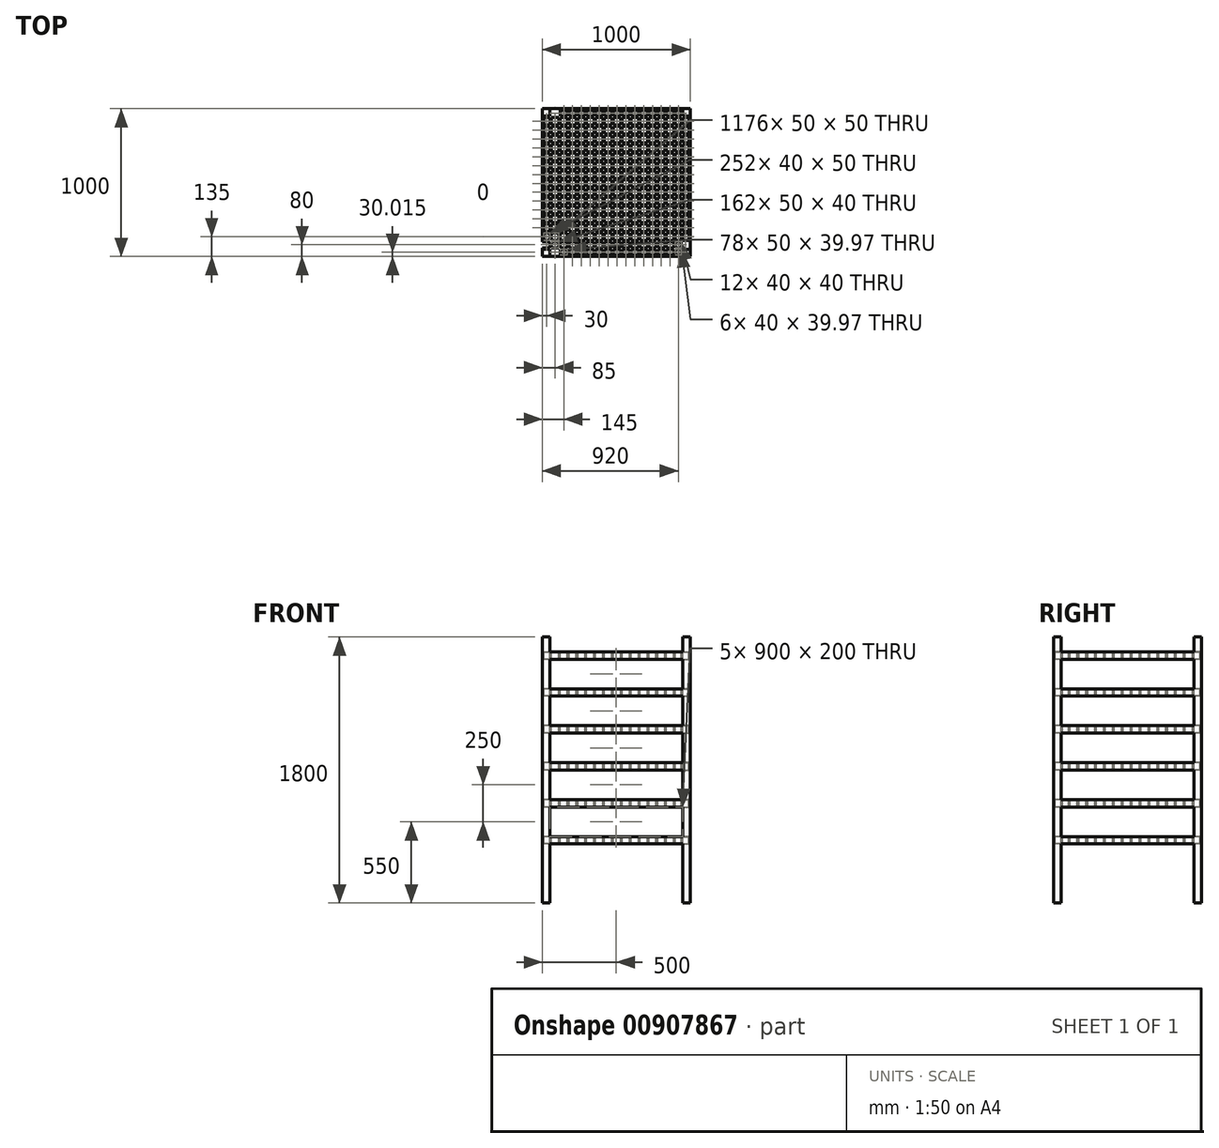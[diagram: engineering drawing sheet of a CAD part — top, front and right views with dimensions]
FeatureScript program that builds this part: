
annotation { "Feature Type Name" : "Feature", "Feature Type Description" : "" }
export const myFeature = defineFeature(function(context is Context, id is Id, definition is map)
    precondition{}
    {
        {
            var Q0;
            Q0=qCreatedBy(makeId("Top.planeOp"),FACE);
            var sketch = newSketch(context, id + "F0", { "sketchPlane" : qUnion([Q0])});
            skLineSegment(sketch, "E0", {"start": v(0, 0) * mm, "end": v(0, 1000) * mm});
            skLineSegment(sketch, "E1", {"start": v(0, 1000) * mm, "end": v(-1000, 1000) * mm});
            skLineSegment(sketch, "E2", {"start": v(-1000, 1000) * mm, "end": v(-1000, 0) * mm});
            skLineSegment(sketch, "E3", {"start": v(-1000, 0) * mm, "end": v(0, 0) * mm});
            skSolve(sketch);
        }
        {
            var Q0;
            Q0=makeQuery(id+"F0.imprint","IMPRINT",FACE,{"disambiguationData":[TD([[makeQuery(id+"F0.imprint","IMPRINT",EDGE,{"derivedFrom":sQuery(id+"F0.wireOp",EDGE,"E0")}),1.0]])]});
            extrude(context, id + "F1", {"entities" : qUnion([Q0]), "depth" : 1800 * mm, "offsetDistance" : 25 * mm});
        }
        {
            var Q0;
            Q0=makeQuery(id+"F1.opExtrude","SWEPT_FACE",FACE,{"disambiguationData":[OSD([sQuery(id+"F0.wireOp",EDGE,"E3")])]});
            var sketch = newSketch(context, id + "F2", { "sketchPlane" : qUnion([Q0])});
            skLineSegment(sketch, "E4", {"start": v(-1000, 0) * mm, "end": v(-950, 0) * mm});
            skLineSegment(sketch, "E5", {"start": v(0, 0) * mm, "end": v(-50, 0) * mm});
            skLineSegment(sketch, "E6", {"start": v(0, 1800) * mm, "end": v(-50, 1800) * mm});
            skLineSegment(sketch, "E7", {"start": v(-50, 1800) * mm, "end": v(-50, 0) * mm});
            skLineSegment(sketch, "E8", {"start": v(-950, 0) * mm, "end": v(-950, 400) * mm});
            skLineSegment(sketch, "E9", {"start": v(-950, 400) * mm, "end": v(-950, 450) * mm});
            skLineSegment(sketch, "E10", {"start": v(-950, 450) * mm, "end": v(-950, 650) * mm});
            skLineSegment(sketch, "E11", {"start": v(-950, 650) * mm, "end": v(-950, 700) * mm});
            skLineSegment(sketch, "E12", {"start": v(-950, 700) * mm, "end": v(-950, 900) * mm});
            skLineSegment(sketch, "E13", {"start": v(-950, 900) * mm, "end": v(-950, 950) * mm});
            skLineSegment(sketch, "E14", {"start": v(-950, 950) * mm, "end": v(-950, 1150) * mm});
            skLineSegment(sketch, "E15", {"start": v(-950, 1150) * mm, "end": v(-950, 1200) * mm});
            skLineSegment(sketch, "E16", {"start": v(-950, 1200) * mm, "end": v(-950, 1400) * mm});
            skLineSegment(sketch, "E17", {"start": v(-950, 1400) * mm, "end": v(-950, 1450) * mm});
            skLineSegment(sketch, "E18", {"start": v(-950, 1450) * mm, "end": v(-950, 1650) * mm});
            skLineSegment(sketch, "E19", {"start": v(-950, 1650) * mm, "end": v(-950, 1700) * mm});
            skLineSegment(sketch, "E20", {"start": v(-950, 1700) * mm, "end": v(-950, 1800) * mm});
            skLineSegment(sketch, "E21", {"start": v(-950, 1700) * mm, "end": v(-50, 1700) * mm});
            skLineSegment(sketch, "E22", {"start": v(-950, 1650) * mm, "end": v(-50, 1650) * mm});
            skLineSegment(sketch, "E23", {"start": v(-950, 1450) * mm, "end": v(-50, 1450) * mm});
            skLineSegment(sketch, "E24", {"start": v(-950, 1400) * mm, "end": v(-50, 1400) * mm});
            skLineSegment(sketch, "E25", {"start": v(-950, 1200) * mm, "end": v(-50, 1200) * mm});
            skLineSegment(sketch, "E26", {"start": v(-950, 1150) * mm, "end": v(-50, 1150) * mm});
            skLineSegment(sketch, "E27", {"start": v(-950, 950) * mm, "end": v(-50, 950) * mm});
            skLineSegment(sketch, "E28", {"start": v(-950, 900) * mm, "end": v(-50, 900) * mm});
            skLineSegment(sketch, "E29", {"start": v(-950, 700) * mm, "end": v(-50, 700) * mm});
            skLineSegment(sketch, "E30", {"start": v(-950, 650) * mm, "end": v(-50, 650) * mm});
            skLineSegment(sketch, "E31", {"start": v(-950, 450) * mm, "end": v(-50, 450) * mm});
            skLineSegment(sketch, "E32", {"start": v(-950, 400) * mm, "end": v(-50, 400) * mm});
            skSolve(sketch);
        }
        {
            var Q0;
            Q0=makeQuery(id+"F1.opExtrude","SWEPT_FACE",FACE,{"disambiguationData":[OSD([sQuery(id+"F0.wireOp",EDGE,"E0")])]});
            var sketch = newSketch(context, id + "F3", { "sketchPlane" : qUnion([Q0])});
            skLineSegment(sketch, "E33", {"start": v(0, 0) * mm, "end": v(50, 0) * mm});
            skLineSegment(sketch, "E34", {"start": v(1000, 1800) * mm, "end": v(950, 1800) * mm});
            skLineSegment(sketch, "E35", {"start": v(950, 1800) * mm, "end": v(950, 0) * mm});
            skLineSegment(sketch, "E36", {"start": v(50, 0) * mm, "end": v(50, 400) * mm});
            skLineSegment(sketch, "E37", {"start": v(50, 400) * mm, "end": v(50, 450) * mm});
            skLineSegment(sketch, "E38", {"start": v(50, 450) * mm, "end": v(50, 650) * mm});
            skLineSegment(sketch, "E39", {"start": v(50, 650) * mm, "end": v(50, 700) * mm});
            skLineSegment(sketch, "E40", {"start": v(50, 700) * mm, "end": v(50, 900) * mm});
            skLineSegment(sketch, "E41", {"start": v(50, 900) * mm, "end": v(50, 950) * mm});
            skLineSegment(sketch, "E42", {"start": v(50, 950) * mm, "end": v(50, 1150) * mm});
            skLineSegment(sketch, "E43", {"start": v(50, 1150) * mm, "end": v(50, 1200) * mm});
            skLineSegment(sketch, "E44", {"start": v(50, 1200) * mm, "end": v(50, 1400) * mm});
            skLineSegment(sketch, "E45", {"start": v(50, 1400) * mm, "end": v(50, 1450) * mm});
            skLineSegment(sketch, "E46", {"start": v(50, 1450) * mm, "end": v(50, 1650) * mm});
            skLineSegment(sketch, "E47", {"start": v(50, 1650) * mm, "end": v(50, 1700) * mm});
            skLineSegment(sketch, "E48", {"start": v(50, 1700) * mm, "end": v(50, 1800) * mm});
            skLineSegment(sketch, "E49", {"start": v(50, 1700) * mm, "end": v(950, 1700) * mm});
            skLineSegment(sketch, "E50", {"start": v(50, 1650) * mm, "end": v(950, 1650) * mm});
            skLineSegment(sketch, "E51", {"start": v(50, 1450) * mm, "end": v(950, 1450) * mm});
            skLineSegment(sketch, "E52", {"start": v(50, 1400) * mm, "end": v(950, 1400) * mm});
            skLineSegment(sketch, "E53", {"start": v(50, 1200) * mm, "end": v(950, 1200) * mm});
            skLineSegment(sketch, "E54", {"start": v(50, 1150) * mm, "end": v(950, 1150) * mm});
            skLineSegment(sketch, "E55", {"start": v(50, 950) * mm, "end": v(950, 950) * mm});
            skLineSegment(sketch, "E56", {"start": v(50, 900) * mm, "end": v(950, 900) * mm});
            skLineSegment(sketch, "E57", {"start": v(50, 700) * mm, "end": v(950, 700) * mm});
            skLineSegment(sketch, "E58", {"start": v(50, 650) * mm, "end": v(950, 650) * mm});
            skLineSegment(sketch, "E59", {"start": v(50, 450) * mm, "end": v(950, 450) * mm});
            skLineSegment(sketch, "E60", {"start": v(50, 400) * mm, "end": v(950, 400) * mm});
            skSolve(sketch);
        }
        {
            var Q0;
            {var subQ4=sQuery(id+"F2.wireOp",EDGE,"E8");Q0=makeQuery(id+"F2.imprint","IMPRINT",FACE,{"disambiguationData":[TD([[makeQuery(id+"F2.imprint","IMPRINT",EDGE,{"derivedFrom":subQ4}),-1.0]])]});}
            var Q1;
            Q1=makeQuery(id+"F2.imprint","IMPRINT",FACE,{"disambiguationData":[TD([[makeQuery(id+"F2.imprint","IMPRINT",EDGE,{"derivedFrom":sQuery(id+"F2.wireOp",EDGE,"E10")}),-1.0]])]});
            var Q2;
            Q2=makeQuery(id+"F2.imprint","IMPRINT",FACE,{"disambiguationData":[TD([[makeQuery(id+"F2.imprint","IMPRINT",EDGE,{"derivedFrom":sQuery(id+"F2.wireOp",EDGE,"E12")}),-1.0]])]});
            var Q3;
            Q3=makeQuery(id+"F2.imprint","IMPRINT",FACE,{"disambiguationData":[TD([[makeQuery(id+"F2.imprint","IMPRINT",EDGE,{"derivedFrom":sQuery(id+"F2.wireOp",EDGE,"E14")}),-1.0]])]});
            var Q4;
            Q4=makeQuery(id+"F2.imprint","IMPRINT",FACE,{"disambiguationData":[TD([[makeQuery(id+"F2.imprint","IMPRINT",EDGE,{"derivedFrom":sQuery(id+"F2.wireOp",EDGE,"E16")}),-1.0]])]});
            var Q5;
            Q5=makeQuery(id+"F2.imprint","IMPRINT",FACE,{"disambiguationData":[TD([[makeQuery(id+"F2.imprint","IMPRINT",EDGE,{"derivedFrom":sQuery(id+"F2.wireOp",EDGE,"E18")}),-1.0]])]});
            var Q6;
            {var subQ4=sQuery(id+"F2.wireOp",EDGE,"E20");Q6=makeQuery(id+"F2.imprint","IMPRINT",FACE,{"disambiguationData":[TD([[makeQuery(id+"F2.imprint","IMPRINT",EDGE,{"derivedFrom":subQ4}),-1.0]])]});}
            extrude(context, id + "F4", {"entities" : qUnion([Q0, Q1, Q2, Q3, Q4, Q5, Q6]), "operationType" : NewBodyOperationType.REMOVE, "oppositeDirection" : true, "depth" : 1000 * mm, "offsetDistance" : 25 * mm});
        }
        {
            var Q0;
            {var subQ4=sQuery(id+"F3.wireOp",EDGE,"E36");Q0=makeQuery(id+"F3.imprint","IMPRINT",FACE,{"disambiguationData":[TD([[makeQuery(id+"F3.imprint","IMPRINT",EDGE,{"derivedFrom":subQ4}),-1.0]])]});}
            var Q1;
            Q1=makeQuery(id+"F3.imprint","IMPRINT",FACE,{"disambiguationData":[TD([[makeQuery(id+"F3.imprint","IMPRINT",EDGE,{"derivedFrom":sQuery(id+"F3.wireOp",EDGE,"E38")}),-1.0]])]});
            var Q2;
            Q2=makeQuery(id+"F3.imprint","IMPRINT",FACE,{"disambiguationData":[TD([[makeQuery(id+"F3.imprint","IMPRINT",EDGE,{"derivedFrom":sQuery(id+"F3.wireOp",EDGE,"E40")}),-1.0]])]});
            var Q3;
            Q3=makeQuery(id+"F3.imprint","IMPRINT",FACE,{"disambiguationData":[TD([[makeQuery(id+"F3.imprint","IMPRINT",EDGE,{"derivedFrom":sQuery(id+"F3.wireOp",EDGE,"E42")}),-1.0]])]});
            var Q4;
            Q4=makeQuery(id+"F3.imprint","IMPRINT",FACE,{"disambiguationData":[TD([[makeQuery(id+"F3.imprint","IMPRINT",EDGE,{"derivedFrom":sQuery(id+"F3.wireOp",EDGE,"E44")}),-1.0]])]});
            var Q5;
            Q5=makeQuery(id+"F3.imprint","IMPRINT",FACE,{"disambiguationData":[TD([[makeQuery(id+"F3.imprint","IMPRINT",EDGE,{"derivedFrom":sQuery(id+"F3.wireOp",EDGE,"E46")}),-1.0]])]});
            var Q6;
            {var subQ4=sQuery(id+"F3.wireOp",EDGE,"E48");Q6=makeQuery(id+"F3.imprint","IMPRINT",FACE,{"disambiguationData":[TD([[makeQuery(id+"F3.imprint","IMPRINT",EDGE,{"derivedFrom":subQ4}),-1.0]])]});}
            extrude(context, id + "F5", {"entities" : qUnion([Q0, Q1, Q2, Q3, Q4, Q5, Q6]), "operationType" : NewBodyOperationType.REMOVE, "oppositeDirection" : true, "depth" : 1000 * mm, "offsetDistance" : 25 * mm});
        }
        {
            var Q0;
            Q0=makeQuery(id+"F5.boolean.opBoolean","MERGE",FACE,{"derivedFrom":[makeQuery(id+"F4.boolean.opBoolean","COPY",FACE,{"derivedFrom":makeQuery(id+"F4.opExtrude","SWEPT_FACE",FACE,{"disambiguationData":[OSD([sQuery(id+"F2.wireOp",EDGE,"E21")])]})})],"fromTools":[makeQuery(id+"F5.opExtrude","SWEPT_FACE",FACE,{"disambiguationData":[OSD([sQuery(id+"F3.wireOp",EDGE,"E49")])]})]});
            var sketch = newSketch(context, id + "F6", { "sketchPlane" : qUnion([Q0])});
            skLineSegment(sketch, "E61", {"start": v(-1000, 50) * mm, "end": v(-1000, 60) * mm});
            skLineSegment(sketch, "E62", {"start": v(-1000, 60) * mm, "end": v(-950, 60) * mm});
            skLineSegment(sketch, "E63", {"start": v(-950, 60) * mm, "end": v(-940, 60) * mm});
            skLineSegment(sketch, "E64", {"start": v(-940, 60) * mm, "end": v(-940, 0) * mm});
            skLineSegment(sketch, "E65", {"start": v(-50, 0) * mm, "end": v(-60, 0) * mm});
            skLineSegment(sketch, "E66", {"start": v(-60, 0) * mm, "end": v(-60, 60) * mm});
            skLineSegment(sketch, "E67", {"start": v(-60, 60) * mm, "end": v(0, 60) * mm});
            skLineSegment(sketch, "E68", {"start": v(0, 950) * mm, "end": v(0, 940) * mm});
            skLineSegment(sketch, "E69", {"start": v(0, 940) * mm, "end": v(-60, 940) * mm});
            skLineSegment(sketch, "E70", {"start": v(-60, 940) * mm, "end": v(-60, 1000) * mm});
            skLineSegment(sketch, "E71", {"start": v(-950, 1000) * mm, "end": v(-940, 1000) * mm});
            skLineSegment(sketch, "E72", {"start": v(-940, 1000) * mm, "end": v(-940, 940) * mm});
            skLineSegment(sketch, "E73", {"start": v(-940, 940) * mm, "end": v(-1000, 940) * mm});
            skLineSegment(sketch, "E74", {"start": v(-1000, 940) * mm, "end": v(-1000, 890) * mm});
            skLineSegment(sketch, "E75", {"start": v(-1000, 890) * mm, "end": v(-1000, 880) * mm});
            skLineSegment(sketch, "E76", {"start": v(-1000, 880) * mm, "end": v(-1000, 830) * mm});
            skLineSegment(sketch, "E77", {"start": v(-1000, 830) * mm, "end": v(-1000, 820) * mm});
            skLineSegment(sketch, "E78", {"start": v(-1000, 820) * mm, "end": v(-1000, 770) * mm});
            skLineSegment(sketch, "E79", {"start": v(-1000, 770) * mm, "end": v(-1000, 760) * mm});
            skLineSegment(sketch, "E80", {"start": v(-1000, 760) * mm, "end": v(-1000, 710) * mm});
            skLineSegment(sketch, "E81", {"start": v(-1000, 710) * mm, "end": v(-1000, 700) * mm});
            skLineSegment(sketch, "E82", {"start": v(-1000, 700) * mm, "end": v(-1000, 650) * mm});
            skLineSegment(sketch, "E83", {"start": v(-1000, 650) * mm, "end": v(-1000, 640) * mm});
            skLineSegment(sketch, "E84", {"start": v(-1000, 640) * mm, "end": v(-1000, 590) * mm});
            skLineSegment(sketch, "E85", {"start": v(-1000, 590) * mm, "end": v(-1000, 580) * mm});
            skLineSegment(sketch, "E86", {"start": v(-1000, 580) * mm, "end": v(-1000, 530) * mm});
            skLineSegment(sketch, "E87", {"start": v(-1000, 530) * mm, "end": v(-1000, 520) * mm});
            skLineSegment(sketch, "E88", {"start": v(-1000, 520) * mm, "end": v(-1000, 470) * mm});
            skLineSegment(sketch, "E89", {"start": v(-1000, 470) * mm, "end": v(-1000, 460) * mm});
            skLineSegment(sketch, "E90", {"start": v(-1000, 460) * mm, "end": v(-1000, 410) * mm});
            skLineSegment(sketch, "E91", {"start": v(-1000, 410) * mm, "end": v(-1000, 400) * mm});
            skLineSegment(sketch, "E92", {"start": v(-1000, 400) * mm, "end": v(-1000, 350) * mm});
            skLineSegment(sketch, "E93", {"start": v(-1000, 350) * mm, "end": v(-1000, 340) * mm});
            skLineSegment(sketch, "E94", {"start": v(-1000, 340) * mm, "end": v(-1000, 290) * mm});
            skLineSegment(sketch, "E95", {"start": v(-1000, 290) * mm, "end": v(-1000, 280) * mm});
            skLineSegment(sketch, "E96", {"start": v(-1000, 280) * mm, "end": v(-1000, 230) * mm});
            skLineSegment(sketch, "E97", {"start": v(-1000, 230) * mm, "end": v(-1000, 220) * mm});
            skLineSegment(sketch, "E98", {"start": v(-1000, 220) * mm, "end": v(-1000, 170) * mm});
            skLineSegment(sketch, "E99", {"start": v(-1000, 170) * mm, "end": v(-1000, 160) * mm});
            skLineSegment(sketch, "E100", {"start": v(-1000, 160) * mm, "end": v(-1000, 110) * mm});
            skLineSegment(sketch, "E101", {"start": v(-1000, 110) * mm, "end": v(-1000, 100) * mm});
            skLineSegment(sketch, "E102", {"start": v(-1000, 100) * mm, "end": v(-1000, 60) * mm});
            skLineSegment(sketch, "E103", {"start": v(-940, 0) * mm, "end": v(-890, 0) * mm});
            skLineSegment(sketch, "E104", {"start": v(-890, 0) * mm, "end": v(-880, 0) * mm});
            skLineSegment(sketch, "E105", {"start": v(-880, 0) * mm, "end": v(-830, 0) * mm});
            skLineSegment(sketch, "E106", {"start": v(-830, 0) * mm, "end": v(-820, 0) * mm});
            skLineSegment(sketch, "E107", {"start": v(-820, 0) * mm, "end": v(-770, 0) * mm});
            skLineSegment(sketch, "E108", {"start": v(-770, 0) * mm, "end": v(-760, 0) * mm});
            skLineSegment(sketch, "E109", {"start": v(-760, 0) * mm, "end": v(-710, 0) * mm});
            skLineSegment(sketch, "E110", {"start": v(-710, 0) * mm, "end": v(-700, 0) * mm});
            skLineSegment(sketch, "E111", {"start": v(-700, 0) * mm, "end": v(-650, 0) * mm});
            skLineSegment(sketch, "E112", {"start": v(-650, 0) * mm, "end": v(-640, 0) * mm});
            skLineSegment(sketch, "E113", {"start": v(-640, 0) * mm, "end": v(-590, 0) * mm});
            skLineSegment(sketch, "E114", {"start": v(-590, 0) * mm, "end": v(-580, 0) * mm});
            skLineSegment(sketch, "E115", {"start": v(-580, 0) * mm, "end": v(-530, 0) * mm});
            skLineSegment(sketch, "E116", {"start": v(-530, 0) * mm, "end": v(-520, 0) * mm});
            skLineSegment(sketch, "E117", {"start": v(-520, 0) * mm, "end": v(-470, 0) * mm});
            skLineSegment(sketch, "E118", {"start": v(-470, 0) * mm, "end": v(-460, 0) * mm});
            skLineSegment(sketch, "E119", {"start": v(-460, 0) * mm, "end": v(-410, 0) * mm});
            skLineSegment(sketch, "E120", {"start": v(-410, 0) * mm, "end": v(-400, 0) * mm});
            skLineSegment(sketch, "E121", {"start": v(-400, 0) * mm, "end": v(-350, 0) * mm});
            skLineSegment(sketch, "E122", {"start": v(-350, 0) * mm, "end": v(-340, 0) * mm});
            skLineSegment(sketch, "E123", {"start": v(-340, 0) * mm, "end": v(-290, 0) * mm});
            skLineSegment(sketch, "E124", {"start": v(-290, 0) * mm, "end": v(-280, 0) * mm});
            skLineSegment(sketch, "E125", {"start": v(-280, 0) * mm, "end": v(-230, 0) * mm});
            skLineSegment(sketch, "E126", {"start": v(-230, 0) * mm, "end": v(-220, 0) * mm});
            skLineSegment(sketch, "E127", {"start": v(-220, 0) * mm, "end": v(-170, 0) * mm});
            skLineSegment(sketch, "E128", {"start": v(-170, 0) * mm, "end": v(-160, 0) * mm});
            skLineSegment(sketch, "E129", {"start": v(-160, 0) * mm, "end": v(-110, 0) * mm});
            skLineSegment(sketch, "E130", {"start": v(-110, 0) * mm, "end": v(-100, 0) * mm});
            skLineSegment(sketch, "E131", {"start": v(-100, 0) * mm, "end": v(-60, 0) * mm});
            skLineSegment(sketch, "E132", {"start": v(-940, 60) * mm, "end": v(-940, 50) * mm});
            skLineSegment(sketch, "E133", {"start": v(-940, 50) * mm, "end": v(-940, 10.03) * mm});
            skLineSegment(sketch, "E134", {"start": v(-940, 10.03) * mm, "end": v(-940, 0) * mm});
            skLineSegment(sketch, "E135", {"start": v(-940, 10.03) * mm, "end": v(-60, 10.03) * mm});
            skLineSegment(sketch, "E136", {"start": v(-940, 50) * mm, "end": v(-60, 50) * mm});
            skLineSegment(sketch, "E137", {"start": v(-940, 60) * mm, "end": v(-60, 60) * mm});
            skLineSegment(sketch, "E138", {"start": v(-1000, 100) * mm, "end": v(0, 100) * mm});
            skLineSegment(sketch, "E139", {"start": v(-1000, 110) * mm, "end": v(0, 110) * mm});
            skLineSegment(sketch, "E140", {"start": v(-1000, 160) * mm, "end": v(0, 160) * mm});
            skLineSegment(sketch, "E141", {"start": v(-1000, 170) * mm, "end": v(0, 170) * mm});
            skLineSegment(sketch, "E142", {"start": v(-1000, 220) * mm, "end": v(0, 220) * mm});
            skLineSegment(sketch, "E143", {"start": v(-1000, 230) * mm, "end": v(0, 230) * mm});
            skLineSegment(sketch, "E144", {"start": v(-1000, 280) * mm, "end": v(0, 280) * mm});
            skLineSegment(sketch, "E145", {"start": v(-1000, 290) * mm, "end": v(0, 290) * mm});
            skLineSegment(sketch, "E146", {"start": v(-1000, 340) * mm, "end": v(0, 340) * mm});
            skLineSegment(sketch, "E147", {"start": v(-1000, 350) * mm, "end": v(0, 350) * mm});
            skLineSegment(sketch, "E148", {"start": v(-1000, 400) * mm, "end": v(0, 400) * mm});
            skLineSegment(sketch, "E149", {"start": v(-1000, 410) * mm, "end": v(0, 410) * mm});
            skLineSegment(sketch, "E150", {"start": v(-1000, 460) * mm, "end": v(0, 460) * mm});
            skLineSegment(sketch, "E151", {"start": v(-1000, 470) * mm, "end": v(0, 470) * mm});
            skLineSegment(sketch, "E152", {"start": v(-1000, 520) * mm, "end": v(0, 520) * mm});
            skLineSegment(sketch, "E153", {"start": v(-1000, 530) * mm, "end": v(0, 530) * mm});
            skLineSegment(sketch, "E154", {"start": v(-1000, 580) * mm, "end": v(0, 580) * mm});
            skLineSegment(sketch, "E155", {"start": v(-1000, 590) * mm, "end": v(0, 590) * mm});
            skLineSegment(sketch, "E156", {"start": v(-1000, 640) * mm, "end": v(0, 640) * mm});
            skLineSegment(sketch, "E157", {"start": v(-1000, 650) * mm, "end": v(0, 650) * mm});
            skLineSegment(sketch, "E158", {"start": v(-1000, 700) * mm, "end": v(0, 700) * mm});
            skLineSegment(sketch, "E159", {"start": v(-1000, 710) * mm, "end": v(0, 710) * mm});
            skLineSegment(sketch, "E160", {"start": v(-1000, 760) * mm, "end": v(0, 760) * mm});
            skLineSegment(sketch, "E161", {"start": v(-1000, 770) * mm, "end": v(0, 770) * mm});
            skLineSegment(sketch, "E162", {"start": v(-1000, 820) * mm, "end": v(0, 820) * mm});
            skLineSegment(sketch, "E163", {"start": v(-1000, 830) * mm, "end": v(0, 830) * mm});
            skLineSegment(sketch, "E164", {"start": v(-1000, 880) * mm, "end": v(0, 880) * mm});
            skLineSegment(sketch, "E165", {"start": v(-1000, 890) * mm, "end": v(0, 890) * mm});
            skLineSegment(sketch, "E166", {"start": v(-1000, 940) * mm, "end": v(-60, 940) * mm});
            skLineSegment(sketch, "E167", {"start": v(-940, 1000) * mm, "end": v(-940, 990) * mm});
            skLineSegment(sketch, "E168", {"start": v(-940, 990) * mm, "end": v(-940, 950) * mm});
            skLineSegment(sketch, "E169", {"start": v(-940, 950) * mm, "end": v(-60, 950) * mm});
            skLineSegment(sketch, "E170", {"start": v(-940, 990) * mm, "end": v(-60, 990) * mm});
            skLineSegment(sketch, "E171", {"start": v(0, 60) * mm, "end": v(-10, 60) * mm});
            skLineSegment(sketch, "E172", {"start": v(-10, 60) * mm, "end": v(-50, 60) * mm});
            skLineSegment(sketch, "E173", {"start": v(-10, 60) * mm, "end": v(-10, 940) * mm});
            skLineSegment(sketch, "E174", {"start": v(-50, 60) * mm, "end": v(-50, 940) * mm});
            skLineSegment(sketch, "E175", {"start": v(-60, 60) * mm, "end": v(-60, 940) * mm});
            skLineSegment(sketch, "E176", {"start": v(-100, 0) * mm, "end": v(-100, 990) * mm});
            skLineSegment(sketch, "E177", {"start": v(-110, 0) * mm, "end": v(-110, 990) * mm});
            skLineSegment(sketch, "E178", {"start": v(-160, 0) * mm, "end": v(-160, 990) * mm});
            skLineSegment(sketch, "E179", {"start": v(-170, 0) * mm, "end": v(-170, 990) * mm});
            skLineSegment(sketch, "E180", {"start": v(-220, 0) * mm, "end": v(-220, 990) * mm});
            skLineSegment(sketch, "E181", {"start": v(-230, 0) * mm, "end": v(-230, 990) * mm});
            skLineSegment(sketch, "E182", {"start": v(-280, 0) * mm, "end": v(-280, 990) * mm});
            skLineSegment(sketch, "E183", {"start": v(-290, 0) * mm, "end": v(-290, 990) * mm});
            skLineSegment(sketch, "E184", {"start": v(-340, 0) * mm, "end": v(-340, 990) * mm});
            skLineSegment(sketch, "E185", {"start": v(-350, 0) * mm, "end": v(-350, 990) * mm});
            skLineSegment(sketch, "E186", {"start": v(-400, 0) * mm, "end": v(-400, 990) * mm});
            skLineSegment(sketch, "E187", {"start": v(-410, 0) * mm, "end": v(-410, 990) * mm});
            skLineSegment(sketch, "E188", {"start": v(-460, 0) * mm, "end": v(-460, 990) * mm});
            skLineSegment(sketch, "E189", {"start": v(-470, 0) * mm, "end": v(-470, 990) * mm});
            skLineSegment(sketch, "E190", {"start": v(-520, 0) * mm, "end": v(-520, 990) * mm});
            skLineSegment(sketch, "E191", {"start": v(-530, 0) * mm, "end": v(-530, 990) * mm});
            skLineSegment(sketch, "E192", {"start": v(-580, 0) * mm, "end": v(-580, 990) * mm});
            skLineSegment(sketch, "E193", {"start": v(-590, 0) * mm, "end": v(-590, 990) * mm});
            skLineSegment(sketch, "E194", {"start": v(-640, 0) * mm, "end": v(-640, 990) * mm});
            skLineSegment(sketch, "E195", {"start": v(-650, 0) * mm, "end": v(-650, 990) * mm});
            skLineSegment(sketch, "E196", {"start": v(-700, 0) * mm, "end": v(-700, 990) * mm});
            skLineSegment(sketch, "E197", {"start": v(-710, 0) * mm, "end": v(-710, 990) * mm});
            skLineSegment(sketch, "E198", {"start": v(-760, 0) * mm, "end": v(-760, 990) * mm});
            skLineSegment(sketch, "E199", {"start": v(-770, 0) * mm, "end": v(-770, 990) * mm});
            skLineSegment(sketch, "E200", {"start": v(-820, 0) * mm, "end": v(-820, 990) * mm});
            skLineSegment(sketch, "E201", {"start": v(-830, 0) * mm, "end": v(-830, 990) * mm});
            skLineSegment(sketch, "E202", {"start": v(-880, 0) * mm, "end": v(-880, 990) * mm});
            skLineSegment(sketch, "E203", {"start": v(-890, 0) * mm, "end": v(-890, 990) * mm});
            skLineSegment(sketch, "E204", {"start": v(-940, 60) * mm, "end": v(-940, 940) * mm});
            skLineSegment(sketch, "E205", {"start": v(-950, 60) * mm, "end": v(-950, 940) * mm});
            skLineSegment(sketch, "E206", {"start": v(-1000, 60) * mm, "end": v(-990, 60) * mm});
            skLineSegment(sketch, "E207", {"start": v(-990, 60) * mm, "end": v(-990, 940) * mm});
            skSolve(sketch);
        }
        {
            var Q0;
            {var subQ5=sQuery(id+"F6.wireOp",EDGE,"E172");Q0=makeQuery(id+"F6.imprint","IMPRINT",FACE,{"disambiguationData":[TD([[makeQuery(id+"F6.imprint","IMPRINT",EDGE,{"derivedFrom":subQ5}),-1.0]])]});}
            var Q1;
            {var subQ0=sQuery(id+"F6.wireOp",EDGE,"E173");var subQ1=sQuery(id+"F6.wireOp",EDGE,"E69");var subQ2=makeQuery(id+"F6.imprint","INTERSECT",VERTEX,{"derivedFrom":[subQ1,subQ0]});Q1=makeQuery(id+"F6.imprint","IMPRINT",FACE,{"disambiguationData":[TD([[makeQuery(id+"F6.imprint","IMPRINT",EDGE,{"disambiguationData":[TD([[subQ2,-1.0]])],"derivedFrom":subQ1}),1.0]])]});}
            var Q2;
            {var subQ0=sQuery(id+"F6.wireOp",EDGE,"E174");var subQ1=sQuery(id+"F6.wireOp",EDGE,"E163");var subQ2=makeQuery(id+"F6.imprint","INTERSECT",VERTEX,{"derivedFrom":[subQ1,subQ0]});Q2=makeQuery(id+"F6.imprint","IMPRINT",FACE,{"disambiguationData":[TD([[makeQuery(id+"F6.imprint","IMPRINT",EDGE,{"disambiguationData":[TD([[subQ2,-1.0]])],"derivedFrom":subQ1}),1.0]])]});}
            var Q3;
            {var subQ0=sQuery(id+"F6.wireOp",EDGE,"E174");var subQ1=sQuery(id+"F6.wireOp",EDGE,"E161");var subQ2=makeQuery(id+"F6.imprint","INTERSECT",VERTEX,{"derivedFrom":[subQ1,subQ0]});Q3=makeQuery(id+"F6.imprint","IMPRINT",FACE,{"disambiguationData":[TD([[makeQuery(id+"F6.imprint","IMPRINT",EDGE,{"disambiguationData":[TD([[subQ2,-1.0]])],"derivedFrom":subQ1}),1.0]])]});}
            var Q4;
            {var subQ0=sQuery(id+"F6.wireOp",EDGE,"E174");var subQ1=sQuery(id+"F6.wireOp",EDGE,"E159");var subQ2=makeQuery(id+"F6.imprint","INTERSECT",VERTEX,{"derivedFrom":[subQ1,subQ0]});Q4=makeQuery(id+"F6.imprint","IMPRINT",FACE,{"disambiguationData":[TD([[makeQuery(id+"F6.imprint","IMPRINT",EDGE,{"disambiguationData":[TD([[subQ2,-1.0]])],"derivedFrom":subQ1}),1.0]])]});}
            var Q5;
            {var subQ0=sQuery(id+"F6.wireOp",EDGE,"E174");var subQ1=sQuery(id+"F6.wireOp",EDGE,"E157");var subQ2=makeQuery(id+"F6.imprint","INTERSECT",VERTEX,{"derivedFrom":[subQ1,subQ0]});Q5=makeQuery(id+"F6.imprint","IMPRINT",FACE,{"disambiguationData":[TD([[makeQuery(id+"F6.imprint","IMPRINT",EDGE,{"disambiguationData":[TD([[subQ2,-1.0]])],"derivedFrom":subQ1}),1.0]])]});}
            var Q6;
            {var subQ0=sQuery(id+"F6.wireOp",EDGE,"E174");var subQ1=sQuery(id+"F6.wireOp",EDGE,"E155");var subQ2=makeQuery(id+"F6.imprint","INTERSECT",VERTEX,{"derivedFrom":[subQ1,subQ0]});Q6=makeQuery(id+"F6.imprint","IMPRINT",FACE,{"disambiguationData":[TD([[makeQuery(id+"F6.imprint","IMPRINT",EDGE,{"disambiguationData":[TD([[subQ2,-1.0]])],"derivedFrom":subQ1}),1.0]])]});}
            var Q7;
            {var subQ0=sQuery(id+"F6.wireOp",EDGE,"E174");var subQ1=sQuery(id+"F6.wireOp",EDGE,"E153");var subQ2=makeQuery(id+"F6.imprint","INTERSECT",VERTEX,{"derivedFrom":[subQ1,subQ0]});Q7=makeQuery(id+"F6.imprint","IMPRINT",FACE,{"disambiguationData":[TD([[makeQuery(id+"F6.imprint","IMPRINT",EDGE,{"disambiguationData":[TD([[subQ2,-1.0]])],"derivedFrom":subQ1}),1.0]])]});}
            var Q8;
            {var subQ0=sQuery(id+"F6.wireOp",EDGE,"E174");var subQ1=sQuery(id+"F6.wireOp",EDGE,"E151");var subQ2=makeQuery(id+"F6.imprint","INTERSECT",VERTEX,{"derivedFrom":[subQ1,subQ0]});Q8=makeQuery(id+"F6.imprint","IMPRINT",FACE,{"disambiguationData":[TD([[makeQuery(id+"F6.imprint","IMPRINT",EDGE,{"disambiguationData":[TD([[subQ2,-1.0]])],"derivedFrom":subQ1}),1.0]])]});}
            var Q9;
            {var subQ0=sQuery(id+"F6.wireOp",EDGE,"E174");var subQ1=sQuery(id+"F6.wireOp",EDGE,"E149");var subQ2=makeQuery(id+"F6.imprint","INTERSECT",VERTEX,{"derivedFrom":[subQ1,subQ0]});Q9=makeQuery(id+"F6.imprint","IMPRINT",FACE,{"disambiguationData":[TD([[makeQuery(id+"F6.imprint","IMPRINT",EDGE,{"disambiguationData":[TD([[subQ2,-1.0]])],"derivedFrom":subQ1}),1.0]])]});}
            var Q10;
            {var subQ0=sQuery(id+"F6.wireOp",EDGE,"E174");var subQ1=sQuery(id+"F6.wireOp",EDGE,"E147");var subQ2=makeQuery(id+"F6.imprint","INTERSECT",VERTEX,{"derivedFrom":[subQ1,subQ0]});Q10=makeQuery(id+"F6.imprint","IMPRINT",FACE,{"disambiguationData":[TD([[makeQuery(id+"F6.imprint","IMPRINT",EDGE,{"disambiguationData":[TD([[subQ2,-1.0]])],"derivedFrom":subQ1}),1.0]])]});}
            var Q11;
            {var subQ0=sQuery(id+"F6.wireOp",EDGE,"E174");var subQ1=sQuery(id+"F6.wireOp",EDGE,"E145");var subQ2=makeQuery(id+"F6.imprint","INTERSECT",VERTEX,{"derivedFrom":[subQ1,subQ0]});Q11=makeQuery(id+"F6.imprint","IMPRINT",FACE,{"disambiguationData":[TD([[makeQuery(id+"F6.imprint","IMPRINT",EDGE,{"disambiguationData":[TD([[subQ2,-1.0]])],"derivedFrom":subQ1}),1.0]])]});}
            var Q12;
            {var subQ0=sQuery(id+"F6.wireOp",EDGE,"E174");var subQ1=sQuery(id+"F6.wireOp",EDGE,"E143");var subQ2=makeQuery(id+"F6.imprint","INTERSECT",VERTEX,{"derivedFrom":[subQ1,subQ0]});Q12=makeQuery(id+"F6.imprint","IMPRINT",FACE,{"disambiguationData":[TD([[makeQuery(id+"F6.imprint","IMPRINT",EDGE,{"disambiguationData":[TD([[subQ2,-1.0]])],"derivedFrom":subQ1}),1.0]])]});}
            var Q13;
            {var subQ0=sQuery(id+"F6.wireOp",EDGE,"E174");var subQ1=sQuery(id+"F6.wireOp",EDGE,"E141");var subQ2=makeQuery(id+"F6.imprint","INTERSECT",VERTEX,{"derivedFrom":[subQ1,subQ0]});Q13=makeQuery(id+"F6.imprint","IMPRINT",FACE,{"disambiguationData":[TD([[makeQuery(id+"F6.imprint","IMPRINT",EDGE,{"disambiguationData":[TD([[subQ2,-1.0]])],"derivedFrom":subQ1}),1.0]])]});}
            var Q14;
            {var subQ0=sQuery(id+"F6.wireOp",EDGE,"E174");var subQ1=sQuery(id+"F6.wireOp",EDGE,"E139");var subQ2=makeQuery(id+"F6.imprint","INTERSECT",VERTEX,{"derivedFrom":[subQ1,subQ0]});Q14=makeQuery(id+"F6.imprint","IMPRINT",FACE,{"disambiguationData":[TD([[makeQuery(id+"F6.imprint","IMPRINT",EDGE,{"disambiguationData":[TD([[subQ2,-1.0]])],"derivedFrom":subQ1}),1.0]])]});}
            var Q15;
            {var subQ0=sQuery(id+"F6.wireOp",EDGE,"E135");var subQ1=sQuery(id+"F6.wireOp",EDGE,"E66");var subQ2=makeQuery(id+"F6.imprint","INTERSECT",VERTEX,{"derivedFrom":[subQ1,subQ0]});Q15=makeQuery(id+"F6.imprint","IMPRINT",FACE,{"disambiguationData":[TD([[makeQuery(id+"F6.imprint","IMPRINT",EDGE,{"disambiguationData":[TD([[subQ2,-1.0]])],"derivedFrom":subQ1}),1.0]])]});}
            var Q16;
            {var subQ3=sQuery(id+"F6.wireOp",EDGE,"E176");var subQ5=sQuery(id+"F6.wireOp",EDGE,"E138");var subQ6=makeQuery(id+"F6.imprint","INTERSECT",VERTEX,{"derivedFrom":[subQ5,subQ3]});Q16=makeQuery(id+"F6.imprint","IMPRINT",FACE,{"disambiguationData":[TD([[makeQuery(id+"F6.imprint","IMPRINT",EDGE,{"disambiguationData":[TD([[subQ6,-1.0]])],"derivedFrom":subQ5}),-1.0]])]});}
            var Q17;
            {var subQ0=sQuery(id+"F6.wireOp",EDGE,"E176");var subQ1=sQuery(id+"F6.wireOp",EDGE,"E139");var subQ2=makeQuery(id+"F6.imprint","INTERSECT",VERTEX,{"derivedFrom":[subQ1,subQ0]});Q17=makeQuery(id+"F6.imprint","IMPRINT",FACE,{"disambiguationData":[TD([[makeQuery(id+"F6.imprint","IMPRINT",EDGE,{"disambiguationData":[TD([[subQ2,-1.0]])],"derivedFrom":subQ1}),1.0]])]});}
            var Q18;
            {var subQ0=sQuery(id+"F6.wireOp",EDGE,"E176");var subQ1=sQuery(id+"F6.wireOp",EDGE,"E141");var subQ2=makeQuery(id+"F6.imprint","INTERSECT",VERTEX,{"derivedFrom":[subQ1,subQ0]});Q18=makeQuery(id+"F6.imprint","IMPRINT",FACE,{"disambiguationData":[TD([[makeQuery(id+"F6.imprint","IMPRINT",EDGE,{"disambiguationData":[TD([[subQ2,-1.0]])],"derivedFrom":subQ1}),1.0]])]});}
            var Q19;
            {var subQ0=sQuery(id+"F6.wireOp",EDGE,"E176");var subQ1=sQuery(id+"F6.wireOp",EDGE,"E143");var subQ2=makeQuery(id+"F6.imprint","INTERSECT",VERTEX,{"derivedFrom":[subQ1,subQ0]});Q19=makeQuery(id+"F6.imprint","IMPRINT",FACE,{"disambiguationData":[TD([[makeQuery(id+"F6.imprint","IMPRINT",EDGE,{"disambiguationData":[TD([[subQ2,-1.0]])],"derivedFrom":subQ1}),1.0]])]});}
            var Q20;
            {var subQ0=sQuery(id+"F6.wireOp",EDGE,"E176");var subQ1=sQuery(id+"F6.wireOp",EDGE,"E145");var subQ2=makeQuery(id+"F6.imprint","INTERSECT",VERTEX,{"derivedFrom":[subQ1,subQ0]});Q20=makeQuery(id+"F6.imprint","IMPRINT",FACE,{"disambiguationData":[TD([[makeQuery(id+"F6.imprint","IMPRINT",EDGE,{"disambiguationData":[TD([[subQ2,-1.0]])],"derivedFrom":subQ1}),1.0]])]});}
            var Q21;
            {var subQ0=sQuery(id+"F6.wireOp",EDGE,"E176");var subQ1=sQuery(id+"F6.wireOp",EDGE,"E147");var subQ2=makeQuery(id+"F6.imprint","INTERSECT",VERTEX,{"derivedFrom":[subQ1,subQ0]});Q21=makeQuery(id+"F6.imprint","IMPRINT",FACE,{"disambiguationData":[TD([[makeQuery(id+"F6.imprint","IMPRINT",EDGE,{"disambiguationData":[TD([[subQ2,-1.0]])],"derivedFrom":subQ1}),1.0]])]});}
            var Q22;
            {var subQ0=sQuery(id+"F6.wireOp",EDGE,"E176");var subQ1=sQuery(id+"F6.wireOp",EDGE,"E149");var subQ2=makeQuery(id+"F6.imprint","INTERSECT",VERTEX,{"derivedFrom":[subQ1,subQ0]});Q22=makeQuery(id+"F6.imprint","IMPRINT",FACE,{"disambiguationData":[TD([[makeQuery(id+"F6.imprint","IMPRINT",EDGE,{"disambiguationData":[TD([[subQ2,-1.0]])],"derivedFrom":subQ1}),1.0]])]});}
            var Q23;
            {var subQ0=sQuery(id+"F6.wireOp",EDGE,"E176");var subQ1=sQuery(id+"F6.wireOp",EDGE,"E151");var subQ2=makeQuery(id+"F6.imprint","INTERSECT",VERTEX,{"derivedFrom":[subQ1,subQ0]});Q23=makeQuery(id+"F6.imprint","IMPRINT",FACE,{"disambiguationData":[TD([[makeQuery(id+"F6.imprint","IMPRINT",EDGE,{"disambiguationData":[TD([[subQ2,-1.0]])],"derivedFrom":subQ1}),1.0]])]});}
            var Q24;
            {var subQ0=sQuery(id+"F6.wireOp",EDGE,"E176");var subQ1=sQuery(id+"F6.wireOp",EDGE,"E153");var subQ2=makeQuery(id+"F6.imprint","INTERSECT",VERTEX,{"derivedFrom":[subQ1,subQ0]});Q24=makeQuery(id+"F6.imprint","IMPRINT",FACE,{"disambiguationData":[TD([[makeQuery(id+"F6.imprint","IMPRINT",EDGE,{"disambiguationData":[TD([[subQ2,-1.0]])],"derivedFrom":subQ1}),1.0]])]});}
            var Q25;
            {var subQ0=sQuery(id+"F6.wireOp",EDGE,"E176");var subQ1=sQuery(id+"F6.wireOp",EDGE,"E155");var subQ2=makeQuery(id+"F6.imprint","INTERSECT",VERTEX,{"derivedFrom":[subQ1,subQ0]});Q25=makeQuery(id+"F6.imprint","IMPRINT",FACE,{"disambiguationData":[TD([[makeQuery(id+"F6.imprint","IMPRINT",EDGE,{"disambiguationData":[TD([[subQ2,-1.0]])],"derivedFrom":subQ1}),1.0]])]});}
            var Q26;
            {var subQ0=sQuery(id+"F6.wireOp",EDGE,"E176");var subQ1=sQuery(id+"F6.wireOp",EDGE,"E157");var subQ2=makeQuery(id+"F6.imprint","INTERSECT",VERTEX,{"derivedFrom":[subQ1,subQ0]});Q26=makeQuery(id+"F6.imprint","IMPRINT",FACE,{"disambiguationData":[TD([[makeQuery(id+"F6.imprint","IMPRINT",EDGE,{"disambiguationData":[TD([[subQ2,-1.0]])],"derivedFrom":subQ1}),1.0]])]});}
            var Q27;
            {var subQ0=sQuery(id+"F6.wireOp",EDGE,"E176");var subQ1=sQuery(id+"F6.wireOp",EDGE,"E159");var subQ2=makeQuery(id+"F6.imprint","INTERSECT",VERTEX,{"derivedFrom":[subQ1,subQ0]});Q27=makeQuery(id+"F6.imprint","IMPRINT",FACE,{"disambiguationData":[TD([[makeQuery(id+"F6.imprint","IMPRINT",EDGE,{"disambiguationData":[TD([[subQ2,-1.0]])],"derivedFrom":subQ1}),1.0]])]});}
            var Q28;
            {var subQ0=sQuery(id+"F6.wireOp",EDGE,"E176");var subQ1=sQuery(id+"F6.wireOp",EDGE,"E161");var subQ2=makeQuery(id+"F6.imprint","INTERSECT",VERTEX,{"derivedFrom":[subQ1,subQ0]});Q28=makeQuery(id+"F6.imprint","IMPRINT",FACE,{"disambiguationData":[TD([[makeQuery(id+"F6.imprint","IMPRINT",EDGE,{"disambiguationData":[TD([[subQ2,-1.0]])],"derivedFrom":subQ1}),1.0]])]});}
            var Q29;
            {var subQ0=sQuery(id+"F6.wireOp",EDGE,"E176");var subQ1=sQuery(id+"F6.wireOp",EDGE,"E163");var subQ2=makeQuery(id+"F6.imprint","INTERSECT",VERTEX,{"derivedFrom":[subQ1,subQ0]});Q29=makeQuery(id+"F6.imprint","IMPRINT",FACE,{"disambiguationData":[TD([[makeQuery(id+"F6.imprint","IMPRINT",EDGE,{"disambiguationData":[TD([[subQ2,-1.0]])],"derivedFrom":subQ1}),1.0]])]});}
            var Q30;
            {var subQ0=sQuery(id+"F6.wireOp",EDGE,"E176");var subQ1=sQuery(id+"F6.wireOp",EDGE,"E165");var subQ2=makeQuery(id+"F6.imprint","INTERSECT",VERTEX,{"derivedFrom":[subQ1,subQ0]});Q30=makeQuery(id+"F6.imprint","IMPRINT",FACE,{"disambiguationData":[TD([[makeQuery(id+"F6.imprint","IMPRINT",EDGE,{"disambiguationData":[TD([[subQ2,-1.0]])],"derivedFrom":subQ1}),1.0]])]});}
            var Q31;
            {var subQ0=sQuery(id+"F6.wireOp",EDGE,"E169");var subQ1=sQuery(id+"F6.wireOp",EDGE,"E70");var subQ2=makeQuery(id+"F6.imprint","INTERSECT",VERTEX,{"derivedFrom":[subQ1,subQ0]});Q31=makeQuery(id+"F6.imprint","IMPRINT",FACE,{"disambiguationData":[TD([[makeQuery(id+"F6.imprint","IMPRINT",EDGE,{"disambiguationData":[TD([[subQ2,-1.0]])],"derivedFrom":subQ1}),1.0]])]});}
            var Q32;
            {var subQ0=sQuery(id+"F6.wireOp",EDGE,"E178");var subQ1=sQuery(id+"F6.wireOp",EDGE,"E169");var subQ2=makeQuery(id+"F6.imprint","INTERSECT",VERTEX,{"derivedFrom":[subQ1,subQ0]});Q32=makeQuery(id+"F6.imprint","IMPRINT",FACE,{"disambiguationData":[TD([[makeQuery(id+"F6.imprint","IMPRINT",EDGE,{"disambiguationData":[TD([[subQ2,-1.0]])],"derivedFrom":subQ1}),1.0]])]});}
            var Q33;
            {var subQ0=sQuery(id+"F6.wireOp",EDGE,"E178");var subQ1=sQuery(id+"F6.wireOp",EDGE,"E165");var subQ2=makeQuery(id+"F6.imprint","INTERSECT",VERTEX,{"derivedFrom":[subQ1,subQ0]});Q33=makeQuery(id+"F6.imprint","IMPRINT",FACE,{"disambiguationData":[TD([[makeQuery(id+"F6.imprint","IMPRINT",EDGE,{"disambiguationData":[TD([[subQ2,-1.0]])],"derivedFrom":subQ1}),1.0]])]});}
            var Q34;
            {var subQ0=sQuery(id+"F6.wireOp",EDGE,"E178");var subQ1=sQuery(id+"F6.wireOp",EDGE,"E163");var subQ2=makeQuery(id+"F6.imprint","INTERSECT",VERTEX,{"derivedFrom":[subQ1,subQ0]});Q34=makeQuery(id+"F6.imprint","IMPRINT",FACE,{"disambiguationData":[TD([[makeQuery(id+"F6.imprint","IMPRINT",EDGE,{"disambiguationData":[TD([[subQ2,-1.0]])],"derivedFrom":subQ1}),1.0]])]});}
            var Q35;
            {var subQ0=sQuery(id+"F6.wireOp",EDGE,"E178");var subQ1=sQuery(id+"F6.wireOp",EDGE,"E161");var subQ2=makeQuery(id+"F6.imprint","INTERSECT",VERTEX,{"derivedFrom":[subQ1,subQ0]});Q35=makeQuery(id+"F6.imprint","IMPRINT",FACE,{"disambiguationData":[TD([[makeQuery(id+"F6.imprint","IMPRINT",EDGE,{"disambiguationData":[TD([[subQ2,-1.0]])],"derivedFrom":subQ1}),1.0]])]});}
            var Q36;
            {var subQ0=sQuery(id+"F6.wireOp",EDGE,"E178");var subQ1=sQuery(id+"F6.wireOp",EDGE,"E159");var subQ2=makeQuery(id+"F6.imprint","INTERSECT",VERTEX,{"derivedFrom":[subQ1,subQ0]});Q36=makeQuery(id+"F6.imprint","IMPRINT",FACE,{"disambiguationData":[TD([[makeQuery(id+"F6.imprint","IMPRINT",EDGE,{"disambiguationData":[TD([[subQ2,-1.0]])],"derivedFrom":subQ1}),1.0]])]});}
            var Q37;
            {var subQ0=sQuery(id+"F6.wireOp",EDGE,"E178");var subQ1=sQuery(id+"F6.wireOp",EDGE,"E157");var subQ2=makeQuery(id+"F6.imprint","INTERSECT",VERTEX,{"derivedFrom":[subQ1,subQ0]});Q37=makeQuery(id+"F6.imprint","IMPRINT",FACE,{"disambiguationData":[TD([[makeQuery(id+"F6.imprint","IMPRINT",EDGE,{"disambiguationData":[TD([[subQ2,-1.0]])],"derivedFrom":subQ1}),1.0]])]});}
            var Q38;
            {var subQ0=sQuery(id+"F6.wireOp",EDGE,"E178");var subQ1=sQuery(id+"F6.wireOp",EDGE,"E155");var subQ2=makeQuery(id+"F6.imprint","INTERSECT",VERTEX,{"derivedFrom":[subQ1,subQ0]});Q38=makeQuery(id+"F6.imprint","IMPRINT",FACE,{"disambiguationData":[TD([[makeQuery(id+"F6.imprint","IMPRINT",EDGE,{"disambiguationData":[TD([[subQ2,-1.0]])],"derivedFrom":subQ1}),1.0]])]});}
            var Q39;
            {var subQ0=sQuery(id+"F6.wireOp",EDGE,"E178");var subQ1=sQuery(id+"F6.wireOp",EDGE,"E153");var subQ2=makeQuery(id+"F6.imprint","INTERSECT",VERTEX,{"derivedFrom":[subQ1,subQ0]});Q39=makeQuery(id+"F6.imprint","IMPRINT",FACE,{"disambiguationData":[TD([[makeQuery(id+"F6.imprint","IMPRINT",EDGE,{"disambiguationData":[TD([[subQ2,-1.0]])],"derivedFrom":subQ1}),1.0]])]});}
            var Q40;
            {var subQ0=sQuery(id+"F6.wireOp",EDGE,"E178");var subQ1=sQuery(id+"F6.wireOp",EDGE,"E151");var subQ2=makeQuery(id+"F6.imprint","INTERSECT",VERTEX,{"derivedFrom":[subQ1,subQ0]});Q40=makeQuery(id+"F6.imprint","IMPRINT",FACE,{"disambiguationData":[TD([[makeQuery(id+"F6.imprint","IMPRINT",EDGE,{"disambiguationData":[TD([[subQ2,-1.0]])],"derivedFrom":subQ1}),1.0]])]});}
            var Q41;
            {var subQ0=sQuery(id+"F6.wireOp",EDGE,"E178");var subQ1=sQuery(id+"F6.wireOp",EDGE,"E149");var subQ2=makeQuery(id+"F6.imprint","INTERSECT",VERTEX,{"derivedFrom":[subQ1,subQ0]});Q41=makeQuery(id+"F6.imprint","IMPRINT",FACE,{"disambiguationData":[TD([[makeQuery(id+"F6.imprint","IMPRINT",EDGE,{"disambiguationData":[TD([[subQ2,-1.0]])],"derivedFrom":subQ1}),1.0]])]});}
            var Q42;
            {var subQ0=sQuery(id+"F6.wireOp",EDGE,"E178");var subQ1=sQuery(id+"F6.wireOp",EDGE,"E147");var subQ2=makeQuery(id+"F6.imprint","INTERSECT",VERTEX,{"derivedFrom":[subQ1,subQ0]});Q42=makeQuery(id+"F6.imprint","IMPRINT",FACE,{"disambiguationData":[TD([[makeQuery(id+"F6.imprint","IMPRINT",EDGE,{"disambiguationData":[TD([[subQ2,-1.0]])],"derivedFrom":subQ1}),1.0]])]});}
            var Q43;
            {var subQ0=sQuery(id+"F6.wireOp",EDGE,"E178");var subQ1=sQuery(id+"F6.wireOp",EDGE,"E145");var subQ2=makeQuery(id+"F6.imprint","INTERSECT",VERTEX,{"derivedFrom":[subQ1,subQ0]});Q43=makeQuery(id+"F6.imprint","IMPRINT",FACE,{"disambiguationData":[TD([[makeQuery(id+"F6.imprint","IMPRINT",EDGE,{"disambiguationData":[TD([[subQ2,-1.0]])],"derivedFrom":subQ1}),1.0]])]});}
            var Q44;
            {var subQ0=sQuery(id+"F6.wireOp",EDGE,"E178");var subQ1=sQuery(id+"F6.wireOp",EDGE,"E143");var subQ2=makeQuery(id+"F6.imprint","INTERSECT",VERTEX,{"derivedFrom":[subQ1,subQ0]});Q44=makeQuery(id+"F6.imprint","IMPRINT",FACE,{"disambiguationData":[TD([[makeQuery(id+"F6.imprint","IMPRINT",EDGE,{"disambiguationData":[TD([[subQ2,-1.0]])],"derivedFrom":subQ1}),1.0]])]});}
            var Q45;
            {var subQ0=sQuery(id+"F6.wireOp",EDGE,"E178");var subQ1=sQuery(id+"F6.wireOp",EDGE,"E141");var subQ2=makeQuery(id+"F6.imprint","INTERSECT",VERTEX,{"derivedFrom":[subQ1,subQ0]});Q45=makeQuery(id+"F6.imprint","IMPRINT",FACE,{"disambiguationData":[TD([[makeQuery(id+"F6.imprint","IMPRINT",EDGE,{"disambiguationData":[TD([[subQ2,-1.0]])],"derivedFrom":subQ1}),1.0]])]});}
            var Q46;
            {var subQ0=sQuery(id+"F6.wireOp",EDGE,"E178");var subQ1=sQuery(id+"F6.wireOp",EDGE,"E139");var subQ2=makeQuery(id+"F6.imprint","INTERSECT",VERTEX,{"derivedFrom":[subQ1,subQ0]});Q46=makeQuery(id+"F6.imprint","IMPRINT",FACE,{"disambiguationData":[TD([[makeQuery(id+"F6.imprint","IMPRINT",EDGE,{"disambiguationData":[TD([[subQ2,-1.0]])],"derivedFrom":subQ1}),1.0]])]});}
            var Q47;
            {var subQ0=sQuery(id+"F6.wireOp",EDGE,"E178");var subQ1=sQuery(id+"F6.wireOp",EDGE,"E137");var subQ2=makeQuery(id+"F6.imprint","INTERSECT",VERTEX,{"derivedFrom":[subQ1,subQ0]});Q47=makeQuery(id+"F6.imprint","IMPRINT",FACE,{"disambiguationData":[TD([[makeQuery(id+"F6.imprint","IMPRINT",EDGE,{"disambiguationData":[TD([[subQ2,-1.0]])],"derivedFrom":subQ1}),1.0]])]});}
            var Q48;
            {var subQ0=sQuery(id+"F6.wireOp",EDGE,"E178");var subQ1=sQuery(id+"F6.wireOp",EDGE,"E135");var subQ2=makeQuery(id+"F6.imprint","INTERSECT",VERTEX,{"derivedFrom":[subQ1,subQ0]});Q48=makeQuery(id+"F6.imprint","IMPRINT",FACE,{"disambiguationData":[TD([[makeQuery(id+"F6.imprint","IMPRINT",EDGE,{"disambiguationData":[TD([[subQ2,-1.0]])],"derivedFrom":subQ1}),1.0]])]});}
            var Q49;
            {var subQ0=sQuery(id+"F6.wireOp",EDGE,"E180");var subQ1=sQuery(id+"F6.wireOp",EDGE,"E135");var subQ2=makeQuery(id+"F6.imprint","INTERSECT",VERTEX,{"derivedFrom":[subQ1,subQ0]});Q49=makeQuery(id+"F6.imprint","IMPRINT",FACE,{"disambiguationData":[TD([[makeQuery(id+"F6.imprint","IMPRINT",EDGE,{"disambiguationData":[TD([[subQ2,-1.0]])],"derivedFrom":subQ1}),1.0]])]});}
            var Q50;
            {var subQ0=sQuery(id+"F6.wireOp",EDGE,"E180");var subQ1=sQuery(id+"F6.wireOp",EDGE,"E137");var subQ2=makeQuery(id+"F6.imprint","INTERSECT",VERTEX,{"derivedFrom":[subQ1,subQ0]});Q50=makeQuery(id+"F6.imprint","IMPRINT",FACE,{"disambiguationData":[TD([[makeQuery(id+"F6.imprint","IMPRINT",EDGE,{"disambiguationData":[TD([[subQ2,-1.0]])],"derivedFrom":subQ1}),1.0]])]});}
            var Q51;
            {var subQ0=sQuery(id+"F6.wireOp",EDGE,"E180");var subQ1=sQuery(id+"F6.wireOp",EDGE,"E139");var subQ2=makeQuery(id+"F6.imprint","INTERSECT",VERTEX,{"derivedFrom":[subQ1,subQ0]});Q51=makeQuery(id+"F6.imprint","IMPRINT",FACE,{"disambiguationData":[TD([[makeQuery(id+"F6.imprint","IMPRINT",EDGE,{"disambiguationData":[TD([[subQ2,-1.0]])],"derivedFrom":subQ1}),1.0]])]});}
            var Q52;
            {var subQ0=sQuery(id+"F6.wireOp",EDGE,"E180");var subQ1=sQuery(id+"F6.wireOp",EDGE,"E141");var subQ2=makeQuery(id+"F6.imprint","INTERSECT",VERTEX,{"derivedFrom":[subQ1,subQ0]});Q52=makeQuery(id+"F6.imprint","IMPRINT",FACE,{"disambiguationData":[TD([[makeQuery(id+"F6.imprint","IMPRINT",EDGE,{"disambiguationData":[TD([[subQ2,-1.0]])],"derivedFrom":subQ1}),1.0]])]});}
            var Q53;
            {var subQ0=sQuery(id+"F6.wireOp",EDGE,"E180");var subQ1=sQuery(id+"F6.wireOp",EDGE,"E143");var subQ2=makeQuery(id+"F6.imprint","INTERSECT",VERTEX,{"derivedFrom":[subQ1,subQ0]});Q53=makeQuery(id+"F6.imprint","IMPRINT",FACE,{"disambiguationData":[TD([[makeQuery(id+"F6.imprint","IMPRINT",EDGE,{"disambiguationData":[TD([[subQ2,-1.0]])],"derivedFrom":subQ1}),1.0]])]});}
            var Q54;
            {var subQ0=sQuery(id+"F6.wireOp",EDGE,"E180");var subQ1=sQuery(id+"F6.wireOp",EDGE,"E145");var subQ2=makeQuery(id+"F6.imprint","INTERSECT",VERTEX,{"derivedFrom":[subQ1,subQ0]});Q54=makeQuery(id+"F6.imprint","IMPRINT",FACE,{"disambiguationData":[TD([[makeQuery(id+"F6.imprint","IMPRINT",EDGE,{"disambiguationData":[TD([[subQ2,-1.0]])],"derivedFrom":subQ1}),1.0]])]});}
            var Q55;
            {var subQ0=sQuery(id+"F6.wireOp",EDGE,"E180");var subQ1=sQuery(id+"F6.wireOp",EDGE,"E147");var subQ2=makeQuery(id+"F6.imprint","INTERSECT",VERTEX,{"derivedFrom":[subQ1,subQ0]});Q55=makeQuery(id+"F6.imprint","IMPRINT",FACE,{"disambiguationData":[TD([[makeQuery(id+"F6.imprint","IMPRINT",EDGE,{"disambiguationData":[TD([[subQ2,-1.0]])],"derivedFrom":subQ1}),1.0]])]});}
            var Q56;
            {var subQ0=sQuery(id+"F6.wireOp",EDGE,"E180");var subQ1=sQuery(id+"F6.wireOp",EDGE,"E149");var subQ2=makeQuery(id+"F6.imprint","INTERSECT",VERTEX,{"derivedFrom":[subQ1,subQ0]});Q56=makeQuery(id+"F6.imprint","IMPRINT",FACE,{"disambiguationData":[TD([[makeQuery(id+"F6.imprint","IMPRINT",EDGE,{"disambiguationData":[TD([[subQ2,-1.0]])],"derivedFrom":subQ1}),1.0]])]});}
            var Q57;
            {var subQ0=sQuery(id+"F6.wireOp",EDGE,"E180");var subQ1=sQuery(id+"F6.wireOp",EDGE,"E151");var subQ2=makeQuery(id+"F6.imprint","INTERSECT",VERTEX,{"derivedFrom":[subQ1,subQ0]});Q57=makeQuery(id+"F6.imprint","IMPRINT",FACE,{"disambiguationData":[TD([[makeQuery(id+"F6.imprint","IMPRINT",EDGE,{"disambiguationData":[TD([[subQ2,-1.0]])],"derivedFrom":subQ1}),1.0]])]});}
            var Q58;
            {var subQ0=sQuery(id+"F6.wireOp",EDGE,"E180");var subQ1=sQuery(id+"F6.wireOp",EDGE,"E153");var subQ2=makeQuery(id+"F6.imprint","INTERSECT",VERTEX,{"derivedFrom":[subQ1,subQ0]});Q58=makeQuery(id+"F6.imprint","IMPRINT",FACE,{"disambiguationData":[TD([[makeQuery(id+"F6.imprint","IMPRINT",EDGE,{"disambiguationData":[TD([[subQ2,-1.0]])],"derivedFrom":subQ1}),1.0]])]});}
            var Q59;
            {var subQ0=sQuery(id+"F6.wireOp",EDGE,"E180");var subQ1=sQuery(id+"F6.wireOp",EDGE,"E155");var subQ2=makeQuery(id+"F6.imprint","INTERSECT",VERTEX,{"derivedFrom":[subQ1,subQ0]});Q59=makeQuery(id+"F6.imprint","IMPRINT",FACE,{"disambiguationData":[TD([[makeQuery(id+"F6.imprint","IMPRINT",EDGE,{"disambiguationData":[TD([[subQ2,-1.0]])],"derivedFrom":subQ1}),1.0]])]});}
            var Q60;
            {var subQ0=sQuery(id+"F6.wireOp",EDGE,"E180");var subQ1=sQuery(id+"F6.wireOp",EDGE,"E157");var subQ2=makeQuery(id+"F6.imprint","INTERSECT",VERTEX,{"derivedFrom":[subQ1,subQ0]});Q60=makeQuery(id+"F6.imprint","IMPRINT",FACE,{"disambiguationData":[TD([[makeQuery(id+"F6.imprint","IMPRINT",EDGE,{"disambiguationData":[TD([[subQ2,-1.0]])],"derivedFrom":subQ1}),1.0]])]});}
            var Q61;
            {var subQ0=sQuery(id+"F6.wireOp",EDGE,"E180");var subQ1=sQuery(id+"F6.wireOp",EDGE,"E159");var subQ2=makeQuery(id+"F6.imprint","INTERSECT",VERTEX,{"derivedFrom":[subQ1,subQ0]});Q61=makeQuery(id+"F6.imprint","IMPRINT",FACE,{"disambiguationData":[TD([[makeQuery(id+"F6.imprint","IMPRINT",EDGE,{"disambiguationData":[TD([[subQ2,-1.0]])],"derivedFrom":subQ1}),1.0]])]});}
            var Q62;
            {var subQ0=sQuery(id+"F6.wireOp",EDGE,"E180");var subQ1=sQuery(id+"F6.wireOp",EDGE,"E161");var subQ2=makeQuery(id+"F6.imprint","INTERSECT",VERTEX,{"derivedFrom":[subQ1,subQ0]});Q62=makeQuery(id+"F6.imprint","IMPRINT",FACE,{"disambiguationData":[TD([[makeQuery(id+"F6.imprint","IMPRINT",EDGE,{"disambiguationData":[TD([[subQ2,-1.0]])],"derivedFrom":subQ1}),1.0]])]});}
            var Q63;
            {var subQ0=sQuery(id+"F6.wireOp",EDGE,"E180");var subQ1=sQuery(id+"F6.wireOp",EDGE,"E163");var subQ2=makeQuery(id+"F6.imprint","INTERSECT",VERTEX,{"derivedFrom":[subQ1,subQ0]});Q63=makeQuery(id+"F6.imprint","IMPRINT",FACE,{"disambiguationData":[TD([[makeQuery(id+"F6.imprint","IMPRINT",EDGE,{"disambiguationData":[TD([[subQ2,-1.0]])],"derivedFrom":subQ1}),1.0]])]});}
            var Q64;
            {var subQ0=sQuery(id+"F6.wireOp",EDGE,"E180");var subQ1=sQuery(id+"F6.wireOp",EDGE,"E165");var subQ2=makeQuery(id+"F6.imprint","INTERSECT",VERTEX,{"derivedFrom":[subQ1,subQ0]});Q64=makeQuery(id+"F6.imprint","IMPRINT",FACE,{"disambiguationData":[TD([[makeQuery(id+"F6.imprint","IMPRINT",EDGE,{"disambiguationData":[TD([[subQ2,-1.0]])],"derivedFrom":subQ1}),1.0]])]});}
            var Q65;
            {var subQ0=sQuery(id+"F6.wireOp",EDGE,"E182");var subQ1=sQuery(id+"F6.wireOp",EDGE,"E169");var subQ2=makeQuery(id+"F6.imprint","INTERSECT",VERTEX,{"derivedFrom":[subQ1,subQ0]});Q65=makeQuery(id+"F6.imprint","IMPRINT",FACE,{"disambiguationData":[TD([[makeQuery(id+"F6.imprint","IMPRINT",EDGE,{"disambiguationData":[TD([[subQ2,-1.0]])],"derivedFrom":subQ1}),1.0]])]});}
            var Q66;
            {var subQ0=sQuery(id+"F6.wireOp",EDGE,"E180");var subQ1=sQuery(id+"F6.wireOp",EDGE,"E169");var subQ2=makeQuery(id+"F6.imprint","INTERSECT",VERTEX,{"derivedFrom":[subQ1,subQ0]});Q66=makeQuery(id+"F6.imprint","IMPRINT",FACE,{"disambiguationData":[TD([[makeQuery(id+"F6.imprint","IMPRINT",EDGE,{"disambiguationData":[TD([[subQ2,-1.0]])],"derivedFrom":subQ1}),1.0]])]});}
            var Q67;
            {var subQ0=sQuery(id+"F6.wireOp",EDGE,"E182");var subQ1=sQuery(id+"F6.wireOp",EDGE,"E165");var subQ2=makeQuery(id+"F6.imprint","INTERSECT",VERTEX,{"derivedFrom":[subQ1,subQ0]});Q67=makeQuery(id+"F6.imprint","IMPRINT",FACE,{"disambiguationData":[TD([[makeQuery(id+"F6.imprint","IMPRINT",EDGE,{"disambiguationData":[TD([[subQ2,-1.0]])],"derivedFrom":subQ1}),1.0]])]});}
            var Q68;
            {var subQ0=sQuery(id+"F6.wireOp",EDGE,"E182");var subQ1=sQuery(id+"F6.wireOp",EDGE,"E163");var subQ2=makeQuery(id+"F6.imprint","INTERSECT",VERTEX,{"derivedFrom":[subQ1,subQ0]});Q68=makeQuery(id+"F6.imprint","IMPRINT",FACE,{"disambiguationData":[TD([[makeQuery(id+"F6.imprint","IMPRINT",EDGE,{"disambiguationData":[TD([[subQ2,-1.0]])],"derivedFrom":subQ1}),1.0]])]});}
            var Q69;
            {var subQ0=sQuery(id+"F6.wireOp",EDGE,"E182");var subQ1=sQuery(id+"F6.wireOp",EDGE,"E161");var subQ2=makeQuery(id+"F6.imprint","INTERSECT",VERTEX,{"derivedFrom":[subQ1,subQ0]});Q69=makeQuery(id+"F6.imprint","IMPRINT",FACE,{"disambiguationData":[TD([[makeQuery(id+"F6.imprint","IMPRINT",EDGE,{"disambiguationData":[TD([[subQ2,-1.0]])],"derivedFrom":subQ1}),1.0]])]});}
            var Q70;
            {var subQ0=sQuery(id+"F6.wireOp",EDGE,"E182");var subQ1=sQuery(id+"F6.wireOp",EDGE,"E159");var subQ2=makeQuery(id+"F6.imprint","INTERSECT",VERTEX,{"derivedFrom":[subQ1,subQ0]});Q70=makeQuery(id+"F6.imprint","IMPRINT",FACE,{"disambiguationData":[TD([[makeQuery(id+"F6.imprint","IMPRINT",EDGE,{"disambiguationData":[TD([[subQ2,-1.0]])],"derivedFrom":subQ1}),1.0]])]});}
            var Q71;
            {var subQ0=sQuery(id+"F6.wireOp",EDGE,"E182");var subQ1=sQuery(id+"F6.wireOp",EDGE,"E157");var subQ2=makeQuery(id+"F6.imprint","INTERSECT",VERTEX,{"derivedFrom":[subQ1,subQ0]});Q71=makeQuery(id+"F6.imprint","IMPRINT",FACE,{"disambiguationData":[TD([[makeQuery(id+"F6.imprint","IMPRINT",EDGE,{"disambiguationData":[TD([[subQ2,-1.0]])],"derivedFrom":subQ1}),1.0]])]});}
            var Q72;
            {var subQ0=sQuery(id+"F6.wireOp",EDGE,"E182");var subQ1=sQuery(id+"F6.wireOp",EDGE,"E155");var subQ2=makeQuery(id+"F6.imprint","INTERSECT",VERTEX,{"derivedFrom":[subQ1,subQ0]});Q72=makeQuery(id+"F6.imprint","IMPRINT",FACE,{"disambiguationData":[TD([[makeQuery(id+"F6.imprint","IMPRINT",EDGE,{"disambiguationData":[TD([[subQ2,-1.0]])],"derivedFrom":subQ1}),1.0]])]});}
            var Q73;
            {var subQ0=sQuery(id+"F6.wireOp",EDGE,"E182");var subQ1=sQuery(id+"F6.wireOp",EDGE,"E153");var subQ2=makeQuery(id+"F6.imprint","INTERSECT",VERTEX,{"derivedFrom":[subQ1,subQ0]});Q73=makeQuery(id+"F6.imprint","IMPRINT",FACE,{"disambiguationData":[TD([[makeQuery(id+"F6.imprint","IMPRINT",EDGE,{"disambiguationData":[TD([[subQ2,-1.0]])],"derivedFrom":subQ1}),1.0]])]});}
            var Q74;
            {var subQ0=sQuery(id+"F6.wireOp",EDGE,"E182");var subQ1=sQuery(id+"F6.wireOp",EDGE,"E151");var subQ2=makeQuery(id+"F6.imprint","INTERSECT",VERTEX,{"derivedFrom":[subQ1,subQ0]});Q74=makeQuery(id+"F6.imprint","IMPRINT",FACE,{"disambiguationData":[TD([[makeQuery(id+"F6.imprint","IMPRINT",EDGE,{"disambiguationData":[TD([[subQ2,-1.0]])],"derivedFrom":subQ1}),1.0]])]});}
            var Q75;
            {var subQ0=sQuery(id+"F6.wireOp",EDGE,"E182");var subQ1=sQuery(id+"F6.wireOp",EDGE,"E149");var subQ2=makeQuery(id+"F6.imprint","INTERSECT",VERTEX,{"derivedFrom":[subQ1,subQ0]});Q75=makeQuery(id+"F6.imprint","IMPRINT",FACE,{"disambiguationData":[TD([[makeQuery(id+"F6.imprint","IMPRINT",EDGE,{"disambiguationData":[TD([[subQ2,-1.0]])],"derivedFrom":subQ1}),1.0]])]});}
            var Q76;
            {var subQ0=sQuery(id+"F6.wireOp",EDGE,"E182");var subQ1=sQuery(id+"F6.wireOp",EDGE,"E147");var subQ2=makeQuery(id+"F6.imprint","INTERSECT",VERTEX,{"derivedFrom":[subQ1,subQ0]});Q76=makeQuery(id+"F6.imprint","IMPRINT",FACE,{"disambiguationData":[TD([[makeQuery(id+"F6.imprint","IMPRINT",EDGE,{"disambiguationData":[TD([[subQ2,-1.0]])],"derivedFrom":subQ1}),1.0]])]});}
            var Q77;
            {var subQ0=sQuery(id+"F6.wireOp",EDGE,"E182");var subQ1=sQuery(id+"F6.wireOp",EDGE,"E145");var subQ2=makeQuery(id+"F6.imprint","INTERSECT",VERTEX,{"derivedFrom":[subQ1,subQ0]});Q77=makeQuery(id+"F6.imprint","IMPRINT",FACE,{"disambiguationData":[TD([[makeQuery(id+"F6.imprint","IMPRINT",EDGE,{"disambiguationData":[TD([[subQ2,-1.0]])],"derivedFrom":subQ1}),1.0]])]});}
            var Q78;
            {var subQ0=sQuery(id+"F6.wireOp",EDGE,"E182");var subQ1=sQuery(id+"F6.wireOp",EDGE,"E143");var subQ2=makeQuery(id+"F6.imprint","INTERSECT",VERTEX,{"derivedFrom":[subQ1,subQ0]});Q78=makeQuery(id+"F6.imprint","IMPRINT",FACE,{"disambiguationData":[TD([[makeQuery(id+"F6.imprint","IMPRINT",EDGE,{"disambiguationData":[TD([[subQ2,-1.0]])],"derivedFrom":subQ1}),1.0]])]});}
            var Q79;
            {var subQ0=sQuery(id+"F6.wireOp",EDGE,"E182");var subQ1=sQuery(id+"F6.wireOp",EDGE,"E141");var subQ2=makeQuery(id+"F6.imprint","INTERSECT",VERTEX,{"derivedFrom":[subQ1,subQ0]});Q79=makeQuery(id+"F6.imprint","IMPRINT",FACE,{"disambiguationData":[TD([[makeQuery(id+"F6.imprint","IMPRINT",EDGE,{"disambiguationData":[TD([[subQ2,-1.0]])],"derivedFrom":subQ1}),1.0]])]});}
            var Q80;
            {var subQ0=sQuery(id+"F6.wireOp",EDGE,"E182");var subQ1=sQuery(id+"F6.wireOp",EDGE,"E139");var subQ2=makeQuery(id+"F6.imprint","INTERSECT",VERTEX,{"derivedFrom":[subQ1,subQ0]});Q80=makeQuery(id+"F6.imprint","IMPRINT",FACE,{"disambiguationData":[TD([[makeQuery(id+"F6.imprint","IMPRINT",EDGE,{"disambiguationData":[TD([[subQ2,-1.0]])],"derivedFrom":subQ1}),1.0]])]});}
            var Q81;
            {var subQ0=sQuery(id+"F6.wireOp",EDGE,"E182");var subQ1=sQuery(id+"F6.wireOp",EDGE,"E137");var subQ2=makeQuery(id+"F6.imprint","INTERSECT",VERTEX,{"derivedFrom":[subQ1,subQ0]});Q81=makeQuery(id+"F6.imprint","IMPRINT",FACE,{"disambiguationData":[TD([[makeQuery(id+"F6.imprint","IMPRINT",EDGE,{"disambiguationData":[TD([[subQ2,-1.0]])],"derivedFrom":subQ1}),1.0]])]});}
            var Q82;
            {var subQ0=sQuery(id+"F6.wireOp",EDGE,"E182");var subQ1=sQuery(id+"F6.wireOp",EDGE,"E135");var subQ2=makeQuery(id+"F6.imprint","INTERSECT",VERTEX,{"derivedFrom":[subQ1,subQ0]});Q82=makeQuery(id+"F6.imprint","IMPRINT",FACE,{"disambiguationData":[TD([[makeQuery(id+"F6.imprint","IMPRINT",EDGE,{"disambiguationData":[TD([[subQ2,-1.0]])],"derivedFrom":subQ1}),1.0]])]});}
            var Q83;
            {var subQ0=sQuery(id+"F6.wireOp",EDGE,"E184");var subQ1=sQuery(id+"F6.wireOp",EDGE,"E135");var subQ2=makeQuery(id+"F6.imprint","INTERSECT",VERTEX,{"derivedFrom":[subQ1,subQ0]});Q83=makeQuery(id+"F6.imprint","IMPRINT",FACE,{"disambiguationData":[TD([[makeQuery(id+"F6.imprint","IMPRINT",EDGE,{"disambiguationData":[TD([[subQ2,-1.0]])],"derivedFrom":subQ1}),1.0]])]});}
            var Q84;
            {var subQ0=sQuery(id+"F6.wireOp",EDGE,"E184");var subQ1=sQuery(id+"F6.wireOp",EDGE,"E137");var subQ2=makeQuery(id+"F6.imprint","INTERSECT",VERTEX,{"derivedFrom":[subQ1,subQ0]});Q84=makeQuery(id+"F6.imprint","IMPRINT",FACE,{"disambiguationData":[TD([[makeQuery(id+"F6.imprint","IMPRINT",EDGE,{"disambiguationData":[TD([[subQ2,-1.0]])],"derivedFrom":subQ1}),1.0]])]});}
            var Q85;
            {var subQ0=sQuery(id+"F6.wireOp",EDGE,"E184");var subQ1=sQuery(id+"F6.wireOp",EDGE,"E139");var subQ2=makeQuery(id+"F6.imprint","INTERSECT",VERTEX,{"derivedFrom":[subQ1,subQ0]});Q85=makeQuery(id+"F6.imprint","IMPRINT",FACE,{"disambiguationData":[TD([[makeQuery(id+"F6.imprint","IMPRINT",EDGE,{"disambiguationData":[TD([[subQ2,-1.0]])],"derivedFrom":subQ1}),1.0]])]});}
            var Q86;
            {var subQ0=sQuery(id+"F6.wireOp",EDGE,"E184");var subQ1=sQuery(id+"F6.wireOp",EDGE,"E141");var subQ2=makeQuery(id+"F6.imprint","INTERSECT",VERTEX,{"derivedFrom":[subQ1,subQ0]});Q86=makeQuery(id+"F6.imprint","IMPRINT",FACE,{"disambiguationData":[TD([[makeQuery(id+"F6.imprint","IMPRINT",EDGE,{"disambiguationData":[TD([[subQ2,-1.0]])],"derivedFrom":subQ1}),1.0]])]});}
            var Q87;
            {var subQ0=sQuery(id+"F6.wireOp",EDGE,"E184");var subQ1=sQuery(id+"F6.wireOp",EDGE,"E143");var subQ2=makeQuery(id+"F6.imprint","INTERSECT",VERTEX,{"derivedFrom":[subQ1,subQ0]});Q87=makeQuery(id+"F6.imprint","IMPRINT",FACE,{"disambiguationData":[TD([[makeQuery(id+"F6.imprint","IMPRINT",EDGE,{"disambiguationData":[TD([[subQ2,-1.0]])],"derivedFrom":subQ1}),1.0]])]});}
            var Q88;
            {var subQ0=sQuery(id+"F6.wireOp",EDGE,"E184");var subQ1=sQuery(id+"F6.wireOp",EDGE,"E145");var subQ2=makeQuery(id+"F6.imprint","INTERSECT",VERTEX,{"derivedFrom":[subQ1,subQ0]});Q88=makeQuery(id+"F6.imprint","IMPRINT",FACE,{"disambiguationData":[TD([[makeQuery(id+"F6.imprint","IMPRINT",EDGE,{"disambiguationData":[TD([[subQ2,-1.0]])],"derivedFrom":subQ1}),1.0]])]});}
            var Q89;
            {var subQ0=sQuery(id+"F6.wireOp",EDGE,"E184");var subQ1=sQuery(id+"F6.wireOp",EDGE,"E147");var subQ2=makeQuery(id+"F6.imprint","INTERSECT",VERTEX,{"derivedFrom":[subQ1,subQ0]});Q89=makeQuery(id+"F6.imprint","IMPRINT",FACE,{"disambiguationData":[TD([[makeQuery(id+"F6.imprint","IMPRINT",EDGE,{"disambiguationData":[TD([[subQ2,-1.0]])],"derivedFrom":subQ1}),1.0]])]});}
            var Q90;
            {var subQ0=sQuery(id+"F6.wireOp",EDGE,"E184");var subQ1=sQuery(id+"F6.wireOp",EDGE,"E149");var subQ2=makeQuery(id+"F6.imprint","INTERSECT",VERTEX,{"derivedFrom":[subQ1,subQ0]});Q90=makeQuery(id+"F6.imprint","IMPRINT",FACE,{"disambiguationData":[TD([[makeQuery(id+"F6.imprint","IMPRINT",EDGE,{"disambiguationData":[TD([[subQ2,-1.0]])],"derivedFrom":subQ1}),1.0]])]});}
            var Q91;
            {var subQ0=sQuery(id+"F6.wireOp",EDGE,"E184");var subQ1=sQuery(id+"F6.wireOp",EDGE,"E151");var subQ2=makeQuery(id+"F6.imprint","INTERSECT",VERTEX,{"derivedFrom":[subQ1,subQ0]});Q91=makeQuery(id+"F6.imprint","IMPRINT",FACE,{"disambiguationData":[TD([[makeQuery(id+"F6.imprint","IMPRINT",EDGE,{"disambiguationData":[TD([[subQ2,-1.0]])],"derivedFrom":subQ1}),1.0]])]});}
            var Q92;
            {var subQ0=sQuery(id+"F6.wireOp",EDGE,"E184");var subQ1=sQuery(id+"F6.wireOp",EDGE,"E153");var subQ2=makeQuery(id+"F6.imprint","INTERSECT",VERTEX,{"derivedFrom":[subQ1,subQ0]});Q92=makeQuery(id+"F6.imprint","IMPRINT",FACE,{"disambiguationData":[TD([[makeQuery(id+"F6.imprint","IMPRINT",EDGE,{"disambiguationData":[TD([[subQ2,-1.0]])],"derivedFrom":subQ1}),1.0]])]});}
            var Q93;
            {var subQ0=sQuery(id+"F6.wireOp",EDGE,"E184");var subQ1=sQuery(id+"F6.wireOp",EDGE,"E155");var subQ2=makeQuery(id+"F6.imprint","INTERSECT",VERTEX,{"derivedFrom":[subQ1,subQ0]});Q93=makeQuery(id+"F6.imprint","IMPRINT",FACE,{"disambiguationData":[TD([[makeQuery(id+"F6.imprint","IMPRINT",EDGE,{"disambiguationData":[TD([[subQ2,-1.0]])],"derivedFrom":subQ1}),1.0]])]});}
            var Q94;
            {var subQ0=sQuery(id+"F6.wireOp",EDGE,"E184");var subQ1=sQuery(id+"F6.wireOp",EDGE,"E157");var subQ2=makeQuery(id+"F6.imprint","INTERSECT",VERTEX,{"derivedFrom":[subQ1,subQ0]});Q94=makeQuery(id+"F6.imprint","IMPRINT",FACE,{"disambiguationData":[TD([[makeQuery(id+"F6.imprint","IMPRINT",EDGE,{"disambiguationData":[TD([[subQ2,-1.0]])],"derivedFrom":subQ1}),1.0]])]});}
            var Q95;
            {var subQ0=sQuery(id+"F6.wireOp",EDGE,"E184");var subQ1=sQuery(id+"F6.wireOp",EDGE,"E159");var subQ2=makeQuery(id+"F6.imprint","INTERSECT",VERTEX,{"derivedFrom":[subQ1,subQ0]});Q95=makeQuery(id+"F6.imprint","IMPRINT",FACE,{"disambiguationData":[TD([[makeQuery(id+"F6.imprint","IMPRINT",EDGE,{"disambiguationData":[TD([[subQ2,-1.0]])],"derivedFrom":subQ1}),1.0]])]});}
            var Q96;
            {var subQ0=sQuery(id+"F6.wireOp",EDGE,"E184");var subQ1=sQuery(id+"F6.wireOp",EDGE,"E161");var subQ2=makeQuery(id+"F6.imprint","INTERSECT",VERTEX,{"derivedFrom":[subQ1,subQ0]});Q96=makeQuery(id+"F6.imprint","IMPRINT",FACE,{"disambiguationData":[TD([[makeQuery(id+"F6.imprint","IMPRINT",EDGE,{"disambiguationData":[TD([[subQ2,-1.0]])],"derivedFrom":subQ1}),1.0]])]});}
            var Q97;
            {var subQ0=sQuery(id+"F6.wireOp",EDGE,"E184");var subQ1=sQuery(id+"F6.wireOp",EDGE,"E163");var subQ2=makeQuery(id+"F6.imprint","INTERSECT",VERTEX,{"derivedFrom":[subQ1,subQ0]});Q97=makeQuery(id+"F6.imprint","IMPRINT",FACE,{"disambiguationData":[TD([[makeQuery(id+"F6.imprint","IMPRINT",EDGE,{"disambiguationData":[TD([[subQ2,-1.0]])],"derivedFrom":subQ1}),1.0]])]});}
            var Q98;
            {var subQ0=sQuery(id+"F6.wireOp",EDGE,"E184");var subQ1=sQuery(id+"F6.wireOp",EDGE,"E165");var subQ2=makeQuery(id+"F6.imprint","INTERSECT",VERTEX,{"derivedFrom":[subQ1,subQ0]});Q98=makeQuery(id+"F6.imprint","IMPRINT",FACE,{"disambiguationData":[TD([[makeQuery(id+"F6.imprint","IMPRINT",EDGE,{"disambiguationData":[TD([[subQ2,-1.0]])],"derivedFrom":subQ1}),1.0]])]});}
            var Q99;
            {var subQ0=sQuery(id+"F6.wireOp",EDGE,"E184");var subQ1=sQuery(id+"F6.wireOp",EDGE,"E169");var subQ2=makeQuery(id+"F6.imprint","INTERSECT",VERTEX,{"derivedFrom":[subQ1,subQ0]});Q99=makeQuery(id+"F6.imprint","IMPRINT",FACE,{"disambiguationData":[TD([[makeQuery(id+"F6.imprint","IMPRINT",EDGE,{"disambiguationData":[TD([[subQ2,-1.0]])],"derivedFrom":subQ1}),1.0]])]});}
            var Q100;
            {var subQ0=sQuery(id+"F6.wireOp",EDGE,"E186");var subQ1=sQuery(id+"F6.wireOp",EDGE,"E169");var subQ2=makeQuery(id+"F6.imprint","INTERSECT",VERTEX,{"derivedFrom":[subQ1,subQ0]});Q100=makeQuery(id+"F6.imprint","IMPRINT",FACE,{"disambiguationData":[TD([[makeQuery(id+"F6.imprint","IMPRINT",EDGE,{"disambiguationData":[TD([[subQ2,-1.0]])],"derivedFrom":subQ1}),1.0]])]});}
            var Q101;
            {var subQ0=sQuery(id+"F6.wireOp",EDGE,"E186");var subQ1=sQuery(id+"F6.wireOp",EDGE,"E165");var subQ2=makeQuery(id+"F6.imprint","INTERSECT",VERTEX,{"derivedFrom":[subQ1,subQ0]});Q101=makeQuery(id+"F6.imprint","IMPRINT",FACE,{"disambiguationData":[TD([[makeQuery(id+"F6.imprint","IMPRINT",EDGE,{"disambiguationData":[TD([[subQ2,-1.0]])],"derivedFrom":subQ1}),1.0]])]});}
            var Q102;
            {var subQ0=sQuery(id+"F6.wireOp",EDGE,"E186");var subQ1=sQuery(id+"F6.wireOp",EDGE,"E163");var subQ2=makeQuery(id+"F6.imprint","INTERSECT",VERTEX,{"derivedFrom":[subQ1,subQ0]});Q102=makeQuery(id+"F6.imprint","IMPRINT",FACE,{"disambiguationData":[TD([[makeQuery(id+"F6.imprint","IMPRINT",EDGE,{"disambiguationData":[TD([[subQ2,-1.0]])],"derivedFrom":subQ1}),1.0]])]});}
            var Q103;
            {var subQ0=sQuery(id+"F6.wireOp",EDGE,"E186");var subQ1=sQuery(id+"F6.wireOp",EDGE,"E161");var subQ2=makeQuery(id+"F6.imprint","INTERSECT",VERTEX,{"derivedFrom":[subQ1,subQ0]});Q103=makeQuery(id+"F6.imprint","IMPRINT",FACE,{"disambiguationData":[TD([[makeQuery(id+"F6.imprint","IMPRINT",EDGE,{"disambiguationData":[TD([[subQ2,-1.0]])],"derivedFrom":subQ1}),1.0]])]});}
            var Q104;
            {var subQ0=sQuery(id+"F6.wireOp",EDGE,"E186");var subQ1=sQuery(id+"F6.wireOp",EDGE,"E159");var subQ2=makeQuery(id+"F6.imprint","INTERSECT",VERTEX,{"derivedFrom":[subQ1,subQ0]});Q104=makeQuery(id+"F6.imprint","IMPRINT",FACE,{"disambiguationData":[TD([[makeQuery(id+"F6.imprint","IMPRINT",EDGE,{"disambiguationData":[TD([[subQ2,-1.0]])],"derivedFrom":subQ1}),1.0]])]});}
            var Q105;
            {var subQ0=sQuery(id+"F6.wireOp",EDGE,"E186");var subQ1=sQuery(id+"F6.wireOp",EDGE,"E157");var subQ2=makeQuery(id+"F6.imprint","INTERSECT",VERTEX,{"derivedFrom":[subQ1,subQ0]});Q105=makeQuery(id+"F6.imprint","IMPRINT",FACE,{"disambiguationData":[TD([[makeQuery(id+"F6.imprint","IMPRINT",EDGE,{"disambiguationData":[TD([[subQ2,-1.0]])],"derivedFrom":subQ1}),1.0]])]});}
            var Q106;
            {var subQ0=sQuery(id+"F6.wireOp",EDGE,"E186");var subQ1=sQuery(id+"F6.wireOp",EDGE,"E155");var subQ2=makeQuery(id+"F6.imprint","INTERSECT",VERTEX,{"derivedFrom":[subQ1,subQ0]});Q106=makeQuery(id+"F6.imprint","IMPRINT",FACE,{"disambiguationData":[TD([[makeQuery(id+"F6.imprint","IMPRINT",EDGE,{"disambiguationData":[TD([[subQ2,-1.0]])],"derivedFrom":subQ1}),1.0]])]});}
            var Q107;
            {var subQ0=sQuery(id+"F6.wireOp",EDGE,"E186");var subQ1=sQuery(id+"F6.wireOp",EDGE,"E153");var subQ2=makeQuery(id+"F6.imprint","INTERSECT",VERTEX,{"derivedFrom":[subQ1,subQ0]});Q107=makeQuery(id+"F6.imprint","IMPRINT",FACE,{"disambiguationData":[TD([[makeQuery(id+"F6.imprint","IMPRINT",EDGE,{"disambiguationData":[TD([[subQ2,-1.0]])],"derivedFrom":subQ1}),1.0]])]});}
            var Q108;
            {var subQ0=sQuery(id+"F6.wireOp",EDGE,"E186");var subQ1=sQuery(id+"F6.wireOp",EDGE,"E151");var subQ2=makeQuery(id+"F6.imprint","INTERSECT",VERTEX,{"derivedFrom":[subQ1,subQ0]});Q108=makeQuery(id+"F6.imprint","IMPRINT",FACE,{"disambiguationData":[TD([[makeQuery(id+"F6.imprint","IMPRINT",EDGE,{"disambiguationData":[TD([[subQ2,-1.0]])],"derivedFrom":subQ1}),1.0]])]});}
            var Q109;
            {var subQ0=sQuery(id+"F6.wireOp",EDGE,"E186");var subQ1=sQuery(id+"F6.wireOp",EDGE,"E149");var subQ2=makeQuery(id+"F6.imprint","INTERSECT",VERTEX,{"derivedFrom":[subQ1,subQ0]});Q109=makeQuery(id+"F6.imprint","IMPRINT",FACE,{"disambiguationData":[TD([[makeQuery(id+"F6.imprint","IMPRINT",EDGE,{"disambiguationData":[TD([[subQ2,-1.0]])],"derivedFrom":subQ1}),1.0]])]});}
            var Q110;
            {var subQ0=sQuery(id+"F6.wireOp",EDGE,"E186");var subQ1=sQuery(id+"F6.wireOp",EDGE,"E147");var subQ2=makeQuery(id+"F6.imprint","INTERSECT",VERTEX,{"derivedFrom":[subQ1,subQ0]});Q110=makeQuery(id+"F6.imprint","IMPRINT",FACE,{"disambiguationData":[TD([[makeQuery(id+"F6.imprint","IMPRINT",EDGE,{"disambiguationData":[TD([[subQ2,-1.0]])],"derivedFrom":subQ1}),1.0]])]});}
            var Q111;
            {var subQ0=sQuery(id+"F6.wireOp",EDGE,"E186");var subQ1=sQuery(id+"F6.wireOp",EDGE,"E145");var subQ2=makeQuery(id+"F6.imprint","INTERSECT",VERTEX,{"derivedFrom":[subQ1,subQ0]});Q111=makeQuery(id+"F6.imprint","IMPRINT",FACE,{"disambiguationData":[TD([[makeQuery(id+"F6.imprint","IMPRINT",EDGE,{"disambiguationData":[TD([[subQ2,-1.0]])],"derivedFrom":subQ1}),1.0]])]});}
            var Q112;
            {var subQ0=sQuery(id+"F6.wireOp",EDGE,"E186");var subQ1=sQuery(id+"F6.wireOp",EDGE,"E143");var subQ2=makeQuery(id+"F6.imprint","INTERSECT",VERTEX,{"derivedFrom":[subQ1,subQ0]});Q112=makeQuery(id+"F6.imprint","IMPRINT",FACE,{"disambiguationData":[TD([[makeQuery(id+"F6.imprint","IMPRINT",EDGE,{"disambiguationData":[TD([[subQ2,-1.0]])],"derivedFrom":subQ1}),1.0]])]});}
            var Q113;
            {var subQ0=sQuery(id+"F6.wireOp",EDGE,"E186");var subQ1=sQuery(id+"F6.wireOp",EDGE,"E141");var subQ2=makeQuery(id+"F6.imprint","INTERSECT",VERTEX,{"derivedFrom":[subQ1,subQ0]});Q113=makeQuery(id+"F6.imprint","IMPRINT",FACE,{"disambiguationData":[TD([[makeQuery(id+"F6.imprint","IMPRINT",EDGE,{"disambiguationData":[TD([[subQ2,-1.0]])],"derivedFrom":subQ1}),1.0]])]});}
            var Q114;
            {var subQ0=sQuery(id+"F6.wireOp",EDGE,"E186");var subQ1=sQuery(id+"F6.wireOp",EDGE,"E139");var subQ2=makeQuery(id+"F6.imprint","INTERSECT",VERTEX,{"derivedFrom":[subQ1,subQ0]});Q114=makeQuery(id+"F6.imprint","IMPRINT",FACE,{"disambiguationData":[TD([[makeQuery(id+"F6.imprint","IMPRINT",EDGE,{"disambiguationData":[TD([[subQ2,-1.0]])],"derivedFrom":subQ1}),1.0]])]});}
            var Q115;
            {var subQ0=sQuery(id+"F6.wireOp",EDGE,"E186");var subQ1=sQuery(id+"F6.wireOp",EDGE,"E137");var subQ2=makeQuery(id+"F6.imprint","INTERSECT",VERTEX,{"derivedFrom":[subQ1,subQ0]});Q115=makeQuery(id+"F6.imprint","IMPRINT",FACE,{"disambiguationData":[TD([[makeQuery(id+"F6.imprint","IMPRINT",EDGE,{"disambiguationData":[TD([[subQ2,-1.0]])],"derivedFrom":subQ1}),1.0]])]});}
            var Q116;
            {var subQ0=sQuery(id+"F6.wireOp",EDGE,"E186");var subQ1=sQuery(id+"F6.wireOp",EDGE,"E135");var subQ2=makeQuery(id+"F6.imprint","INTERSECT",VERTEX,{"derivedFrom":[subQ1,subQ0]});Q116=makeQuery(id+"F6.imprint","IMPRINT",FACE,{"disambiguationData":[TD([[makeQuery(id+"F6.imprint","IMPRINT",EDGE,{"disambiguationData":[TD([[subQ2,-1.0]])],"derivedFrom":subQ1}),1.0]])]});}
            var Q117;
            {var subQ0=sQuery(id+"F6.wireOp",EDGE,"E188");var subQ1=sQuery(id+"F6.wireOp",EDGE,"E135");var subQ2=makeQuery(id+"F6.imprint","INTERSECT",VERTEX,{"derivedFrom":[subQ1,subQ0]});Q117=makeQuery(id+"F6.imprint","IMPRINT",FACE,{"disambiguationData":[TD([[makeQuery(id+"F6.imprint","IMPRINT",EDGE,{"disambiguationData":[TD([[subQ2,-1.0]])],"derivedFrom":subQ1}),1.0]])]});}
            var Q118;
            {var subQ0=sQuery(id+"F6.wireOp",EDGE,"E188");var subQ1=sQuery(id+"F6.wireOp",EDGE,"E137");var subQ2=makeQuery(id+"F6.imprint","INTERSECT",VERTEX,{"derivedFrom":[subQ1,subQ0]});Q118=makeQuery(id+"F6.imprint","IMPRINT",FACE,{"disambiguationData":[TD([[makeQuery(id+"F6.imprint","IMPRINT",EDGE,{"disambiguationData":[TD([[subQ2,-1.0]])],"derivedFrom":subQ1}),1.0]])]});}
            var Q119;
            {var subQ0=sQuery(id+"F6.wireOp",EDGE,"E188");var subQ1=sQuery(id+"F6.wireOp",EDGE,"E139");var subQ2=makeQuery(id+"F6.imprint","INTERSECT",VERTEX,{"derivedFrom":[subQ1,subQ0]});Q119=makeQuery(id+"F6.imprint","IMPRINT",FACE,{"disambiguationData":[TD([[makeQuery(id+"F6.imprint","IMPRINT",EDGE,{"disambiguationData":[TD([[subQ2,-1.0]])],"derivedFrom":subQ1}),1.0]])]});}
            var Q120;
            {var subQ0=sQuery(id+"F6.wireOp",EDGE,"E188");var subQ1=sQuery(id+"F6.wireOp",EDGE,"E141");var subQ2=makeQuery(id+"F6.imprint","INTERSECT",VERTEX,{"derivedFrom":[subQ1,subQ0]});Q120=makeQuery(id+"F6.imprint","IMPRINT",FACE,{"disambiguationData":[TD([[makeQuery(id+"F6.imprint","IMPRINT",EDGE,{"disambiguationData":[TD([[subQ2,-1.0]])],"derivedFrom":subQ1}),1.0]])]});}
            var Q121;
            {var subQ0=sQuery(id+"F6.wireOp",EDGE,"E188");var subQ1=sQuery(id+"F6.wireOp",EDGE,"E143");var subQ2=makeQuery(id+"F6.imprint","INTERSECT",VERTEX,{"derivedFrom":[subQ1,subQ0]});Q121=makeQuery(id+"F6.imprint","IMPRINT",FACE,{"disambiguationData":[TD([[makeQuery(id+"F6.imprint","IMPRINT",EDGE,{"disambiguationData":[TD([[subQ2,-1.0]])],"derivedFrom":subQ1}),1.0]])]});}
            var Q122;
            {var subQ0=sQuery(id+"F6.wireOp",EDGE,"E188");var subQ1=sQuery(id+"F6.wireOp",EDGE,"E145");var subQ2=makeQuery(id+"F6.imprint","INTERSECT",VERTEX,{"derivedFrom":[subQ1,subQ0]});Q122=makeQuery(id+"F6.imprint","IMPRINT",FACE,{"disambiguationData":[TD([[makeQuery(id+"F6.imprint","IMPRINT",EDGE,{"disambiguationData":[TD([[subQ2,-1.0]])],"derivedFrom":subQ1}),1.0]])]});}
            var Q123;
            {var subQ0=sQuery(id+"F6.wireOp",EDGE,"E188");var subQ1=sQuery(id+"F6.wireOp",EDGE,"E147");var subQ2=makeQuery(id+"F6.imprint","INTERSECT",VERTEX,{"derivedFrom":[subQ1,subQ0]});Q123=makeQuery(id+"F6.imprint","IMPRINT",FACE,{"disambiguationData":[TD([[makeQuery(id+"F6.imprint","IMPRINT",EDGE,{"disambiguationData":[TD([[subQ2,-1.0]])],"derivedFrom":subQ1}),1.0]])]});}
            var Q124;
            {var subQ0=sQuery(id+"F6.wireOp",EDGE,"E188");var subQ1=sQuery(id+"F6.wireOp",EDGE,"E149");var subQ2=makeQuery(id+"F6.imprint","INTERSECT",VERTEX,{"derivedFrom":[subQ1,subQ0]});Q124=makeQuery(id+"F6.imprint","IMPRINT",FACE,{"disambiguationData":[TD([[makeQuery(id+"F6.imprint","IMPRINT",EDGE,{"disambiguationData":[TD([[subQ2,-1.0]])],"derivedFrom":subQ1}),1.0]])]});}
            var Q125;
            {var subQ0=sQuery(id+"F6.wireOp",EDGE,"E188");var subQ1=sQuery(id+"F6.wireOp",EDGE,"E151");var subQ2=makeQuery(id+"F6.imprint","INTERSECT",VERTEX,{"derivedFrom":[subQ1,subQ0]});Q125=makeQuery(id+"F6.imprint","IMPRINT",FACE,{"disambiguationData":[TD([[makeQuery(id+"F6.imprint","IMPRINT",EDGE,{"disambiguationData":[TD([[subQ2,-1.0]])],"derivedFrom":subQ1}),1.0]])]});}
            var Q126;
            {var subQ0=sQuery(id+"F6.wireOp",EDGE,"E188");var subQ1=sQuery(id+"F6.wireOp",EDGE,"E153");var subQ2=makeQuery(id+"F6.imprint","INTERSECT",VERTEX,{"derivedFrom":[subQ1,subQ0]});Q126=makeQuery(id+"F6.imprint","IMPRINT",FACE,{"disambiguationData":[TD([[makeQuery(id+"F6.imprint","IMPRINT",EDGE,{"disambiguationData":[TD([[subQ2,-1.0]])],"derivedFrom":subQ1}),1.0]])]});}
            var Q127;
            {var subQ0=sQuery(id+"F6.wireOp",EDGE,"E188");var subQ1=sQuery(id+"F6.wireOp",EDGE,"E155");var subQ2=makeQuery(id+"F6.imprint","INTERSECT",VERTEX,{"derivedFrom":[subQ1,subQ0]});Q127=makeQuery(id+"F6.imprint","IMPRINT",FACE,{"disambiguationData":[TD([[makeQuery(id+"F6.imprint","IMPRINT",EDGE,{"disambiguationData":[TD([[subQ2,-1.0]])],"derivedFrom":subQ1}),1.0]])]});}
            var Q128;
            {var subQ0=sQuery(id+"F6.wireOp",EDGE,"E188");var subQ1=sQuery(id+"F6.wireOp",EDGE,"E157");var subQ2=makeQuery(id+"F6.imprint","INTERSECT",VERTEX,{"derivedFrom":[subQ1,subQ0]});Q128=makeQuery(id+"F6.imprint","IMPRINT",FACE,{"disambiguationData":[TD([[makeQuery(id+"F6.imprint","IMPRINT",EDGE,{"disambiguationData":[TD([[subQ2,-1.0]])],"derivedFrom":subQ1}),1.0]])]});}
            var Q129;
            {var subQ0=sQuery(id+"F6.wireOp",EDGE,"E188");var subQ1=sQuery(id+"F6.wireOp",EDGE,"E159");var subQ2=makeQuery(id+"F6.imprint","INTERSECT",VERTEX,{"derivedFrom":[subQ1,subQ0]});Q129=makeQuery(id+"F6.imprint","IMPRINT",FACE,{"disambiguationData":[TD([[makeQuery(id+"F6.imprint","IMPRINT",EDGE,{"disambiguationData":[TD([[subQ2,-1.0]])],"derivedFrom":subQ1}),1.0]])]});}
            var Q130;
            {var subQ0=sQuery(id+"F6.wireOp",EDGE,"E188");var subQ1=sQuery(id+"F6.wireOp",EDGE,"E161");var subQ2=makeQuery(id+"F6.imprint","INTERSECT",VERTEX,{"derivedFrom":[subQ1,subQ0]});Q130=makeQuery(id+"F6.imprint","IMPRINT",FACE,{"disambiguationData":[TD([[makeQuery(id+"F6.imprint","IMPRINT",EDGE,{"disambiguationData":[TD([[subQ2,-1.0]])],"derivedFrom":subQ1}),1.0]])]});}
            var Q131;
            {var subQ0=sQuery(id+"F6.wireOp",EDGE,"E188");var subQ1=sQuery(id+"F6.wireOp",EDGE,"E163");var subQ2=makeQuery(id+"F6.imprint","INTERSECT",VERTEX,{"derivedFrom":[subQ1,subQ0]});Q131=makeQuery(id+"F6.imprint","IMPRINT",FACE,{"disambiguationData":[TD([[makeQuery(id+"F6.imprint","IMPRINT",EDGE,{"disambiguationData":[TD([[subQ2,-1.0]])],"derivedFrom":subQ1}),1.0]])]});}
            var Q132;
            {var subQ0=sQuery(id+"F6.wireOp",EDGE,"E188");var subQ1=sQuery(id+"F6.wireOp",EDGE,"E165");var subQ2=makeQuery(id+"F6.imprint","INTERSECT",VERTEX,{"derivedFrom":[subQ1,subQ0]});Q132=makeQuery(id+"F6.imprint","IMPRINT",FACE,{"disambiguationData":[TD([[makeQuery(id+"F6.imprint","IMPRINT",EDGE,{"disambiguationData":[TD([[subQ2,-1.0]])],"derivedFrom":subQ1}),1.0]])]});}
            var Q133;
            {var subQ0=sQuery(id+"F6.wireOp",EDGE,"E188");var subQ1=sQuery(id+"F6.wireOp",EDGE,"E169");var subQ2=makeQuery(id+"F6.imprint","INTERSECT",VERTEX,{"derivedFrom":[subQ1,subQ0]});Q133=makeQuery(id+"F6.imprint","IMPRINT",FACE,{"disambiguationData":[TD([[makeQuery(id+"F6.imprint","IMPRINT",EDGE,{"disambiguationData":[TD([[subQ2,-1.0]])],"derivedFrom":subQ1}),1.0]])]});}
            var Q134;
            {var subQ0=sQuery(id+"F6.wireOp",EDGE,"E190");var subQ1=sQuery(id+"F6.wireOp",EDGE,"E169");var subQ2=makeQuery(id+"F6.imprint","INTERSECT",VERTEX,{"derivedFrom":[subQ1,subQ0]});Q134=makeQuery(id+"F6.imprint","IMPRINT",FACE,{"disambiguationData":[TD([[makeQuery(id+"F6.imprint","IMPRINT",EDGE,{"disambiguationData":[TD([[subQ2,-1.0]])],"derivedFrom":subQ1}),1.0]])]});}
            var Q135;
            {var subQ0=sQuery(id+"F6.wireOp",EDGE,"E190");var subQ1=sQuery(id+"F6.wireOp",EDGE,"E165");var subQ2=makeQuery(id+"F6.imprint","INTERSECT",VERTEX,{"derivedFrom":[subQ1,subQ0]});Q135=makeQuery(id+"F6.imprint","IMPRINT",FACE,{"disambiguationData":[TD([[makeQuery(id+"F6.imprint","IMPRINT",EDGE,{"disambiguationData":[TD([[subQ2,-1.0]])],"derivedFrom":subQ1}),1.0]])]});}
            var Q136;
            {var subQ0=sQuery(id+"F6.wireOp",EDGE,"E190");var subQ1=sQuery(id+"F6.wireOp",EDGE,"E163");var subQ2=makeQuery(id+"F6.imprint","INTERSECT",VERTEX,{"derivedFrom":[subQ1,subQ0]});Q136=makeQuery(id+"F6.imprint","IMPRINT",FACE,{"disambiguationData":[TD([[makeQuery(id+"F6.imprint","IMPRINT",EDGE,{"disambiguationData":[TD([[subQ2,-1.0]])],"derivedFrom":subQ1}),1.0]])]});}
            var Q137;
            {var subQ0=sQuery(id+"F6.wireOp",EDGE,"E190");var subQ1=sQuery(id+"F6.wireOp",EDGE,"E161");var subQ2=makeQuery(id+"F6.imprint","INTERSECT",VERTEX,{"derivedFrom":[subQ1,subQ0]});Q137=makeQuery(id+"F6.imprint","IMPRINT",FACE,{"disambiguationData":[TD([[makeQuery(id+"F6.imprint","IMPRINT",EDGE,{"disambiguationData":[TD([[subQ2,-1.0]])],"derivedFrom":subQ1}),1.0]])]});}
            var Q138;
            {var subQ0=sQuery(id+"F6.wireOp",EDGE,"E190");var subQ1=sQuery(id+"F6.wireOp",EDGE,"E159");var subQ2=makeQuery(id+"F6.imprint","INTERSECT",VERTEX,{"derivedFrom":[subQ1,subQ0]});Q138=makeQuery(id+"F6.imprint","IMPRINT",FACE,{"disambiguationData":[TD([[makeQuery(id+"F6.imprint","IMPRINT",EDGE,{"disambiguationData":[TD([[subQ2,-1.0]])],"derivedFrom":subQ1}),1.0]])]});}
            var Q139;
            {var subQ0=sQuery(id+"F6.wireOp",EDGE,"E190");var subQ1=sQuery(id+"F6.wireOp",EDGE,"E157");var subQ2=makeQuery(id+"F6.imprint","INTERSECT",VERTEX,{"derivedFrom":[subQ1,subQ0]});Q139=makeQuery(id+"F6.imprint","IMPRINT",FACE,{"disambiguationData":[TD([[makeQuery(id+"F6.imprint","IMPRINT",EDGE,{"disambiguationData":[TD([[subQ2,-1.0]])],"derivedFrom":subQ1}),1.0]])]});}
            var Q140;
            {var subQ0=sQuery(id+"F6.wireOp",EDGE,"E190");var subQ1=sQuery(id+"F6.wireOp",EDGE,"E155");var subQ2=makeQuery(id+"F6.imprint","INTERSECT",VERTEX,{"derivedFrom":[subQ1,subQ0]});Q140=makeQuery(id+"F6.imprint","IMPRINT",FACE,{"disambiguationData":[TD([[makeQuery(id+"F6.imprint","IMPRINT",EDGE,{"disambiguationData":[TD([[subQ2,-1.0]])],"derivedFrom":subQ1}),1.0]])]});}
            var Q141;
            {var subQ0=sQuery(id+"F6.wireOp",EDGE,"E190");var subQ1=sQuery(id+"F6.wireOp",EDGE,"E153");var subQ2=makeQuery(id+"F6.imprint","INTERSECT",VERTEX,{"derivedFrom":[subQ1,subQ0]});Q141=makeQuery(id+"F6.imprint","IMPRINT",FACE,{"disambiguationData":[TD([[makeQuery(id+"F6.imprint","IMPRINT",EDGE,{"disambiguationData":[TD([[subQ2,-1.0]])],"derivedFrom":subQ1}),1.0]])]});}
            var Q142;
            {var subQ0=sQuery(id+"F6.wireOp",EDGE,"E190");var subQ1=sQuery(id+"F6.wireOp",EDGE,"E151");var subQ2=makeQuery(id+"F6.imprint","INTERSECT",VERTEX,{"derivedFrom":[subQ1,subQ0]});Q142=makeQuery(id+"F6.imprint","IMPRINT",FACE,{"disambiguationData":[TD([[makeQuery(id+"F6.imprint","IMPRINT",EDGE,{"disambiguationData":[TD([[subQ2,-1.0]])],"derivedFrom":subQ1}),1.0]])]});}
            var Q143;
            {var subQ0=sQuery(id+"F6.wireOp",EDGE,"E190");var subQ1=sQuery(id+"F6.wireOp",EDGE,"E149");var subQ2=makeQuery(id+"F6.imprint","INTERSECT",VERTEX,{"derivedFrom":[subQ1,subQ0]});Q143=makeQuery(id+"F6.imprint","IMPRINT",FACE,{"disambiguationData":[TD([[makeQuery(id+"F6.imprint","IMPRINT",EDGE,{"disambiguationData":[TD([[subQ2,-1.0]])],"derivedFrom":subQ1}),1.0]])]});}
            var Q144;
            {var subQ0=sQuery(id+"F6.wireOp",EDGE,"E190");var subQ1=sQuery(id+"F6.wireOp",EDGE,"E147");var subQ2=makeQuery(id+"F6.imprint","INTERSECT",VERTEX,{"derivedFrom":[subQ1,subQ0]});Q144=makeQuery(id+"F6.imprint","IMPRINT",FACE,{"disambiguationData":[TD([[makeQuery(id+"F6.imprint","IMPRINT",EDGE,{"disambiguationData":[TD([[subQ2,-1.0]])],"derivedFrom":subQ1}),1.0]])]});}
            var Q145;
            {var subQ0=sQuery(id+"F6.wireOp",EDGE,"E190");var subQ1=sQuery(id+"F6.wireOp",EDGE,"E145");var subQ2=makeQuery(id+"F6.imprint","INTERSECT",VERTEX,{"derivedFrom":[subQ1,subQ0]});Q145=makeQuery(id+"F6.imprint","IMPRINT",FACE,{"disambiguationData":[TD([[makeQuery(id+"F6.imprint","IMPRINT",EDGE,{"disambiguationData":[TD([[subQ2,-1.0]])],"derivedFrom":subQ1}),1.0]])]});}
            var Q146;
            {var subQ0=sQuery(id+"F6.wireOp",EDGE,"E190");var subQ1=sQuery(id+"F6.wireOp",EDGE,"E143");var subQ2=makeQuery(id+"F6.imprint","INTERSECT",VERTEX,{"derivedFrom":[subQ1,subQ0]});Q146=makeQuery(id+"F6.imprint","IMPRINT",FACE,{"disambiguationData":[TD([[makeQuery(id+"F6.imprint","IMPRINT",EDGE,{"disambiguationData":[TD([[subQ2,-1.0]])],"derivedFrom":subQ1}),1.0]])]});}
            var Q147;
            {var subQ0=sQuery(id+"F6.wireOp",EDGE,"E190");var subQ1=sQuery(id+"F6.wireOp",EDGE,"E141");var subQ2=makeQuery(id+"F6.imprint","INTERSECT",VERTEX,{"derivedFrom":[subQ1,subQ0]});Q147=makeQuery(id+"F6.imprint","IMPRINT",FACE,{"disambiguationData":[TD([[makeQuery(id+"F6.imprint","IMPRINT",EDGE,{"disambiguationData":[TD([[subQ2,-1.0]])],"derivedFrom":subQ1}),1.0]])]});}
            var Q148;
            {var subQ0=sQuery(id+"F6.wireOp",EDGE,"E190");var subQ1=sQuery(id+"F6.wireOp",EDGE,"E137");var subQ2=makeQuery(id+"F6.imprint","INTERSECT",VERTEX,{"derivedFrom":[subQ1,subQ0]});Q148=makeQuery(id+"F6.imprint","IMPRINT",FACE,{"disambiguationData":[TD([[makeQuery(id+"F6.imprint","IMPRINT",EDGE,{"disambiguationData":[TD([[subQ2,-1.0]])],"derivedFrom":subQ1}),1.0]])]});}
            var Q149;
            {var subQ0=sQuery(id+"F6.wireOp",EDGE,"E190");var subQ1=sQuery(id+"F6.wireOp",EDGE,"E135");var subQ2=makeQuery(id+"F6.imprint","INTERSECT",VERTEX,{"derivedFrom":[subQ1,subQ0]});Q149=makeQuery(id+"F6.imprint","IMPRINT",FACE,{"disambiguationData":[TD([[makeQuery(id+"F6.imprint","IMPRINT",EDGE,{"disambiguationData":[TD([[subQ2,-1.0]])],"derivedFrom":subQ1}),1.0]])]});}
            var Q150;
            {var subQ0=sQuery(id+"F6.wireOp",EDGE,"E192");var subQ1=sQuery(id+"F6.wireOp",EDGE,"E135");var subQ2=makeQuery(id+"F6.imprint","INTERSECT",VERTEX,{"derivedFrom":[subQ1,subQ0]});Q150=makeQuery(id+"F6.imprint","IMPRINT",FACE,{"disambiguationData":[TD([[makeQuery(id+"F6.imprint","IMPRINT",EDGE,{"disambiguationData":[TD([[subQ2,-1.0]])],"derivedFrom":subQ1}),1.0]])]});}
            var Q151;
            {var subQ0=sQuery(id+"F6.wireOp",EDGE,"E192");var subQ1=sQuery(id+"F6.wireOp",EDGE,"E137");var subQ2=makeQuery(id+"F6.imprint","INTERSECT",VERTEX,{"derivedFrom":[subQ1,subQ0]});Q151=makeQuery(id+"F6.imprint","IMPRINT",FACE,{"disambiguationData":[TD([[makeQuery(id+"F6.imprint","IMPRINT",EDGE,{"disambiguationData":[TD([[subQ2,-1.0]])],"derivedFrom":subQ1}),1.0]])]});}
            var Q152;
            {var subQ0=sQuery(id+"F6.wireOp",EDGE,"E192");var subQ1=sQuery(id+"F6.wireOp",EDGE,"E139");var subQ2=makeQuery(id+"F6.imprint","INTERSECT",VERTEX,{"derivedFrom":[subQ1,subQ0]});Q152=makeQuery(id+"F6.imprint","IMPRINT",FACE,{"disambiguationData":[TD([[makeQuery(id+"F6.imprint","IMPRINT",EDGE,{"disambiguationData":[TD([[subQ2,-1.0]])],"derivedFrom":subQ1}),1.0]])]});}
            var Q153;
            {var subQ0=sQuery(id+"F6.wireOp",EDGE,"E190");var subQ1=sQuery(id+"F6.wireOp",EDGE,"E139");var subQ2=makeQuery(id+"F6.imprint","INTERSECT",VERTEX,{"derivedFrom":[subQ1,subQ0]});Q153=makeQuery(id+"F6.imprint","IMPRINT",FACE,{"disambiguationData":[TD([[makeQuery(id+"F6.imprint","IMPRINT",EDGE,{"disambiguationData":[TD([[subQ2,-1.0]])],"derivedFrom":subQ1}),1.0]])]});}
            var Q154;
            {var subQ0=sQuery(id+"F6.wireOp",EDGE,"E192");var subQ1=sQuery(id+"F6.wireOp",EDGE,"E141");var subQ2=makeQuery(id+"F6.imprint","INTERSECT",VERTEX,{"derivedFrom":[subQ1,subQ0]});Q154=makeQuery(id+"F6.imprint","IMPRINT",FACE,{"disambiguationData":[TD([[makeQuery(id+"F6.imprint","IMPRINT",EDGE,{"disambiguationData":[TD([[subQ2,-1.0]])],"derivedFrom":subQ1}),1.0]])]});}
            var Q155;
            {var subQ0=sQuery(id+"F6.wireOp",EDGE,"E192");var subQ1=sQuery(id+"F6.wireOp",EDGE,"E143");var subQ2=makeQuery(id+"F6.imprint","INTERSECT",VERTEX,{"derivedFrom":[subQ1,subQ0]});Q155=makeQuery(id+"F6.imprint","IMPRINT",FACE,{"disambiguationData":[TD([[makeQuery(id+"F6.imprint","IMPRINT",EDGE,{"disambiguationData":[TD([[subQ2,-1.0]])],"derivedFrom":subQ1}),1.0]])]});}
            var Q156;
            {var subQ0=sQuery(id+"F6.wireOp",EDGE,"E192");var subQ1=sQuery(id+"F6.wireOp",EDGE,"E145");var subQ2=makeQuery(id+"F6.imprint","INTERSECT",VERTEX,{"derivedFrom":[subQ1,subQ0]});Q156=makeQuery(id+"F6.imprint","IMPRINT",FACE,{"disambiguationData":[TD([[makeQuery(id+"F6.imprint","IMPRINT",EDGE,{"disambiguationData":[TD([[subQ2,-1.0]])],"derivedFrom":subQ1}),1.0]])]});}
            var Q157;
            {var subQ0=sQuery(id+"F6.wireOp",EDGE,"E192");var subQ1=sQuery(id+"F6.wireOp",EDGE,"E147");var subQ2=makeQuery(id+"F6.imprint","INTERSECT",VERTEX,{"derivedFrom":[subQ1,subQ0]});Q157=makeQuery(id+"F6.imprint","IMPRINT",FACE,{"disambiguationData":[TD([[makeQuery(id+"F6.imprint","IMPRINT",EDGE,{"disambiguationData":[TD([[subQ2,-1.0]])],"derivedFrom":subQ1}),1.0]])]});}
            var Q158;
            {var subQ0=sQuery(id+"F6.wireOp",EDGE,"E192");var subQ1=sQuery(id+"F6.wireOp",EDGE,"E149");var subQ2=makeQuery(id+"F6.imprint","INTERSECT",VERTEX,{"derivedFrom":[subQ1,subQ0]});Q158=makeQuery(id+"F6.imprint","IMPRINT",FACE,{"disambiguationData":[TD([[makeQuery(id+"F6.imprint","IMPRINT",EDGE,{"disambiguationData":[TD([[subQ2,-1.0]])],"derivedFrom":subQ1}),1.0]])]});}
            var Q159;
            {var subQ0=sQuery(id+"F6.wireOp",EDGE,"E192");var subQ1=sQuery(id+"F6.wireOp",EDGE,"E151");var subQ2=makeQuery(id+"F6.imprint","INTERSECT",VERTEX,{"derivedFrom":[subQ1,subQ0]});Q159=makeQuery(id+"F6.imprint","IMPRINT",FACE,{"disambiguationData":[TD([[makeQuery(id+"F6.imprint","IMPRINT",EDGE,{"disambiguationData":[TD([[subQ2,-1.0]])],"derivedFrom":subQ1}),1.0]])]});}
            var Q160;
            {var subQ0=sQuery(id+"F6.wireOp",EDGE,"E192");var subQ1=sQuery(id+"F6.wireOp",EDGE,"E153");var subQ2=makeQuery(id+"F6.imprint","INTERSECT",VERTEX,{"derivedFrom":[subQ1,subQ0]});Q160=makeQuery(id+"F6.imprint","IMPRINT",FACE,{"disambiguationData":[TD([[makeQuery(id+"F6.imprint","IMPRINT",EDGE,{"disambiguationData":[TD([[subQ2,-1.0]])],"derivedFrom":subQ1}),1.0]])]});}
            var Q161;
            {var subQ0=sQuery(id+"F6.wireOp",EDGE,"E192");var subQ1=sQuery(id+"F6.wireOp",EDGE,"E155");var subQ2=makeQuery(id+"F6.imprint","INTERSECT",VERTEX,{"derivedFrom":[subQ1,subQ0]});Q161=makeQuery(id+"F6.imprint","IMPRINT",FACE,{"disambiguationData":[TD([[makeQuery(id+"F6.imprint","IMPRINT",EDGE,{"disambiguationData":[TD([[subQ2,-1.0]])],"derivedFrom":subQ1}),1.0]])]});}
            var Q162;
            {var subQ0=sQuery(id+"F6.wireOp",EDGE,"E192");var subQ1=sQuery(id+"F6.wireOp",EDGE,"E157");var subQ2=makeQuery(id+"F6.imprint","INTERSECT",VERTEX,{"derivedFrom":[subQ1,subQ0]});Q162=makeQuery(id+"F6.imprint","IMPRINT",FACE,{"disambiguationData":[TD([[makeQuery(id+"F6.imprint","IMPRINT",EDGE,{"disambiguationData":[TD([[subQ2,-1.0]])],"derivedFrom":subQ1}),1.0]])]});}
            var Q163;
            {var subQ0=sQuery(id+"F6.wireOp",EDGE,"E192");var subQ1=sQuery(id+"F6.wireOp",EDGE,"E159");var subQ2=makeQuery(id+"F6.imprint","INTERSECT",VERTEX,{"derivedFrom":[subQ1,subQ0]});Q163=makeQuery(id+"F6.imprint","IMPRINT",FACE,{"disambiguationData":[TD([[makeQuery(id+"F6.imprint","IMPRINT",EDGE,{"disambiguationData":[TD([[subQ2,-1.0]])],"derivedFrom":subQ1}),1.0]])]});}
            var Q164;
            {var subQ0=sQuery(id+"F6.wireOp",EDGE,"E192");var subQ1=sQuery(id+"F6.wireOp",EDGE,"E161");var subQ2=makeQuery(id+"F6.imprint","INTERSECT",VERTEX,{"derivedFrom":[subQ1,subQ0]});Q164=makeQuery(id+"F6.imprint","IMPRINT",FACE,{"disambiguationData":[TD([[makeQuery(id+"F6.imprint","IMPRINT",EDGE,{"disambiguationData":[TD([[subQ2,-1.0]])],"derivedFrom":subQ1}),1.0]])]});}
            var Q165;
            {var subQ0=sQuery(id+"F6.wireOp",EDGE,"E192");var subQ1=sQuery(id+"F6.wireOp",EDGE,"E163");var subQ2=makeQuery(id+"F6.imprint","INTERSECT",VERTEX,{"derivedFrom":[subQ1,subQ0]});Q165=makeQuery(id+"F6.imprint","IMPRINT",FACE,{"disambiguationData":[TD([[makeQuery(id+"F6.imprint","IMPRINT",EDGE,{"disambiguationData":[TD([[subQ2,-1.0]])],"derivedFrom":subQ1}),1.0]])]});}
            var Q166;
            {var subQ0=sQuery(id+"F6.wireOp",EDGE,"E192");var subQ1=sQuery(id+"F6.wireOp",EDGE,"E165");var subQ2=makeQuery(id+"F6.imprint","INTERSECT",VERTEX,{"derivedFrom":[subQ1,subQ0]});Q166=makeQuery(id+"F6.imprint","IMPRINT",FACE,{"disambiguationData":[TD([[makeQuery(id+"F6.imprint","IMPRINT",EDGE,{"disambiguationData":[TD([[subQ2,-1.0]])],"derivedFrom":subQ1}),1.0]])]});}
            var Q167;
            {var subQ0=sQuery(id+"F6.wireOp",EDGE,"E192");var subQ1=sQuery(id+"F6.wireOp",EDGE,"E169");var subQ2=makeQuery(id+"F6.imprint","INTERSECT",VERTEX,{"derivedFrom":[subQ1,subQ0]});Q167=makeQuery(id+"F6.imprint","IMPRINT",FACE,{"disambiguationData":[TD([[makeQuery(id+"F6.imprint","IMPRINT",EDGE,{"disambiguationData":[TD([[subQ2,-1.0]])],"derivedFrom":subQ1}),1.0]])]});}
            var Q168;
            {var subQ0=sQuery(id+"F6.wireOp",EDGE,"E194");var subQ1=sQuery(id+"F6.wireOp",EDGE,"E169");var subQ2=makeQuery(id+"F6.imprint","INTERSECT",VERTEX,{"derivedFrom":[subQ1,subQ0]});Q168=makeQuery(id+"F6.imprint","IMPRINT",FACE,{"disambiguationData":[TD([[makeQuery(id+"F6.imprint","IMPRINT",EDGE,{"disambiguationData":[TD([[subQ2,-1.0]])],"derivedFrom":subQ1}),1.0]])]});}
            var Q169;
            {var subQ0=sQuery(id+"F6.wireOp",EDGE,"E196");var subQ1=sQuery(id+"F6.wireOp",EDGE,"E169");var subQ2=makeQuery(id+"F6.imprint","INTERSECT",VERTEX,{"derivedFrom":[subQ1,subQ0]});Q169=makeQuery(id+"F6.imprint","IMPRINT",FACE,{"disambiguationData":[TD([[makeQuery(id+"F6.imprint","IMPRINT",EDGE,{"disambiguationData":[TD([[subQ2,-1.0]])],"derivedFrom":subQ1}),1.0]])]});}
            var Q170;
            {var subQ0=sQuery(id+"F6.wireOp",EDGE,"E196");var subQ1=sQuery(id+"F6.wireOp",EDGE,"E165");var subQ2=makeQuery(id+"F6.imprint","INTERSECT",VERTEX,{"derivedFrom":[subQ1,subQ0]});Q170=makeQuery(id+"F6.imprint","IMPRINT",FACE,{"disambiguationData":[TD([[makeQuery(id+"F6.imprint","IMPRINT",EDGE,{"disambiguationData":[TD([[subQ2,-1.0]])],"derivedFrom":subQ1}),1.0]])]});}
            var Q171;
            {var subQ0=sQuery(id+"F6.wireOp",EDGE,"E194");var subQ1=sQuery(id+"F6.wireOp",EDGE,"E165");var subQ2=makeQuery(id+"F6.imprint","INTERSECT",VERTEX,{"derivedFrom":[subQ1,subQ0]});Q171=makeQuery(id+"F6.imprint","IMPRINT",FACE,{"disambiguationData":[TD([[makeQuery(id+"F6.imprint","IMPRINT",EDGE,{"disambiguationData":[TD([[subQ2,-1.0]])],"derivedFrom":subQ1}),1.0]])]});}
            var Q172;
            {var subQ0=sQuery(id+"F6.wireOp",EDGE,"E194");var subQ1=sQuery(id+"F6.wireOp",EDGE,"E163");var subQ2=makeQuery(id+"F6.imprint","INTERSECT",VERTEX,{"derivedFrom":[subQ1,subQ0]});Q172=makeQuery(id+"F6.imprint","IMPRINT",FACE,{"disambiguationData":[TD([[makeQuery(id+"F6.imprint","IMPRINT",EDGE,{"disambiguationData":[TD([[subQ2,-1.0]])],"derivedFrom":subQ1}),1.0]])]});}
            var Q173;
            {var subQ0=sQuery(id+"F6.wireOp",EDGE,"E196");var subQ1=sQuery(id+"F6.wireOp",EDGE,"E163");var subQ2=makeQuery(id+"F6.imprint","INTERSECT",VERTEX,{"derivedFrom":[subQ1,subQ0]});Q173=makeQuery(id+"F6.imprint","IMPRINT",FACE,{"disambiguationData":[TD([[makeQuery(id+"F6.imprint","IMPRINT",EDGE,{"disambiguationData":[TD([[subQ2,-1.0]])],"derivedFrom":subQ1}),1.0]])]});}
            var Q174;
            {var subQ0=sQuery(id+"F6.wireOp",EDGE,"E196");var subQ1=sQuery(id+"F6.wireOp",EDGE,"E161");var subQ2=makeQuery(id+"F6.imprint","INTERSECT",VERTEX,{"derivedFrom":[subQ1,subQ0]});Q174=makeQuery(id+"F6.imprint","IMPRINT",FACE,{"disambiguationData":[TD([[makeQuery(id+"F6.imprint","IMPRINT",EDGE,{"disambiguationData":[TD([[subQ2,-1.0]])],"derivedFrom":subQ1}),1.0]])]});}
            var Q175;
            {var subQ0=sQuery(id+"F6.wireOp",EDGE,"E194");var subQ1=sQuery(id+"F6.wireOp",EDGE,"E161");var subQ2=makeQuery(id+"F6.imprint","INTERSECT",VERTEX,{"derivedFrom":[subQ1,subQ0]});Q175=makeQuery(id+"F6.imprint","IMPRINT",FACE,{"disambiguationData":[TD([[makeQuery(id+"F6.imprint","IMPRINT",EDGE,{"disambiguationData":[TD([[subQ2,-1.0]])],"derivedFrom":subQ1}),1.0]])]});}
            var Q176;
            {var subQ0=sQuery(id+"F6.wireOp",EDGE,"E194");var subQ1=sQuery(id+"F6.wireOp",EDGE,"E159");var subQ2=makeQuery(id+"F6.imprint","INTERSECT",VERTEX,{"derivedFrom":[subQ1,subQ0]});Q176=makeQuery(id+"F6.imprint","IMPRINT",FACE,{"disambiguationData":[TD([[makeQuery(id+"F6.imprint","IMPRINT",EDGE,{"disambiguationData":[TD([[subQ2,-1.0]])],"derivedFrom":subQ1}),1.0]])]});}
            var Q177;
            {var subQ0=sQuery(id+"F6.wireOp",EDGE,"E196");var subQ1=sQuery(id+"F6.wireOp",EDGE,"E159");var subQ2=makeQuery(id+"F6.imprint","INTERSECT",VERTEX,{"derivedFrom":[subQ1,subQ0]});Q177=makeQuery(id+"F6.imprint","IMPRINT",FACE,{"disambiguationData":[TD([[makeQuery(id+"F6.imprint","IMPRINT",EDGE,{"disambiguationData":[TD([[subQ2,-1.0]])],"derivedFrom":subQ1}),1.0]])]});}
            var Q178;
            {var subQ0=sQuery(id+"F6.wireOp",EDGE,"E196");var subQ1=sQuery(id+"F6.wireOp",EDGE,"E157");var subQ2=makeQuery(id+"F6.imprint","INTERSECT",VERTEX,{"derivedFrom":[subQ1,subQ0]});Q178=makeQuery(id+"F6.imprint","IMPRINT",FACE,{"disambiguationData":[TD([[makeQuery(id+"F6.imprint","IMPRINT",EDGE,{"disambiguationData":[TD([[subQ2,-1.0]])],"derivedFrom":subQ1}),1.0]])]});}
            var Q179;
            {var subQ0=sQuery(id+"F6.wireOp",EDGE,"E194");var subQ1=sQuery(id+"F6.wireOp",EDGE,"E157");var subQ2=makeQuery(id+"F6.imprint","INTERSECT",VERTEX,{"derivedFrom":[subQ1,subQ0]});Q179=makeQuery(id+"F6.imprint","IMPRINT",FACE,{"disambiguationData":[TD([[makeQuery(id+"F6.imprint","IMPRINT",EDGE,{"disambiguationData":[TD([[subQ2,-1.0]])],"derivedFrom":subQ1}),1.0]])]});}
            var Q180;
            {var subQ0=sQuery(id+"F6.wireOp",EDGE,"E194");var subQ1=sQuery(id+"F6.wireOp",EDGE,"E155");var subQ2=makeQuery(id+"F6.imprint","INTERSECT",VERTEX,{"derivedFrom":[subQ1,subQ0]});Q180=makeQuery(id+"F6.imprint","IMPRINT",FACE,{"disambiguationData":[TD([[makeQuery(id+"F6.imprint","IMPRINT",EDGE,{"disambiguationData":[TD([[subQ2,-1.0]])],"derivedFrom":subQ1}),1.0]])]});}
            var Q181;
            {var subQ0=sQuery(id+"F6.wireOp",EDGE,"E196");var subQ1=sQuery(id+"F6.wireOp",EDGE,"E155");var subQ2=makeQuery(id+"F6.imprint","INTERSECT",VERTEX,{"derivedFrom":[subQ1,subQ0]});Q181=makeQuery(id+"F6.imprint","IMPRINT",FACE,{"disambiguationData":[TD([[makeQuery(id+"F6.imprint","IMPRINT",EDGE,{"disambiguationData":[TD([[subQ2,-1.0]])],"derivedFrom":subQ1}),1.0]])]});}
            var Q182;
            {var subQ0=sQuery(id+"F6.wireOp",EDGE,"E196");var subQ1=sQuery(id+"F6.wireOp",EDGE,"E153");var subQ2=makeQuery(id+"F6.imprint","INTERSECT",VERTEX,{"derivedFrom":[subQ1,subQ0]});Q182=makeQuery(id+"F6.imprint","IMPRINT",FACE,{"disambiguationData":[TD([[makeQuery(id+"F6.imprint","IMPRINT",EDGE,{"disambiguationData":[TD([[subQ2,-1.0]])],"derivedFrom":subQ1}),1.0]])]});}
            var Q183;
            {var subQ0=sQuery(id+"F6.wireOp",EDGE,"E194");var subQ1=sQuery(id+"F6.wireOp",EDGE,"E153");var subQ2=makeQuery(id+"F6.imprint","INTERSECT",VERTEX,{"derivedFrom":[subQ1,subQ0]});Q183=makeQuery(id+"F6.imprint","IMPRINT",FACE,{"disambiguationData":[TD([[makeQuery(id+"F6.imprint","IMPRINT",EDGE,{"disambiguationData":[TD([[subQ2,-1.0]])],"derivedFrom":subQ1}),1.0]])]});}
            var Q184;
            {var subQ0=sQuery(id+"F6.wireOp",EDGE,"E194");var subQ1=sQuery(id+"F6.wireOp",EDGE,"E151");var subQ2=makeQuery(id+"F6.imprint","INTERSECT",VERTEX,{"derivedFrom":[subQ1,subQ0]});Q184=makeQuery(id+"F6.imprint","IMPRINT",FACE,{"disambiguationData":[TD([[makeQuery(id+"F6.imprint","IMPRINT",EDGE,{"disambiguationData":[TD([[subQ2,-1.0]])],"derivedFrom":subQ1}),1.0]])]});}
            var Q185;
            {var subQ0=sQuery(id+"F6.wireOp",EDGE,"E196");var subQ1=sQuery(id+"F6.wireOp",EDGE,"E151");var subQ2=makeQuery(id+"F6.imprint","INTERSECT",VERTEX,{"derivedFrom":[subQ1,subQ0]});Q185=makeQuery(id+"F6.imprint","IMPRINT",FACE,{"disambiguationData":[TD([[makeQuery(id+"F6.imprint","IMPRINT",EDGE,{"disambiguationData":[TD([[subQ2,-1.0]])],"derivedFrom":subQ1}),1.0]])]});}
            var Q186;
            {var subQ0=sQuery(id+"F6.wireOp",EDGE,"E196");var subQ1=sQuery(id+"F6.wireOp",EDGE,"E149");var subQ2=makeQuery(id+"F6.imprint","INTERSECT",VERTEX,{"derivedFrom":[subQ1,subQ0]});Q186=makeQuery(id+"F6.imprint","IMPRINT",FACE,{"disambiguationData":[TD([[makeQuery(id+"F6.imprint","IMPRINT",EDGE,{"disambiguationData":[TD([[subQ2,-1.0]])],"derivedFrom":subQ1}),1.0]])]});}
            var Q187;
            {var subQ0=sQuery(id+"F6.wireOp",EDGE,"E194");var subQ1=sQuery(id+"F6.wireOp",EDGE,"E149");var subQ2=makeQuery(id+"F6.imprint","INTERSECT",VERTEX,{"derivedFrom":[subQ1,subQ0]});Q187=makeQuery(id+"F6.imprint","IMPRINT",FACE,{"disambiguationData":[TD([[makeQuery(id+"F6.imprint","IMPRINT",EDGE,{"disambiguationData":[TD([[subQ2,-1.0]])],"derivedFrom":subQ1}),1.0]])]});}
            var Q188;
            {var subQ0=sQuery(id+"F6.wireOp",EDGE,"E194");var subQ1=sQuery(id+"F6.wireOp",EDGE,"E147");var subQ2=makeQuery(id+"F6.imprint","INTERSECT",VERTEX,{"derivedFrom":[subQ1,subQ0]});Q188=makeQuery(id+"F6.imprint","IMPRINT",FACE,{"disambiguationData":[TD([[makeQuery(id+"F6.imprint","IMPRINT",EDGE,{"disambiguationData":[TD([[subQ2,-1.0]])],"derivedFrom":subQ1}),1.0]])]});}
            var Q189;
            {var subQ0=sQuery(id+"F6.wireOp",EDGE,"E196");var subQ1=sQuery(id+"F6.wireOp",EDGE,"E147");var subQ2=makeQuery(id+"F6.imprint","INTERSECT",VERTEX,{"derivedFrom":[subQ1,subQ0]});Q189=makeQuery(id+"F6.imprint","IMPRINT",FACE,{"disambiguationData":[TD([[makeQuery(id+"F6.imprint","IMPRINT",EDGE,{"disambiguationData":[TD([[subQ2,-1.0]])],"derivedFrom":subQ1}),1.0]])]});}
            var Q190;
            {var subQ0=sQuery(id+"F6.wireOp",EDGE,"E196");var subQ1=sQuery(id+"F6.wireOp",EDGE,"E145");var subQ2=makeQuery(id+"F6.imprint","INTERSECT",VERTEX,{"derivedFrom":[subQ1,subQ0]});Q190=makeQuery(id+"F6.imprint","IMPRINT",FACE,{"disambiguationData":[TD([[makeQuery(id+"F6.imprint","IMPRINT",EDGE,{"disambiguationData":[TD([[subQ2,-1.0]])],"derivedFrom":subQ1}),1.0]])]});}
            var Q191;
            {var subQ0=sQuery(id+"F6.wireOp",EDGE,"E194");var subQ1=sQuery(id+"F6.wireOp",EDGE,"E145");var subQ2=makeQuery(id+"F6.imprint","INTERSECT",VERTEX,{"derivedFrom":[subQ1,subQ0]});Q191=makeQuery(id+"F6.imprint","IMPRINT",FACE,{"disambiguationData":[TD([[makeQuery(id+"F6.imprint","IMPRINT",EDGE,{"disambiguationData":[TD([[subQ2,-1.0]])],"derivedFrom":subQ1}),1.0]])]});}
            var Q192;
            {var subQ0=sQuery(id+"F6.wireOp",EDGE,"E194");var subQ1=sQuery(id+"F6.wireOp",EDGE,"E143");var subQ2=makeQuery(id+"F6.imprint","INTERSECT",VERTEX,{"derivedFrom":[subQ1,subQ0]});Q192=makeQuery(id+"F6.imprint","IMPRINT",FACE,{"disambiguationData":[TD([[makeQuery(id+"F6.imprint","IMPRINT",EDGE,{"disambiguationData":[TD([[subQ2,-1.0]])],"derivedFrom":subQ1}),1.0]])]});}
            var Q193;
            {var subQ0=sQuery(id+"F6.wireOp",EDGE,"E196");var subQ1=sQuery(id+"F6.wireOp",EDGE,"E143");var subQ2=makeQuery(id+"F6.imprint","INTERSECT",VERTEX,{"derivedFrom":[subQ1,subQ0]});Q193=makeQuery(id+"F6.imprint","IMPRINT",FACE,{"disambiguationData":[TD([[makeQuery(id+"F6.imprint","IMPRINT",EDGE,{"disambiguationData":[TD([[subQ2,-1.0]])],"derivedFrom":subQ1}),1.0]])]});}
            var Q194;
            {var subQ0=sQuery(id+"F6.wireOp",EDGE,"E196");var subQ1=sQuery(id+"F6.wireOp",EDGE,"E141");var subQ2=makeQuery(id+"F6.imprint","INTERSECT",VERTEX,{"derivedFrom":[subQ1,subQ0]});Q194=makeQuery(id+"F6.imprint","IMPRINT",FACE,{"disambiguationData":[TD([[makeQuery(id+"F6.imprint","IMPRINT",EDGE,{"disambiguationData":[TD([[subQ2,-1.0]])],"derivedFrom":subQ1}),1.0]])]});}
            var Q195;
            {var subQ0=sQuery(id+"F6.wireOp",EDGE,"E194");var subQ1=sQuery(id+"F6.wireOp",EDGE,"E141");var subQ2=makeQuery(id+"F6.imprint","INTERSECT",VERTEX,{"derivedFrom":[subQ1,subQ0]});Q195=makeQuery(id+"F6.imprint","IMPRINT",FACE,{"disambiguationData":[TD([[makeQuery(id+"F6.imprint","IMPRINT",EDGE,{"disambiguationData":[TD([[subQ2,-1.0]])],"derivedFrom":subQ1}),1.0]])]});}
            var Q196;
            {var subQ0=sQuery(id+"F6.wireOp",EDGE,"E194");var subQ1=sQuery(id+"F6.wireOp",EDGE,"E139");var subQ2=makeQuery(id+"F6.imprint","INTERSECT",VERTEX,{"derivedFrom":[subQ1,subQ0]});Q196=makeQuery(id+"F6.imprint","IMPRINT",FACE,{"disambiguationData":[TD([[makeQuery(id+"F6.imprint","IMPRINT",EDGE,{"disambiguationData":[TD([[subQ2,-1.0]])],"derivedFrom":subQ1}),1.0]])]});}
            var Q197;
            {var subQ0=sQuery(id+"F6.wireOp",EDGE,"E196");var subQ1=sQuery(id+"F6.wireOp",EDGE,"E139");var subQ2=makeQuery(id+"F6.imprint","INTERSECT",VERTEX,{"derivedFrom":[subQ1,subQ0]});Q197=makeQuery(id+"F6.imprint","IMPRINT",FACE,{"disambiguationData":[TD([[makeQuery(id+"F6.imprint","IMPRINT",EDGE,{"disambiguationData":[TD([[subQ2,-1.0]])],"derivedFrom":subQ1}),1.0]])]});}
            var Q198;
            {var subQ0=sQuery(id+"F6.wireOp",EDGE,"E196");var subQ1=sQuery(id+"F6.wireOp",EDGE,"E137");var subQ2=makeQuery(id+"F6.imprint","INTERSECT",VERTEX,{"derivedFrom":[subQ1,subQ0]});Q198=makeQuery(id+"F6.imprint","IMPRINT",FACE,{"disambiguationData":[TD([[makeQuery(id+"F6.imprint","IMPRINT",EDGE,{"disambiguationData":[TD([[subQ2,-1.0]])],"derivedFrom":subQ1}),1.0]])]});}
            var Q199;
            {var subQ0=sQuery(id+"F6.wireOp",EDGE,"E194");var subQ1=sQuery(id+"F6.wireOp",EDGE,"E137");var subQ2=makeQuery(id+"F6.imprint","INTERSECT",VERTEX,{"derivedFrom":[subQ1,subQ0]});Q199=makeQuery(id+"F6.imprint","IMPRINT",FACE,{"disambiguationData":[TD([[makeQuery(id+"F6.imprint","IMPRINT",EDGE,{"disambiguationData":[TD([[subQ2,-1.0]])],"derivedFrom":subQ1}),1.0]])]});}
            var Q200;
            {var subQ0=sQuery(id+"F6.wireOp",EDGE,"E194");var subQ1=sQuery(id+"F6.wireOp",EDGE,"E135");var subQ2=makeQuery(id+"F6.imprint","INTERSECT",VERTEX,{"derivedFrom":[subQ1,subQ0]});Q200=makeQuery(id+"F6.imprint","IMPRINT",FACE,{"disambiguationData":[TD([[makeQuery(id+"F6.imprint","IMPRINT",EDGE,{"disambiguationData":[TD([[subQ2,-1.0]])],"derivedFrom":subQ1}),1.0]])]});}
            var Q201;
            {var subQ0=sQuery(id+"F6.wireOp",EDGE,"E196");var subQ1=sQuery(id+"F6.wireOp",EDGE,"E135");var subQ2=makeQuery(id+"F6.imprint","INTERSECT",VERTEX,{"derivedFrom":[subQ1,subQ0]});Q201=makeQuery(id+"F6.imprint","IMPRINT",FACE,{"disambiguationData":[TD([[makeQuery(id+"F6.imprint","IMPRINT",EDGE,{"disambiguationData":[TD([[subQ2,-1.0]])],"derivedFrom":subQ1}),1.0]])]});}
            var Q202;
            {var subQ0=sQuery(id+"F6.wireOp",EDGE,"E198");var subQ1=sQuery(id+"F6.wireOp",EDGE,"E135");var subQ2=makeQuery(id+"F6.imprint","INTERSECT",VERTEX,{"derivedFrom":[subQ1,subQ0]});Q202=makeQuery(id+"F6.imprint","IMPRINT",FACE,{"disambiguationData":[TD([[makeQuery(id+"F6.imprint","IMPRINT",EDGE,{"disambiguationData":[TD([[subQ2,-1.0]])],"derivedFrom":subQ1}),1.0]])]});}
            var Q203;
            {var subQ0=sQuery(id+"F6.wireOp",EDGE,"E198");var subQ1=sQuery(id+"F6.wireOp",EDGE,"E137");var subQ2=makeQuery(id+"F6.imprint","INTERSECT",VERTEX,{"derivedFrom":[subQ1,subQ0]});Q203=makeQuery(id+"F6.imprint","IMPRINT",FACE,{"disambiguationData":[TD([[makeQuery(id+"F6.imprint","IMPRINT",EDGE,{"disambiguationData":[TD([[subQ2,-1.0]])],"derivedFrom":subQ1}),1.0]])]});}
            var Q204;
            {var subQ0=sQuery(id+"F6.wireOp",EDGE,"E198");var subQ1=sQuery(id+"F6.wireOp",EDGE,"E139");var subQ2=makeQuery(id+"F6.imprint","INTERSECT",VERTEX,{"derivedFrom":[subQ1,subQ0]});Q204=makeQuery(id+"F6.imprint","IMPRINT",FACE,{"disambiguationData":[TD([[makeQuery(id+"F6.imprint","IMPRINT",EDGE,{"disambiguationData":[TD([[subQ2,-1.0]])],"derivedFrom":subQ1}),1.0]])]});}
            var Q205;
            {var subQ0=sQuery(id+"F6.wireOp",EDGE,"E198");var subQ1=sQuery(id+"F6.wireOp",EDGE,"E141");var subQ2=makeQuery(id+"F6.imprint","INTERSECT",VERTEX,{"derivedFrom":[subQ1,subQ0]});Q205=makeQuery(id+"F6.imprint","IMPRINT",FACE,{"disambiguationData":[TD([[makeQuery(id+"F6.imprint","IMPRINT",EDGE,{"disambiguationData":[TD([[subQ2,-1.0]])],"derivedFrom":subQ1}),1.0]])]});}
            var Q206;
            {var subQ0=sQuery(id+"F6.wireOp",EDGE,"E198");var subQ1=sQuery(id+"F6.wireOp",EDGE,"E143");var subQ2=makeQuery(id+"F6.imprint","INTERSECT",VERTEX,{"derivedFrom":[subQ1,subQ0]});Q206=makeQuery(id+"F6.imprint","IMPRINT",FACE,{"disambiguationData":[TD([[makeQuery(id+"F6.imprint","IMPRINT",EDGE,{"disambiguationData":[TD([[subQ2,-1.0]])],"derivedFrom":subQ1}),1.0]])]});}
            var Q207;
            {var subQ0=sQuery(id+"F6.wireOp",EDGE,"E198");var subQ1=sQuery(id+"F6.wireOp",EDGE,"E145");var subQ2=makeQuery(id+"F6.imprint","INTERSECT",VERTEX,{"derivedFrom":[subQ1,subQ0]});Q207=makeQuery(id+"F6.imprint","IMPRINT",FACE,{"disambiguationData":[TD([[makeQuery(id+"F6.imprint","IMPRINT",EDGE,{"disambiguationData":[TD([[subQ2,-1.0]])],"derivedFrom":subQ1}),1.0]])]});}
            var Q208;
            {var subQ0=sQuery(id+"F6.wireOp",EDGE,"E198");var subQ1=sQuery(id+"F6.wireOp",EDGE,"E147");var subQ2=makeQuery(id+"F6.imprint","INTERSECT",VERTEX,{"derivedFrom":[subQ1,subQ0]});Q208=makeQuery(id+"F6.imprint","IMPRINT",FACE,{"disambiguationData":[TD([[makeQuery(id+"F6.imprint","IMPRINT",EDGE,{"disambiguationData":[TD([[subQ2,-1.0]])],"derivedFrom":subQ1}),1.0]])]});}
            var Q209;
            {var subQ0=sQuery(id+"F6.wireOp",EDGE,"E198");var subQ1=sQuery(id+"F6.wireOp",EDGE,"E149");var subQ2=makeQuery(id+"F6.imprint","INTERSECT",VERTEX,{"derivedFrom":[subQ1,subQ0]});Q209=makeQuery(id+"F6.imprint","IMPRINT",FACE,{"disambiguationData":[TD([[makeQuery(id+"F6.imprint","IMPRINT",EDGE,{"disambiguationData":[TD([[subQ2,-1.0]])],"derivedFrom":subQ1}),1.0]])]});}
            var Q210;
            {var subQ0=sQuery(id+"F6.wireOp",EDGE,"E198");var subQ1=sQuery(id+"F6.wireOp",EDGE,"E151");var subQ2=makeQuery(id+"F6.imprint","INTERSECT",VERTEX,{"derivedFrom":[subQ1,subQ0]});Q210=makeQuery(id+"F6.imprint","IMPRINT",FACE,{"disambiguationData":[TD([[makeQuery(id+"F6.imprint","IMPRINT",EDGE,{"disambiguationData":[TD([[subQ2,-1.0]])],"derivedFrom":subQ1}),1.0]])]});}
            var Q211;
            {var subQ0=sQuery(id+"F6.wireOp",EDGE,"E198");var subQ1=sQuery(id+"F6.wireOp",EDGE,"E155");var subQ2=makeQuery(id+"F6.imprint","INTERSECT",VERTEX,{"derivedFrom":[subQ1,subQ0]});Q211=makeQuery(id+"F6.imprint","IMPRINT",FACE,{"disambiguationData":[TD([[makeQuery(id+"F6.imprint","IMPRINT",EDGE,{"disambiguationData":[TD([[subQ2,-1.0]])],"derivedFrom":subQ1}),1.0]])]});}
            var Q212;
            {var subQ0=sQuery(id+"F6.wireOp",EDGE,"E198");var subQ1=sQuery(id+"F6.wireOp",EDGE,"E153");var subQ2=makeQuery(id+"F6.imprint","INTERSECT",VERTEX,{"derivedFrom":[subQ1,subQ0]});Q212=makeQuery(id+"F6.imprint","IMPRINT",FACE,{"disambiguationData":[TD([[makeQuery(id+"F6.imprint","IMPRINT",EDGE,{"disambiguationData":[TD([[subQ2,-1.0]])],"derivedFrom":subQ1}),1.0]])]});}
            var Q213;
            {var subQ0=sQuery(id+"F6.wireOp",EDGE,"E198");var subQ1=sQuery(id+"F6.wireOp",EDGE,"E159");var subQ2=makeQuery(id+"F6.imprint","INTERSECT",VERTEX,{"derivedFrom":[subQ1,subQ0]});Q213=makeQuery(id+"F6.imprint","IMPRINT",FACE,{"disambiguationData":[TD([[makeQuery(id+"F6.imprint","IMPRINT",EDGE,{"disambiguationData":[TD([[subQ2,-1.0]])],"derivedFrom":subQ1}),1.0]])]});}
            var Q214;
            {var subQ0=sQuery(id+"F6.wireOp",EDGE,"E198");var subQ1=sQuery(id+"F6.wireOp",EDGE,"E157");var subQ2=makeQuery(id+"F6.imprint","INTERSECT",VERTEX,{"derivedFrom":[subQ1,subQ0]});Q214=makeQuery(id+"F6.imprint","IMPRINT",FACE,{"disambiguationData":[TD([[makeQuery(id+"F6.imprint","IMPRINT",EDGE,{"disambiguationData":[TD([[subQ2,-1.0]])],"derivedFrom":subQ1}),1.0]])]});}
            var Q215;
            {var subQ0=sQuery(id+"F6.wireOp",EDGE,"E198");var subQ1=sQuery(id+"F6.wireOp",EDGE,"E161");var subQ2=makeQuery(id+"F6.imprint","INTERSECT",VERTEX,{"derivedFrom":[subQ1,subQ0]});Q215=makeQuery(id+"F6.imprint","IMPRINT",FACE,{"disambiguationData":[TD([[makeQuery(id+"F6.imprint","IMPRINT",EDGE,{"disambiguationData":[TD([[subQ2,-1.0]])],"derivedFrom":subQ1}),1.0]])]});}
            var Q216;
            {var subQ0=sQuery(id+"F6.wireOp",EDGE,"E198");var subQ1=sQuery(id+"F6.wireOp",EDGE,"E163");var subQ2=makeQuery(id+"F6.imprint","INTERSECT",VERTEX,{"derivedFrom":[subQ1,subQ0]});Q216=makeQuery(id+"F6.imprint","IMPRINT",FACE,{"disambiguationData":[TD([[makeQuery(id+"F6.imprint","IMPRINT",EDGE,{"disambiguationData":[TD([[subQ2,-1.0]])],"derivedFrom":subQ1}),1.0]])]});}
            var Q217;
            {var subQ0=sQuery(id+"F6.wireOp",EDGE,"E198");var subQ1=sQuery(id+"F6.wireOp",EDGE,"E165");var subQ2=makeQuery(id+"F6.imprint","INTERSECT",VERTEX,{"derivedFrom":[subQ1,subQ0]});Q217=makeQuery(id+"F6.imprint","IMPRINT",FACE,{"disambiguationData":[TD([[makeQuery(id+"F6.imprint","IMPRINT",EDGE,{"disambiguationData":[TD([[subQ2,-1.0]])],"derivedFrom":subQ1}),1.0]])]});}
            var Q218;
            {var subQ0=sQuery(id+"F6.wireOp",EDGE,"E198");var subQ1=sQuery(id+"F6.wireOp",EDGE,"E169");var subQ2=makeQuery(id+"F6.imprint","INTERSECT",VERTEX,{"derivedFrom":[subQ1,subQ0]});Q218=makeQuery(id+"F6.imprint","IMPRINT",FACE,{"disambiguationData":[TD([[makeQuery(id+"F6.imprint","IMPRINT",EDGE,{"disambiguationData":[TD([[subQ2,-1.0]])],"derivedFrom":subQ1}),1.0]])]});}
            var Q219;
            {var subQ0=sQuery(id+"F6.wireOp",EDGE,"E200");var subQ1=sQuery(id+"F6.wireOp",EDGE,"E169");var subQ2=makeQuery(id+"F6.imprint","INTERSECT",VERTEX,{"derivedFrom":[subQ1,subQ0]});Q219=makeQuery(id+"F6.imprint","IMPRINT",FACE,{"disambiguationData":[TD([[makeQuery(id+"F6.imprint","IMPRINT",EDGE,{"disambiguationData":[TD([[subQ2,-1.0]])],"derivedFrom":subQ1}),1.0]])]});}
            var Q220;
            {var subQ0=sQuery(id+"F6.wireOp",EDGE,"E202");var subQ1=sQuery(id+"F6.wireOp",EDGE,"E169");var subQ2=makeQuery(id+"F6.imprint","INTERSECT",VERTEX,{"derivedFrom":[subQ1,subQ0]});Q220=makeQuery(id+"F6.imprint","IMPRINT",FACE,{"disambiguationData":[TD([[makeQuery(id+"F6.imprint","IMPRINT",EDGE,{"disambiguationData":[TD([[subQ2,-1.0]])],"derivedFrom":subQ1}),1.0]])]});}
            var Q221;
            {var subQ0=sQuery(id+"F6.wireOp",EDGE,"E168");Q221=makeQuery(id+"F6.imprint","IMPRINT",FACE,{"disambiguationData":[TD([[makeQuery(id+"F6.imprint","IMPRINT",EDGE,{"derivedFrom":subQ0}),1.0]])]});}
            var Q222;
            {var subQ0=sQuery(id+"F6.wireOp",EDGE,"E204");var subQ1=sQuery(id+"F6.wireOp",EDGE,"E165");var subQ2=makeQuery(id+"F6.imprint","INTERSECT",VERTEX,{"derivedFrom":[subQ1,subQ0]});Q222=makeQuery(id+"F6.imprint","IMPRINT",FACE,{"disambiguationData":[TD([[makeQuery(id+"F6.imprint","IMPRINT",EDGE,{"disambiguationData":[TD([[subQ2,-1.0]])],"derivedFrom":subQ1}),1.0]])]});}
            var Q223;
            {var subQ0=sQuery(id+"F6.wireOp",EDGE,"E207");var subQ1=sQuery(id+"F6.wireOp",EDGE,"E165");var subQ2=makeQuery(id+"F6.imprint","INTERSECT",VERTEX,{"derivedFrom":[subQ1,subQ0]});Q223=makeQuery(id+"F6.imprint","IMPRINT",FACE,{"disambiguationData":[TD([[makeQuery(id+"F6.imprint","IMPRINT",EDGE,{"disambiguationData":[TD([[subQ2,-1.0]])],"derivedFrom":subQ1}),1.0]])]});}
            var Q224;
            {var subQ0=sQuery(id+"F6.wireOp",EDGE,"E207");var subQ1=sQuery(id+"F6.wireOp",EDGE,"E163");var subQ2=makeQuery(id+"F6.imprint","INTERSECT",VERTEX,{"derivedFrom":[subQ1,subQ0]});Q224=makeQuery(id+"F6.imprint","IMPRINT",FACE,{"disambiguationData":[TD([[makeQuery(id+"F6.imprint","IMPRINT",EDGE,{"disambiguationData":[TD([[subQ2,-1.0]])],"derivedFrom":subQ1}),1.0]])]});}
            var Q225;
            {var subQ0=sQuery(id+"F6.wireOp",EDGE,"E207");var subQ1=sQuery(id+"F6.wireOp",EDGE,"E161");var subQ2=makeQuery(id+"F6.imprint","INTERSECT",VERTEX,{"derivedFrom":[subQ1,subQ0]});Q225=makeQuery(id+"F6.imprint","IMPRINT",FACE,{"disambiguationData":[TD([[makeQuery(id+"F6.imprint","IMPRINT",EDGE,{"disambiguationData":[TD([[subQ2,-1.0]])],"derivedFrom":subQ1}),1.0]])]});}
            var Q226;
            {var subQ0=sQuery(id+"F6.wireOp",EDGE,"E204");var subQ1=sQuery(id+"F6.wireOp",EDGE,"E161");var subQ2=makeQuery(id+"F6.imprint","INTERSECT",VERTEX,{"derivedFrom":[subQ1,subQ0]});Q226=makeQuery(id+"F6.imprint","IMPRINT",FACE,{"disambiguationData":[TD([[makeQuery(id+"F6.imprint","IMPRINT",EDGE,{"disambiguationData":[TD([[subQ2,-1.0]])],"derivedFrom":subQ1}),1.0]])]});}
            var Q227;
            {var subQ0=sQuery(id+"F6.wireOp",EDGE,"E204");var subQ1=sQuery(id+"F6.wireOp",EDGE,"E163");var subQ2=makeQuery(id+"F6.imprint","INTERSECT",VERTEX,{"derivedFrom":[subQ1,subQ0]});Q227=makeQuery(id+"F6.imprint","IMPRINT",FACE,{"disambiguationData":[TD([[makeQuery(id+"F6.imprint","IMPRINT",EDGE,{"disambiguationData":[TD([[subQ2,-1.0]])],"derivedFrom":subQ1}),1.0]])]});}
            var Q228;
            {var subQ0=sQuery(id+"F6.wireOp",EDGE,"E202");var subQ1=sQuery(id+"F6.wireOp",EDGE,"E163");var subQ2=makeQuery(id+"F6.imprint","INTERSECT",VERTEX,{"derivedFrom":[subQ1,subQ0]});Q228=makeQuery(id+"F6.imprint","IMPRINT",FACE,{"disambiguationData":[TD([[makeQuery(id+"F6.imprint","IMPRINT",EDGE,{"disambiguationData":[TD([[subQ2,-1.0]])],"derivedFrom":subQ1}),1.0]])]});}
            var Q229;
            {var subQ0=sQuery(id+"F6.wireOp",EDGE,"E202");var subQ1=sQuery(id+"F6.wireOp",EDGE,"E165");var subQ2=makeQuery(id+"F6.imprint","INTERSECT",VERTEX,{"derivedFrom":[subQ1,subQ0]});Q229=makeQuery(id+"F6.imprint","IMPRINT",FACE,{"disambiguationData":[TD([[makeQuery(id+"F6.imprint","IMPRINT",EDGE,{"disambiguationData":[TD([[subQ2,-1.0]])],"derivedFrom":subQ1}),1.0]])]});}
            var Q230;
            {var subQ0=sQuery(id+"F6.wireOp",EDGE,"E200");var subQ1=sQuery(id+"F6.wireOp",EDGE,"E165");var subQ2=makeQuery(id+"F6.imprint","INTERSECT",VERTEX,{"derivedFrom":[subQ1,subQ0]});Q230=makeQuery(id+"F6.imprint","IMPRINT",FACE,{"disambiguationData":[TD([[makeQuery(id+"F6.imprint","IMPRINT",EDGE,{"disambiguationData":[TD([[subQ2,-1.0]])],"derivedFrom":subQ1}),1.0]])]});}
            var Q231;
            {var subQ0=sQuery(id+"F6.wireOp",EDGE,"E200");var subQ1=sQuery(id+"F6.wireOp",EDGE,"E163");var subQ2=makeQuery(id+"F6.imprint","INTERSECT",VERTEX,{"derivedFrom":[subQ1,subQ0]});Q231=makeQuery(id+"F6.imprint","IMPRINT",FACE,{"disambiguationData":[TD([[makeQuery(id+"F6.imprint","IMPRINT",EDGE,{"disambiguationData":[TD([[subQ2,-1.0]])],"derivedFrom":subQ1}),1.0]])]});}
            var Q232;
            {var subQ0=sQuery(id+"F6.wireOp",EDGE,"E200");var subQ1=sQuery(id+"F6.wireOp",EDGE,"E161");var subQ2=makeQuery(id+"F6.imprint","INTERSECT",VERTEX,{"derivedFrom":[subQ1,subQ0]});Q232=makeQuery(id+"F6.imprint","IMPRINT",FACE,{"disambiguationData":[TD([[makeQuery(id+"F6.imprint","IMPRINT",EDGE,{"disambiguationData":[TD([[subQ2,-1.0]])],"derivedFrom":subQ1}),1.0]])]});}
            var Q233;
            {var subQ0=sQuery(id+"F6.wireOp",EDGE,"E202");var subQ1=sQuery(id+"F6.wireOp",EDGE,"E161");var subQ2=makeQuery(id+"F6.imprint","INTERSECT",VERTEX,{"derivedFrom":[subQ1,subQ0]});Q233=makeQuery(id+"F6.imprint","IMPRINT",FACE,{"disambiguationData":[TD([[makeQuery(id+"F6.imprint","IMPRINT",EDGE,{"disambiguationData":[TD([[subQ2,-1.0]])],"derivedFrom":subQ1}),1.0]])]});}
            var Q234;
            {var subQ0=sQuery(id+"F6.wireOp",EDGE,"E202");var subQ1=sQuery(id+"F6.wireOp",EDGE,"E159");var subQ2=makeQuery(id+"F6.imprint","INTERSECT",VERTEX,{"derivedFrom":[subQ1,subQ0]});Q234=makeQuery(id+"F6.imprint","IMPRINT",FACE,{"disambiguationData":[TD([[makeQuery(id+"F6.imprint","IMPRINT",EDGE,{"disambiguationData":[TD([[subQ2,-1.0]])],"derivedFrom":subQ1}),1.0]])]});}
            var Q235;
            {var subQ0=sQuery(id+"F6.wireOp",EDGE,"E200");var subQ1=sQuery(id+"F6.wireOp",EDGE,"E159");var subQ2=makeQuery(id+"F6.imprint","INTERSECT",VERTEX,{"derivedFrom":[subQ1,subQ0]});Q235=makeQuery(id+"F6.imprint","IMPRINT",FACE,{"disambiguationData":[TD([[makeQuery(id+"F6.imprint","IMPRINT",EDGE,{"disambiguationData":[TD([[subQ2,-1.0]])],"derivedFrom":subQ1}),1.0]])]});}
            var Q236;
            {var subQ0=sQuery(id+"F6.wireOp",EDGE,"E200");var subQ1=sQuery(id+"F6.wireOp",EDGE,"E157");var subQ2=makeQuery(id+"F6.imprint","INTERSECT",VERTEX,{"derivedFrom":[subQ1,subQ0]});Q236=makeQuery(id+"F6.imprint","IMPRINT",FACE,{"disambiguationData":[TD([[makeQuery(id+"F6.imprint","IMPRINT",EDGE,{"disambiguationData":[TD([[subQ2,-1.0]])],"derivedFrom":subQ1}),1.0]])]});}
            var Q237;
            {var subQ0=sQuery(id+"F6.wireOp",EDGE,"E202");var subQ1=sQuery(id+"F6.wireOp",EDGE,"E157");var subQ2=makeQuery(id+"F6.imprint","INTERSECT",VERTEX,{"derivedFrom":[subQ1,subQ0]});Q237=makeQuery(id+"F6.imprint","IMPRINT",FACE,{"disambiguationData":[TD([[makeQuery(id+"F6.imprint","IMPRINT",EDGE,{"disambiguationData":[TD([[subQ2,-1.0]])],"derivedFrom":subQ1}),1.0]])]});}
            var Q238;
            {var subQ0=sQuery(id+"F6.wireOp",EDGE,"E202");var subQ1=sQuery(id+"F6.wireOp",EDGE,"E155");var subQ2=makeQuery(id+"F6.imprint","INTERSECT",VERTEX,{"derivedFrom":[subQ1,subQ0]});Q238=makeQuery(id+"F6.imprint","IMPRINT",FACE,{"disambiguationData":[TD([[makeQuery(id+"F6.imprint","IMPRINT",EDGE,{"disambiguationData":[TD([[subQ2,-1.0]])],"derivedFrom":subQ1}),1.0]])]});}
            var Q239;
            {var subQ0=sQuery(id+"F6.wireOp",EDGE,"E200");var subQ1=sQuery(id+"F6.wireOp",EDGE,"E155");var subQ2=makeQuery(id+"F6.imprint","INTERSECT",VERTEX,{"derivedFrom":[subQ1,subQ0]});Q239=makeQuery(id+"F6.imprint","IMPRINT",FACE,{"disambiguationData":[TD([[makeQuery(id+"F6.imprint","IMPRINT",EDGE,{"disambiguationData":[TD([[subQ2,-1.0]])],"derivedFrom":subQ1}),1.0]])]});}
            var Q240;
            {var subQ0=sQuery(id+"F6.wireOp",EDGE,"E200");var subQ1=sQuery(id+"F6.wireOp",EDGE,"E153");var subQ2=makeQuery(id+"F6.imprint","INTERSECT",VERTEX,{"derivedFrom":[subQ1,subQ0]});Q240=makeQuery(id+"F6.imprint","IMPRINT",FACE,{"disambiguationData":[TD([[makeQuery(id+"F6.imprint","IMPRINT",EDGE,{"disambiguationData":[TD([[subQ2,-1.0]])],"derivedFrom":subQ1}),1.0]])]});}
            var Q241;
            {var subQ0=sQuery(id+"F6.wireOp",EDGE,"E202");var subQ1=sQuery(id+"F6.wireOp",EDGE,"E153");var subQ2=makeQuery(id+"F6.imprint","INTERSECT",VERTEX,{"derivedFrom":[subQ1,subQ0]});Q241=makeQuery(id+"F6.imprint","IMPRINT",FACE,{"disambiguationData":[TD([[makeQuery(id+"F6.imprint","IMPRINT",EDGE,{"disambiguationData":[TD([[subQ2,-1.0]])],"derivedFrom":subQ1}),1.0]])]});}
            var Q242;
            {var subQ0=sQuery(id+"F6.wireOp",EDGE,"E202");var subQ1=sQuery(id+"F6.wireOp",EDGE,"E151");var subQ2=makeQuery(id+"F6.imprint","INTERSECT",VERTEX,{"derivedFrom":[subQ1,subQ0]});Q242=makeQuery(id+"F6.imprint","IMPRINT",FACE,{"disambiguationData":[TD([[makeQuery(id+"F6.imprint","IMPRINT",EDGE,{"disambiguationData":[TD([[subQ2,-1.0]])],"derivedFrom":subQ1}),1.0]])]});}
            var Q243;
            {var subQ0=sQuery(id+"F6.wireOp",EDGE,"E200");var subQ1=sQuery(id+"F6.wireOp",EDGE,"E151");var subQ2=makeQuery(id+"F6.imprint","INTERSECT",VERTEX,{"derivedFrom":[subQ1,subQ0]});Q243=makeQuery(id+"F6.imprint","IMPRINT",FACE,{"disambiguationData":[TD([[makeQuery(id+"F6.imprint","IMPRINT",EDGE,{"disambiguationData":[TD([[subQ2,-1.0]])],"derivedFrom":subQ1}),1.0]])]});}
            var Q244;
            {var subQ0=sQuery(id+"F6.wireOp",EDGE,"E200");var subQ1=sQuery(id+"F6.wireOp",EDGE,"E149");var subQ2=makeQuery(id+"F6.imprint","INTERSECT",VERTEX,{"derivedFrom":[subQ1,subQ0]});Q244=makeQuery(id+"F6.imprint","IMPRINT",FACE,{"disambiguationData":[TD([[makeQuery(id+"F6.imprint","IMPRINT",EDGE,{"disambiguationData":[TD([[subQ2,-1.0]])],"derivedFrom":subQ1}),1.0]])]});}
            var Q245;
            {var subQ0=sQuery(id+"F6.wireOp",EDGE,"E202");var subQ1=sQuery(id+"F6.wireOp",EDGE,"E149");var subQ2=makeQuery(id+"F6.imprint","INTERSECT",VERTEX,{"derivedFrom":[subQ1,subQ0]});Q245=makeQuery(id+"F6.imprint","IMPRINT",FACE,{"disambiguationData":[TD([[makeQuery(id+"F6.imprint","IMPRINT",EDGE,{"disambiguationData":[TD([[subQ2,-1.0]])],"derivedFrom":subQ1}),1.0]])]});}
            var Q246;
            {var subQ0=sQuery(id+"F6.wireOp",EDGE,"E202");var subQ1=sQuery(id+"F6.wireOp",EDGE,"E147");var subQ2=makeQuery(id+"F6.imprint","INTERSECT",VERTEX,{"derivedFrom":[subQ1,subQ0]});Q246=makeQuery(id+"F6.imprint","IMPRINT",FACE,{"disambiguationData":[TD([[makeQuery(id+"F6.imprint","IMPRINT",EDGE,{"disambiguationData":[TD([[subQ2,-1.0]])],"derivedFrom":subQ1}),1.0]])]});}
            var Q247;
            {var subQ0=sQuery(id+"F6.wireOp",EDGE,"E200");var subQ1=sQuery(id+"F6.wireOp",EDGE,"E147");var subQ2=makeQuery(id+"F6.imprint","INTERSECT",VERTEX,{"derivedFrom":[subQ1,subQ0]});Q247=makeQuery(id+"F6.imprint","IMPRINT",FACE,{"disambiguationData":[TD([[makeQuery(id+"F6.imprint","IMPRINT",EDGE,{"disambiguationData":[TD([[subQ2,-1.0]])],"derivedFrom":subQ1}),1.0]])]});}
            var Q248;
            {var subQ0=sQuery(id+"F6.wireOp",EDGE,"E200");var subQ1=sQuery(id+"F6.wireOp",EDGE,"E145");var subQ2=makeQuery(id+"F6.imprint","INTERSECT",VERTEX,{"derivedFrom":[subQ1,subQ0]});Q248=makeQuery(id+"F6.imprint","IMPRINT",FACE,{"disambiguationData":[TD([[makeQuery(id+"F6.imprint","IMPRINT",EDGE,{"disambiguationData":[TD([[subQ2,-1.0]])],"derivedFrom":subQ1}),1.0]])]});}
            var Q249;
            {var subQ0=sQuery(id+"F6.wireOp",EDGE,"E202");var subQ1=sQuery(id+"F6.wireOp",EDGE,"E145");var subQ2=makeQuery(id+"F6.imprint","INTERSECT",VERTEX,{"derivedFrom":[subQ1,subQ0]});Q249=makeQuery(id+"F6.imprint","IMPRINT",FACE,{"disambiguationData":[TD([[makeQuery(id+"F6.imprint","IMPRINT",EDGE,{"disambiguationData":[TD([[subQ2,-1.0]])],"derivedFrom":subQ1}),1.0]])]});}
            var Q250;
            {var subQ0=sQuery(id+"F6.wireOp",EDGE,"E202");var subQ1=sQuery(id+"F6.wireOp",EDGE,"E143");var subQ2=makeQuery(id+"F6.imprint","INTERSECT",VERTEX,{"derivedFrom":[subQ1,subQ0]});Q250=makeQuery(id+"F6.imprint","IMPRINT",FACE,{"disambiguationData":[TD([[makeQuery(id+"F6.imprint","IMPRINT",EDGE,{"disambiguationData":[TD([[subQ2,-1.0]])],"derivedFrom":subQ1}),1.0]])]});}
            var Q251;
            {var subQ0=sQuery(id+"F6.wireOp",EDGE,"E200");var subQ1=sQuery(id+"F6.wireOp",EDGE,"E143");var subQ2=makeQuery(id+"F6.imprint","INTERSECT",VERTEX,{"derivedFrom":[subQ1,subQ0]});Q251=makeQuery(id+"F6.imprint","IMPRINT",FACE,{"disambiguationData":[TD([[makeQuery(id+"F6.imprint","IMPRINT",EDGE,{"disambiguationData":[TD([[subQ2,-1.0]])],"derivedFrom":subQ1}),1.0]])]});}
            var Q252;
            {var subQ0=sQuery(id+"F6.wireOp",EDGE,"E200");var subQ1=sQuery(id+"F6.wireOp",EDGE,"E141");var subQ2=makeQuery(id+"F6.imprint","INTERSECT",VERTEX,{"derivedFrom":[subQ1,subQ0]});Q252=makeQuery(id+"F6.imprint","IMPRINT",FACE,{"disambiguationData":[TD([[makeQuery(id+"F6.imprint","IMPRINT",EDGE,{"disambiguationData":[TD([[subQ2,-1.0]])],"derivedFrom":subQ1}),1.0]])]});}
            var Q253;
            {var subQ0=sQuery(id+"F6.wireOp",EDGE,"E202");var subQ1=sQuery(id+"F6.wireOp",EDGE,"E141");var subQ2=makeQuery(id+"F6.imprint","INTERSECT",VERTEX,{"derivedFrom":[subQ1,subQ0]});Q253=makeQuery(id+"F6.imprint","IMPRINT",FACE,{"disambiguationData":[TD([[makeQuery(id+"F6.imprint","IMPRINT",EDGE,{"disambiguationData":[TD([[subQ2,-1.0]])],"derivedFrom":subQ1}),1.0]])]});}
            var Q254;
            {var subQ0=sQuery(id+"F6.wireOp",EDGE,"E202");var subQ1=sQuery(id+"F6.wireOp",EDGE,"E139");var subQ2=makeQuery(id+"F6.imprint","INTERSECT",VERTEX,{"derivedFrom":[subQ1,subQ0]});Q254=makeQuery(id+"F6.imprint","IMPRINT",FACE,{"disambiguationData":[TD([[makeQuery(id+"F6.imprint","IMPRINT",EDGE,{"disambiguationData":[TD([[subQ2,-1.0]])],"derivedFrom":subQ1}),1.0]])]});}
            var Q255;
            {var subQ0=sQuery(id+"F6.wireOp",EDGE,"E200");var subQ1=sQuery(id+"F6.wireOp",EDGE,"E139");var subQ2=makeQuery(id+"F6.imprint","INTERSECT",VERTEX,{"derivedFrom":[subQ1,subQ0]});Q255=makeQuery(id+"F6.imprint","IMPRINT",FACE,{"disambiguationData":[TD([[makeQuery(id+"F6.imprint","IMPRINT",EDGE,{"disambiguationData":[TD([[subQ2,-1.0]])],"derivedFrom":subQ1}),1.0]])]});}
            var Q256;
            {var subQ0=sQuery(id+"F6.wireOp",EDGE,"E200");var subQ1=sQuery(id+"F6.wireOp",EDGE,"E137");var subQ2=makeQuery(id+"F6.imprint","INTERSECT",VERTEX,{"derivedFrom":[subQ1,subQ0]});Q256=makeQuery(id+"F6.imprint","IMPRINT",FACE,{"disambiguationData":[TD([[makeQuery(id+"F6.imprint","IMPRINT",EDGE,{"disambiguationData":[TD([[subQ2,-1.0]])],"derivedFrom":subQ1}),1.0]])]});}
            var Q257;
            {var subQ0=sQuery(id+"F6.wireOp",EDGE,"E202");var subQ1=sQuery(id+"F6.wireOp",EDGE,"E137");var subQ2=makeQuery(id+"F6.imprint","INTERSECT",VERTEX,{"derivedFrom":[subQ1,subQ0]});Q257=makeQuery(id+"F6.imprint","IMPRINT",FACE,{"disambiguationData":[TD([[makeQuery(id+"F6.imprint","IMPRINT",EDGE,{"disambiguationData":[TD([[subQ2,-1.0]])],"derivedFrom":subQ1}),1.0]])]});}
            var Q258;
            {var subQ0=sQuery(id+"F6.wireOp",EDGE,"E202");var subQ1=sQuery(id+"F6.wireOp",EDGE,"E135");var subQ2=makeQuery(id+"F6.imprint","INTERSECT",VERTEX,{"derivedFrom":[subQ1,subQ0]});Q258=makeQuery(id+"F6.imprint","IMPRINT",FACE,{"disambiguationData":[TD([[makeQuery(id+"F6.imprint","IMPRINT",EDGE,{"disambiguationData":[TD([[subQ2,-1.0]])],"derivedFrom":subQ1}),1.0]])]});}
            var Q259;
            {var subQ0=sQuery(id+"F6.wireOp",EDGE,"E200");var subQ1=sQuery(id+"F6.wireOp",EDGE,"E135");var subQ2=makeQuery(id+"F6.imprint","INTERSECT",VERTEX,{"derivedFrom":[subQ1,subQ0]});Q259=makeQuery(id+"F6.imprint","IMPRINT",FACE,{"disambiguationData":[TD([[makeQuery(id+"F6.imprint","IMPRINT",EDGE,{"disambiguationData":[TD([[subQ2,-1.0]])],"derivedFrom":subQ1}),1.0]])]});}
            var Q260;
            {var subQ0=sQuery(id+"F6.wireOp",EDGE,"E133");Q260=makeQuery(id+"F6.imprint","IMPRINT",FACE,{"disambiguationData":[TD([[makeQuery(id+"F6.imprint","IMPRINT",EDGE,{"derivedFrom":subQ0}),1.0]])]});}
            var Q261;
            {var subQ0=sQuery(id+"F6.wireOp",EDGE,"E204");var subQ5=sQuery(id+"F6.wireOp",EDGE,"E138");var subQ6=makeQuery(id+"F6.imprint","INTERSECT",VERTEX,{"derivedFrom":[subQ5,subQ0]});Q261=makeQuery(id+"F6.imprint","IMPRINT",FACE,{"disambiguationData":[TD([[makeQuery(id+"F6.imprint","IMPRINT",EDGE,{"disambiguationData":[TD([[subQ6,-1.0]])],"derivedFrom":subQ5}),-1.0]])]});}
            var Q262;
            {var subQ0=sQuery(id+"F6.wireOp",EDGE,"E62");Q262=makeQuery(id+"F6.imprint","IMPRINT",FACE,{"disambiguationData":[TD([[makeQuery(id+"F6.imprint","IMPRINT",EDGE,{"derivedFrom":subQ0}),1.0]])]});}
            var Q263;
            {var subQ0=sQuery(id+"F6.wireOp",EDGE,"E207");var subQ1=sQuery(id+"F6.wireOp",EDGE,"E139");var subQ2=makeQuery(id+"F6.imprint","INTERSECT",VERTEX,{"derivedFrom":[subQ1,subQ0]});Q263=makeQuery(id+"F6.imprint","IMPRINT",FACE,{"disambiguationData":[TD([[makeQuery(id+"F6.imprint","IMPRINT",EDGE,{"disambiguationData":[TD([[subQ2,-1.0]])],"derivedFrom":subQ1}),1.0]])]});}
            var Q264;
            {var subQ0=sQuery(id+"F6.wireOp",EDGE,"E204");var subQ1=sQuery(id+"F6.wireOp",EDGE,"E139");var subQ2=makeQuery(id+"F6.imprint","INTERSECT",VERTEX,{"derivedFrom":[subQ1,subQ0]});Q264=makeQuery(id+"F6.imprint","IMPRINT",FACE,{"disambiguationData":[TD([[makeQuery(id+"F6.imprint","IMPRINT",EDGE,{"disambiguationData":[TD([[subQ2,-1.0]])],"derivedFrom":subQ1}),1.0]])]});}
            var Q265;
            {var subQ0=sQuery(id+"F6.wireOp",EDGE,"E204");var subQ1=sQuery(id+"F6.wireOp",EDGE,"E141");var subQ2=makeQuery(id+"F6.imprint","INTERSECT",VERTEX,{"derivedFrom":[subQ1,subQ0]});Q265=makeQuery(id+"F6.imprint","IMPRINT",FACE,{"disambiguationData":[TD([[makeQuery(id+"F6.imprint","IMPRINT",EDGE,{"disambiguationData":[TD([[subQ2,-1.0]])],"derivedFrom":subQ1}),1.0]])]});}
            var Q266;
            {var subQ0=sQuery(id+"F6.wireOp",EDGE,"E207");var subQ1=sQuery(id+"F6.wireOp",EDGE,"E141");var subQ2=makeQuery(id+"F6.imprint","INTERSECT",VERTEX,{"derivedFrom":[subQ1,subQ0]});Q266=makeQuery(id+"F6.imprint","IMPRINT",FACE,{"disambiguationData":[TD([[makeQuery(id+"F6.imprint","IMPRINT",EDGE,{"disambiguationData":[TD([[subQ2,-1.0]])],"derivedFrom":subQ1}),1.0]])]});}
            var Q267;
            {var subQ0=sQuery(id+"F6.wireOp",EDGE,"E207");var subQ1=sQuery(id+"F6.wireOp",EDGE,"E143");var subQ2=makeQuery(id+"F6.imprint","INTERSECT",VERTEX,{"derivedFrom":[subQ1,subQ0]});Q267=makeQuery(id+"F6.imprint","IMPRINT",FACE,{"disambiguationData":[TD([[makeQuery(id+"F6.imprint","IMPRINT",EDGE,{"disambiguationData":[TD([[subQ2,-1.0]])],"derivedFrom":subQ1}),1.0]])]});}
            var Q268;
            {var subQ0=sQuery(id+"F6.wireOp",EDGE,"E204");var subQ1=sQuery(id+"F6.wireOp",EDGE,"E143");var subQ2=makeQuery(id+"F6.imprint","INTERSECT",VERTEX,{"derivedFrom":[subQ1,subQ0]});Q268=makeQuery(id+"F6.imprint","IMPRINT",FACE,{"disambiguationData":[TD([[makeQuery(id+"F6.imprint","IMPRINT",EDGE,{"disambiguationData":[TD([[subQ2,-1.0]])],"derivedFrom":subQ1}),1.0]])]});}
            var Q269;
            {var subQ0=sQuery(id+"F6.wireOp",EDGE,"E204");var subQ1=sQuery(id+"F6.wireOp",EDGE,"E145");var subQ2=makeQuery(id+"F6.imprint","INTERSECT",VERTEX,{"derivedFrom":[subQ1,subQ0]});Q269=makeQuery(id+"F6.imprint","IMPRINT",FACE,{"disambiguationData":[TD([[makeQuery(id+"F6.imprint","IMPRINT",EDGE,{"disambiguationData":[TD([[subQ2,-1.0]])],"derivedFrom":subQ1}),1.0]])]});}
            var Q270;
            {var subQ0=sQuery(id+"F6.wireOp",EDGE,"E207");var subQ1=sQuery(id+"F6.wireOp",EDGE,"E145");var subQ2=makeQuery(id+"F6.imprint","INTERSECT",VERTEX,{"derivedFrom":[subQ1,subQ0]});Q270=makeQuery(id+"F6.imprint","IMPRINT",FACE,{"disambiguationData":[TD([[makeQuery(id+"F6.imprint","IMPRINT",EDGE,{"disambiguationData":[TD([[subQ2,-1.0]])],"derivedFrom":subQ1}),1.0]])]});}
            var Q271;
            {var subQ0=sQuery(id+"F6.wireOp",EDGE,"E207");var subQ1=sQuery(id+"F6.wireOp",EDGE,"E147");var subQ2=makeQuery(id+"F6.imprint","INTERSECT",VERTEX,{"derivedFrom":[subQ1,subQ0]});Q271=makeQuery(id+"F6.imprint","IMPRINT",FACE,{"disambiguationData":[TD([[makeQuery(id+"F6.imprint","IMPRINT",EDGE,{"disambiguationData":[TD([[subQ2,-1.0]])],"derivedFrom":subQ1}),1.0]])]});}
            var Q272;
            {var subQ0=sQuery(id+"F6.wireOp",EDGE,"E204");var subQ1=sQuery(id+"F6.wireOp",EDGE,"E147");var subQ2=makeQuery(id+"F6.imprint","INTERSECT",VERTEX,{"derivedFrom":[subQ1,subQ0]});Q272=makeQuery(id+"F6.imprint","IMPRINT",FACE,{"disambiguationData":[TD([[makeQuery(id+"F6.imprint","IMPRINT",EDGE,{"disambiguationData":[TD([[subQ2,-1.0]])],"derivedFrom":subQ1}),1.0]])]});}
            var Q273;
            {var subQ0=sQuery(id+"F6.wireOp",EDGE,"E204");var subQ1=sQuery(id+"F6.wireOp",EDGE,"E149");var subQ2=makeQuery(id+"F6.imprint","INTERSECT",VERTEX,{"derivedFrom":[subQ1,subQ0]});Q273=makeQuery(id+"F6.imprint","IMPRINT",FACE,{"disambiguationData":[TD([[makeQuery(id+"F6.imprint","IMPRINT",EDGE,{"disambiguationData":[TD([[subQ2,-1.0]])],"derivedFrom":subQ1}),1.0]])]});}
            var Q274;
            {var subQ0=sQuery(id+"F6.wireOp",EDGE,"E207");var subQ1=sQuery(id+"F6.wireOp",EDGE,"E149");var subQ2=makeQuery(id+"F6.imprint","INTERSECT",VERTEX,{"derivedFrom":[subQ1,subQ0]});Q274=makeQuery(id+"F6.imprint","IMPRINT",FACE,{"disambiguationData":[TD([[makeQuery(id+"F6.imprint","IMPRINT",EDGE,{"disambiguationData":[TD([[subQ2,-1.0]])],"derivedFrom":subQ1}),1.0]])]});}
            var Q275;
            {var subQ0=sQuery(id+"F6.wireOp",EDGE,"E207");var subQ1=sQuery(id+"F6.wireOp",EDGE,"E151");var subQ2=makeQuery(id+"F6.imprint","INTERSECT",VERTEX,{"derivedFrom":[subQ1,subQ0]});Q275=makeQuery(id+"F6.imprint","IMPRINT",FACE,{"disambiguationData":[TD([[makeQuery(id+"F6.imprint","IMPRINT",EDGE,{"disambiguationData":[TD([[subQ2,-1.0]])],"derivedFrom":subQ1}),1.0]])]});}
            var Q276;
            {var subQ0=sQuery(id+"F6.wireOp",EDGE,"E204");var subQ1=sQuery(id+"F6.wireOp",EDGE,"E151");var subQ2=makeQuery(id+"F6.imprint","INTERSECT",VERTEX,{"derivedFrom":[subQ1,subQ0]});Q276=makeQuery(id+"F6.imprint","IMPRINT",FACE,{"disambiguationData":[TD([[makeQuery(id+"F6.imprint","IMPRINT",EDGE,{"disambiguationData":[TD([[subQ2,-1.0]])],"derivedFrom":subQ1}),1.0]])]});}
            var Q277;
            {var subQ0=sQuery(id+"F6.wireOp",EDGE,"E204");var subQ1=sQuery(id+"F6.wireOp",EDGE,"E153");var subQ2=makeQuery(id+"F6.imprint","INTERSECT",VERTEX,{"derivedFrom":[subQ1,subQ0]});Q277=makeQuery(id+"F6.imprint","IMPRINT",FACE,{"disambiguationData":[TD([[makeQuery(id+"F6.imprint","IMPRINT",EDGE,{"disambiguationData":[TD([[subQ2,-1.0]])],"derivedFrom":subQ1}),1.0]])]});}
            var Q278;
            {var subQ0=sQuery(id+"F6.wireOp",EDGE,"E207");var subQ1=sQuery(id+"F6.wireOp",EDGE,"E153");var subQ2=makeQuery(id+"F6.imprint","INTERSECT",VERTEX,{"derivedFrom":[subQ1,subQ0]});Q278=makeQuery(id+"F6.imprint","IMPRINT",FACE,{"disambiguationData":[TD([[makeQuery(id+"F6.imprint","IMPRINT",EDGE,{"disambiguationData":[TD([[subQ2,-1.0]])],"derivedFrom":subQ1}),1.0]])]});}
            var Q279;
            {var subQ0=sQuery(id+"F6.wireOp",EDGE,"E207");var subQ1=sQuery(id+"F6.wireOp",EDGE,"E155");var subQ2=makeQuery(id+"F6.imprint","INTERSECT",VERTEX,{"derivedFrom":[subQ1,subQ0]});Q279=makeQuery(id+"F6.imprint","IMPRINT",FACE,{"disambiguationData":[TD([[makeQuery(id+"F6.imprint","IMPRINT",EDGE,{"disambiguationData":[TD([[subQ2,-1.0]])],"derivedFrom":subQ1}),1.0]])]});}
            var Q280;
            {var subQ0=sQuery(id+"F6.wireOp",EDGE,"E204");var subQ1=sQuery(id+"F6.wireOp",EDGE,"E155");var subQ2=makeQuery(id+"F6.imprint","INTERSECT",VERTEX,{"derivedFrom":[subQ1,subQ0]});Q280=makeQuery(id+"F6.imprint","IMPRINT",FACE,{"disambiguationData":[TD([[makeQuery(id+"F6.imprint","IMPRINT",EDGE,{"disambiguationData":[TD([[subQ2,-1.0]])],"derivedFrom":subQ1}),1.0]])]});}
            var Q281;
            {var subQ0=sQuery(id+"F6.wireOp",EDGE,"E204");var subQ1=sQuery(id+"F6.wireOp",EDGE,"E157");var subQ2=makeQuery(id+"F6.imprint","INTERSECT",VERTEX,{"derivedFrom":[subQ1,subQ0]});Q281=makeQuery(id+"F6.imprint","IMPRINT",FACE,{"disambiguationData":[TD([[makeQuery(id+"F6.imprint","IMPRINT",EDGE,{"disambiguationData":[TD([[subQ2,-1.0]])],"derivedFrom":subQ1}),1.0]])]});}
            var Q282;
            {var subQ0=sQuery(id+"F6.wireOp",EDGE,"E207");var subQ1=sQuery(id+"F6.wireOp",EDGE,"E157");var subQ2=makeQuery(id+"F6.imprint","INTERSECT",VERTEX,{"derivedFrom":[subQ1,subQ0]});Q282=makeQuery(id+"F6.imprint","IMPRINT",FACE,{"disambiguationData":[TD([[makeQuery(id+"F6.imprint","IMPRINT",EDGE,{"disambiguationData":[TD([[subQ2,-1.0]])],"derivedFrom":subQ1}),1.0]])]});}
            var Q283;
            {var subQ0=sQuery(id+"F6.wireOp",EDGE,"E207");var subQ1=sQuery(id+"F6.wireOp",EDGE,"E159");var subQ2=makeQuery(id+"F6.imprint","INTERSECT",VERTEX,{"derivedFrom":[subQ1,subQ0]});Q283=makeQuery(id+"F6.imprint","IMPRINT",FACE,{"disambiguationData":[TD([[makeQuery(id+"F6.imprint","IMPRINT",EDGE,{"disambiguationData":[TD([[subQ2,-1.0]])],"derivedFrom":subQ1}),1.0]])]});}
            var Q284;
            {var subQ0=sQuery(id+"F6.wireOp",EDGE,"E204");var subQ1=sQuery(id+"F6.wireOp",EDGE,"E159");var subQ2=makeQuery(id+"F6.imprint","INTERSECT",VERTEX,{"derivedFrom":[subQ1,subQ0]});Q284=makeQuery(id+"F6.imprint","IMPRINT",FACE,{"disambiguationData":[TD([[makeQuery(id+"F6.imprint","IMPRINT",EDGE,{"disambiguationData":[TD([[subQ2,-1.0]])],"derivedFrom":subQ1}),1.0]])]});}
            extrude(context, id + "F7", {"entities" : qUnion([Q0, Q1, Q2, Q3, Q4, Q5, Q6, Q7, Q8, Q9, Q10, Q11, Q12, Q13, Q14, Q15, Q16, Q17, Q18, Q19, Q20, Q21, Q22, Q23, Q24, Q25, Q26, Q27, Q28, Q29, Q30, Q31, Q32, Q33, Q34, Q35, Q36, Q37, Q38, Q39, Q40, Q41, Q42, Q43, Q44, Q45, Q46, Q47, Q48, Q49, Q50, Q51, Q52, Q53, Q54, Q55, Q56, Q57, Q58, Q59, Q60, Q61, Q62, Q63, Q64, Q65, Q66, Q67, Q68, Q69, Q70, Q71, Q72, Q73, Q74, Q75, Q76, Q77, Q78, Q79, Q80, Q81, Q82, Q83, Q84, Q85, Q86, Q87, Q88, Q89, Q90, Q91, Q92, Q93, Q94, Q95, Q96, Q97, Q98, Q99, Q100, Q101, Q102, Q103, Q104, Q105, Q106, Q107, Q108, Q109, Q110, Q111, Q112, Q113, Q114, Q115, Q116, Q117, Q118, Q119, Q120, Q121, Q122, Q123, Q124, Q125, Q126, Q127, Q128, Q129, Q130, Q131, Q132, Q133, Q134, Q135, Q136, Q137, Q138, Q139, Q140, Q141, Q142, Q143, Q144, Q145, Q146, Q147, Q148, Q149, Q150, Q151, Q152, Q153, Q154, Q155, Q156, Q157, Q158, Q159, Q160, Q161, Q162, Q163, Q164, Q165, Q166, Q167, Q168, Q169, Q170, Q171, Q172, Q173, Q174, Q175, Q176, Q177, Q178, Q179, Q180, Q181, Q182, Q183, Q184, Q185, Q186, Q187, Q188, Q189, Q190, Q191, Q192, Q193, Q194, Q195, Q196, Q197, Q198, Q199, Q200, Q201, Q202, Q203, Q204, Q205, Q206, Q207, Q208, Q209, Q210, Q211, Q212, Q213, Q214, Q215, Q216, Q217, Q218, Q219, Q220, Q221, Q222, Q223, Q224, Q225, Q226, Q227, Q228, Q229, Q230, Q231, Q232, Q233, Q234, Q235, Q236, Q237, Q238, Q239, Q240, Q241, Q242, Q243, Q244, Q245, Q246, Q247, Q248, Q249, Q250, Q251, Q252, Q253, Q254, Q255, Q256, Q257, Q258, Q259, Q260, Q261, Q262, Q263, Q264, Q265, Q266, Q267, Q268, Q269, Q270, Q271, Q272, Q273, Q274, Q275, Q276, Q277, Q278, Q279, Q280, Q281, Q282, Q283, Q284]), "operationType" : NewBodyOperationType.REMOVE, "oppositeDirection" : true, "depth" : 1800 * mm, "offsetDistance" : 25 * mm});
        }
    });
